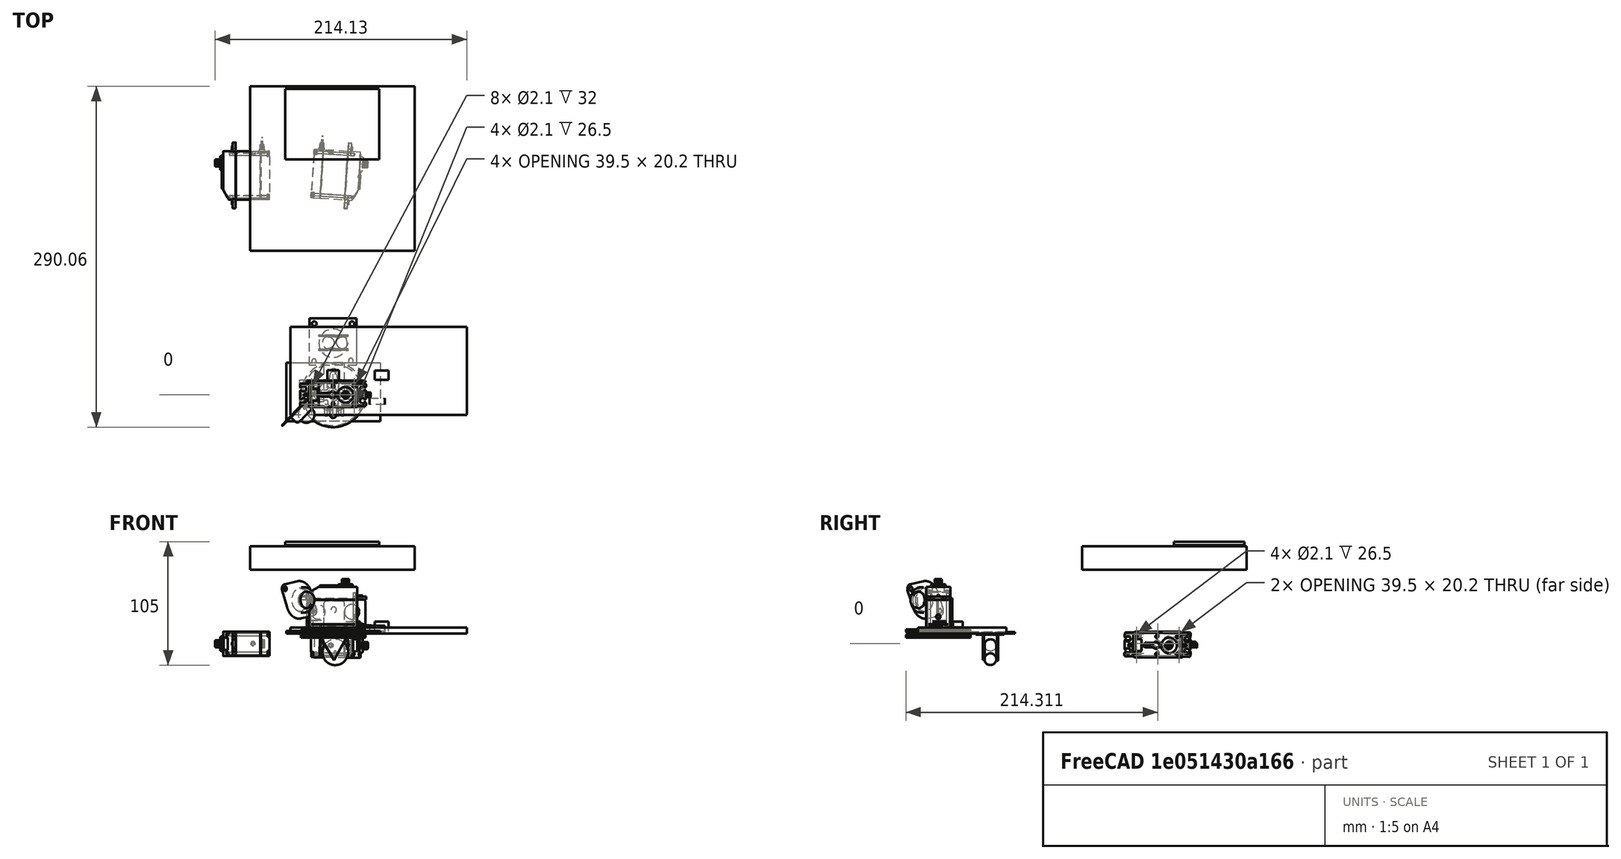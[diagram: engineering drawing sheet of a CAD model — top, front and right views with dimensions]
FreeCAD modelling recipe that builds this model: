
FCSTD DOCUMENT  (FreeCAD 0.19R24291 (Git))
Label: diseño_final
License: All rights reserved
LicenseURL: http://en.wikipedia.org/wiki/All_rights_reserved
objects: Sketcher::SketchObject×83, Part::Feature×51, PartDesign::Pad×39, PartDesign::Pocket×30, PartDesign::Body×19, Part::MultiFuse×16, App::LinkGroup×15, Part::Fillet×14, App::DocumentObjectGroup×10, Part::Box×8, Part::Compound×8, Part::Cut×6, PartDesign::PolarPattern×6, Part::Loft×6, Part::Mirroring×4, PartDesign::Mirrored×4, PartDesign::Fillet×4, PartDesign::Chamfer×4, Part::Cylinder×3, TechDraw::DrawProjGroupItem×3, +7 more types
note: 391 computed .brp shape members not serialized (recipe doc carries the construction recipe); baked Part::Feature solids carry a one-line shape summary decoded from their .brp

FEATURE [Sketcher::SketchObject] Sketch
  FullyConstrained = false
  MapMode = 5
  Support = -> [XY_Plane]
  sketch-geometry (8):
    g0: LineSegment StartX=-19.9829 StartY=19.2492 StartZ=0 EndX=20.0171 EndY=19.2492 EndZ=0
    g1: LineSegment StartX=20.0171 StartY=19.2492 StartZ=0 EndX=20.0171 EndY=-20.7508 EndZ=0
    g2: LineSegment StartX=20.0171 StartY=-20.7508 StartZ=0 EndX=-19.9829 EndY=-20.7508 EndZ=0
    g3: LineSegment StartX=-19.9829 StartY=-20.7508 StartZ=0 EndX=-19.9829 EndY=19.2492 EndZ=0
    g4: Circle CenterX=-16.0323 CenterY=14.5686 CenterZ=0 NormalX=0 NormalY=0 NormalZ=1 AngleXU=0 Radius=1.96692
    g5: Circle CenterX=16.0957 CenterY=14.4295 CenterZ=0 NormalX=0 NormalY=0 NormalZ=1 AngleXU=0 Radius=2.05352
    g6: Circle CenterX=15.1221 CenterY=-16.8639 CenterZ=0 NormalX=0 NormalY=0 NormalZ=1 AngleXU=0 Radius=1.99135
    g7: Circle CenterX=-16.1713 CenterY=-17.4203 CenterZ=0 NormalX=0 NormalY=0 NormalZ=1 AngleXU=0 Radius=1.95211
  constraints (10):
    c: Coincident(g0,g1)
    c: Coincident(g1,g2)
    c: Coincident(g2,g3)
    c: Coincident(g3,g0)
    c: Horizontal(g0)
    c: Horizontal(g2)
    c: Vertical(g1)
    c: Vertical(g3)
    c: DistanceY(g3,g3) = 40
    c: DistanceX(g0,g0) = 40
FEATURE [PartDesign::Pad] Pad
  Direction = (1,1,1)
  Length = 1
  Length2 = 100
  Profile = -> Sketch
  Type = 0
FEATURE [PartDesign::Body] Body  label="base_rueda"
  Group = -> [Sketch,Pad]
  Origin = -> Origin
  Placement = pos=(0,46,0) rot=(0,0,1;0rad)
  Tip = -> Pad
FEATURE [Sketcher::SketchObject] Sketch002
  FullyConstrained = false
  MapMode = 5
  Support = -> [XY_Plane001]
  sketch-geometry (4):
    g0: LineSegment StartX=11.942 StartY=-7.38734 StartZ=0 EndX=-0.260369 EndY=14.4324 EndZ=0
    g1: LineSegment StartX=-0.260369 StartY=14.4324 StartZ=0 EndX=-13.0556 EndY=-7.04506 EndZ=0
    g2: LineSegment StartX=-13.0556 StartY=-7.04506 StartZ=0 EndX=11.942 EndY=-7.38734 EndZ=0
    g3: Circle CenterX=-0.457983 CenterY=0 CenterZ=0 NormalX=0 NormalY=0 NormalZ=1 AngleXU=0 Radius=14.4338
  constraints (10):
    c: Coincident(g0,g1)
    c: Coincident(g1,g2)
    c: Coincident(g2,g0)
    c: Equal(g0,g1)
    c: Equal(g0,g2)
    c: PointOnObject(g0,g3)
    c: PointOnObject(g1,g3)
    c: PointOnObject(g2,g3)
    c: PointOnObject(g3,g-1)
    c: Distance(g2) = 25
FEATURE [PartDesign::Pad] Pad001
  Direction = (1,1,1)
  Length = 1
  Length2 = 100
  Profile = -> Sketch002
  Type = 0
FEATURE [PartDesign::Body] Body001  label="triangle1"
  Group = -> [Sketch002,Pad001]
  Origin = -> Origin001
  Placement = pos=(1,50,-9) rot=(-1,0,0;1.5708rad)
  Tip = -> Pad001
FEATURE [Sketcher::SketchObject] Sketch003
  FullyConstrained = false
  MapMode = 5
  Support = -> [XY_Plane002]
  sketch-geometry (4):
    g0: LineSegment StartX=11.942 StartY=-7.38734 StartZ=0 EndX=-0.260369 EndY=14.4324 EndZ=0
    g1: LineSegment StartX=-0.260369 StartY=14.4324 StartZ=0 EndX=-13.0556 EndY=-7.04506 EndZ=0
    g2: LineSegment StartX=-13.0556 StartY=-7.04506 StartZ=0 EndX=11.942 EndY=-7.38734 EndZ=0
    g3: Circle CenterX=-0.457983 CenterY=0 CenterZ=0 NormalX=0 NormalY=0 NormalZ=1 AngleXU=0 Radius=14.4338
  constraints (10):
    c: Coincident(g0,g1)
    c: Coincident(g1,g2)
    c: Coincident(g2,g0)
    c: Equal(g0,g1)
    c: Equal(g0,g2)
    c: PointOnObject(g0,g3)
    c: PointOnObject(g1,g3)
    c: PointOnObject(g2,g3)
    c: PointOnObject(g3,g-1)
    c: Distance(g2) = 25
FEATURE [PartDesign::Pad] Pad002
  Direction = (1,1,1)
  Length = 1
  Length2 = 100
  Profile = -> Sketch003
  Type = 0
FEATURE [PartDesign::Body] Body002  label="triangle2"
  Group = -> [Sketch003,Pad002]
  Origin = -> Origin002
  Placement = pos=(1,37.9904,-8.23205) rot=(-1,0,0;1.5708rad)
  Tip = -> Pad002
FEATURE [Part::Torus] Torus  label="rueda"
  Angle1 = -180
  Angle2 = 180
  Angle3 = 360
  AttacherType = Attacher::AttachEngine3D
  Placement = pos=(1.8355,44.3985,-16) rot=(0.57735,-0.57735,-0.57735;4.18879rad)
  Radius1 = 6
  Radius2 = 5
FEATURE [Part::Cylinder] Cylinder  label="base_movil"
  Angle = 360
  AttacherType = Attacher::AttachEngine3D
  Height = 1
  Placement = pos=(0,44,-1) rot=(0,0,1;0rad)
  Radius = 12
FEATURE [Sketcher::SketchObject] Sketch004
  FullyConstrained = false
  MapMode = 5
  Support = -> [XY_Plane003]
  sketch-geometry (8):
    g0: LineSegment StartX=-25.0348 StartY=11.057 StartZ=0 EndX=26.1474 EndY=11.057 EndZ=0
    g1: LineSegment StartX=26.1474 StartY=11.057 StartZ=0 EndX=26.1474 EndY=-9.24896 EndZ=0
    g2: LineSegment StartX=26.1474 StartY=-9.24896 StartZ=0 EndX=-25.0348 EndY=-9.24896 EndZ=0
    g3: LineSegment StartX=-25.0348 StartY=-9.24896 StartZ=0 EndX=-25.0348 EndY=11.057 EndZ=0
    g4: Circle CenterX=-23.0712 CenterY=8.82531 CenterZ=0 NormalX=0 NormalY=0 NormalZ=1 AngleXU=0 Radius=0.698514
    g5: Circle CenterX=23.9427 CenterY=8.43482 CenterZ=0 NormalX=0 NormalY=0 NormalZ=1 AngleXU=0 Radius=0.740892
    g6: Circle CenterX=24.0208 CenterY=-7.49681 CenterZ=0 NormalX=0 NormalY=0 NormalZ=1 AngleXU=0 Radius=0.707187
    g7: Circle CenterX=-23.1493 CenterY=-7.02823 CenterZ=0 NormalX=0 NormalY=0 NormalZ=1 AngleXU=0 Radius=0.720017
  constraints (8):
    c: Coincident(g0,g1)
    c: Coincident(g1,g2)
    c: Coincident(g2,g3)
    c: Coincident(g3,g0)
    c: Horizontal(g0)
    c: Horizontal(g2)
    c: Vertical(g1)
    c: Vertical(g3)
FEATURE [PartDesign::Pad] Pad003
  Direction = (1,1,1)
  Length = 2
  Length2 = 100
  Profile = -> Sketch004
  Type = 0
FEATURE [PartDesign::Body] Body003  label="Body"
  Group = -> [Sketch004,Pad003]
  Origin = -> Origin003
  Tip = -> Pad003
FEATURE [Part::FeaturePython] Tube  label="cilindro1"  # WARN: FeaturePython — macro-defined, semantics opaque (R4)
  AttacherType = Attacher::AttachEngine3D
  Height = 10
  InnerRadius = 5
  OuterRadius = 6
  Placement = pos=(-16,1,1) rot=(0,0,1;0rad)
FEATURE [Part::FeaturePython] Tube001  label="Cilindro2"  # WARN: FeaturePython — macro-defined, semantics opaque (R4)
  AttacherType = Attacher::AttachEngine3D
  Height = 10
  InnerRadius = 5
  OuterRadius = 6
  Placement = pos=(17,1,0) rot=(0,0,1;0rad)
FEATURE [Part::Box] Box  label="contacto1"
  AttacherType = Attacher::AttachEngine3D
  Height = 1
  Length = 2
  Placement = pos=(-7,-18,-1) rot=(0,0,1;0rad)
  Width = 10
FEATURE [Part::Box] Box001  label="contacto2"
  AttacherType = Attacher::AttachEngine3D
  Height = 1
  Length = 2
  Placement = pos=(-2,-18,-1) rot=(0,0,1;0rad)
  Width = 10
FEATURE [Part::Box] Box002  label="contacto3"
  AttacherType = Attacher::AttachEngine3D
  Height = 1
  Length = 2
  Placement = pos=(3,-18,-1) rot=(0,0,1;0rad)
  Width = 10
FEATURE [Part::Box] Box003  label="contacto4"
  AttacherType = Attacher::AttachEngine3D
  Height = 1
  Length = 2
  Placement = pos=(7,-18,-1) rot=(0,0,1;0rad)
  Width = 10
FEATURE [App::LinkGroup] LinkGroup  label="sensor_ultrasonidos"
  ElementList = -> [Box003,Box002,Tube001,Box,Box001,Body003,Tube]
  LinkMode = 0
  Placement = pos=(3.11266,-4.47148,19.5285) rot=(0,0.707107,-0.707107;3.14159rad)
FEATURE [Sketcher::SketchObject] Sketch005  label="wheel-generic-sketch"
  FullyConstrained = false
  MapMode = 5
  Placement = pos=(0,0,0) rot=(1,0,0;1.5708rad)
  sketch-geometry (7):
    g0: LineSegment StartX=0 StartY=-3.5 StartZ=0 EndX=0 EndY=3.5 EndZ=0
    g1: LineSegment StartX=0 StartY=3.5 StartZ=0 EndX=27.5 EndY=3.5 EndZ=0
    g2: LineSegment StartX=27.5 StartY=3.5 StartZ=0 EndX=27.5 EndY=1.5 EndZ=0
    g3: LineSegment StartX=27.5 StartY=1.5 StartZ=0 EndX=26 EndY=0 EndZ=0
    g4: LineSegment StartX=26 StartY=0 StartZ=0 EndX=27.5 EndY=-1.5 EndZ=0
    g5: LineSegment StartX=27.5 StartY=-1.5 StartZ=0 EndX=27.5 EndY=-3.5 EndZ=0
    g6: LineSegment StartX=27.5 StartY=-3.5 StartZ=0 EndX=0 EndY=-3.5 EndZ=0
  constraints (20):
    c: Vertical(g0)
    c: Coincident(g0,g1)
    c: Horizontal(g1)
    c: Coincident(g1,g2)
    c: Vertical(g2)
    c: Coincident(g2,g3)
    c: Coincident(g3,g4)
    c: Coincident(g4,g5)
    c: Coincident(g5,g6)
    c: Coincident(g6,g0)
    c: Horizontal(g6)
    c: Vertical(g5)
    c: PointOnObject(g0,g-2)
    c: Symmetric(g0,g0,g-1)
    c: PointOnObject(g3,g-1)
    c: Symmetric(g4,g2,g-1)
    c: Angle(g3,g-1) = 2.35619
    c: DistanceY(g4,g2) = 3
    c: DistanceX(g1) = 27.5
    c: DistanceY(g0) = 7
FEATURE [PartDesign::Revolution] Revolution  label="wheel-generic"
  AllowMultiFace = false
  Angle = 360
  Axis = (0,0,1)
  Base = (0,0,0)
  Placement = pos=(0,0,0) rot=(1,0,0;1.5708rad)
  Profile = -> Sketch005
  ReferenceAxis = -> Sketch005 [V_Axis]
  Reversed = true
FEATURE [Sketcher::SketchObject] Sketch001  label="horn-top-left-quarter-sketch"
  FullyConstrained = false
  MapMode = 5
  sketch-geometry (12):
    g0: LineSegment StartX=0 StartY=0 StartZ=0 EndX=0 EndY=19.7 EndZ=0
    g1: LineSegment StartX=-4.73762 StartY=4.73762 StartZ=0 EndX=0 EndY=0 EndZ=0
    g2: ArcOfCircle CenterX=-5.79828 CenterY=5.79828 CenterZ=0 NormalX=0 NormalY=0 NormalZ=1 AngleXU=0 Radius=1.5 StartAngle=4.7124 EndAngle=6.28317
    g3: ArcOfCircle CenterX=-17 CenterY=0 CenterZ=0 NormalX=0 NormalY=0 NormalZ=1 AngleXU=0 Radius=2.7 StartAngle=1.73871 EndAngle=3.14159
    g4: ArcOfCircle CenterX=0 CenterY=17 CenterZ=0 NormalX=0 NormalY=0 NormalZ=1 AngleXU=0 Radius=2.7 StartAngle=1.5708 EndAngle=2.97368
    g5: LineSegment StartX=-4.29828 StartY=5.79826 StartZ=0 EndX=-4.29828 EndY=7.79826 EndZ=0
    g6: LineSegment StartX=-5.79826 StartY=4.29828 StartZ=0 EndX=-7.79826 EndY=4.29828 EndZ=0
    g7: LineSegment StartX=-4.29828 StartY=7.79826 StartZ=0 EndX=-2.66203 EndY=17.4512 EndZ=0
    g8: LineSegment StartX=-17.4512 StartY=2.66203 StartZ=0 EndX=-7.79826 EndY=4.29828 EndZ=0
    g9: LineSegment StartX=-7.79826 StartY=4.29828 StartZ=0 EndX=-7.79826 EndY=0 EndZ=0
    g10: LineSegment StartX=-4.29828 StartY=7.79826 StartZ=0 EndX=0 EndY=7.79826 EndZ=0
    g11: LineSegment StartX=-19.7 StartY=0 StartZ=0 EndX=0 EndY=0 EndZ=0
  constraints (39):
    c: PointOnObject(g0,g-2)
    c: Coincident(g1,g-1)
    c: Angle(g-1,g1) = 2.35619
    c: PointOnObject(g2,g1)
    c: PointOnObject(g1,g2)
    c: Coincident(g4,g0)
    c: PointOnObject(g4,g0)
    c: Equal(g3,g4)
    c: Radius(g3) = 2.7
    c: Coincident(g5,g2)
    c: Vertical(g5)
    c: Coincident(g6,g2)
    c: Horizontal(g6)
    c: Equal(g6,g5)
    c: Tangent(g7,g4)
    c: Coincident(g7,g4)
    c: Coincident(g7,g5)
    c: Coincident(g8,g3)
    c: Coincident(g8,g6)
    c: Tangent(g8,g3)
    c: Tangent(g2,g6)
    c: DistanceX(g6) = -2
    c: Radius(g2) = 1.5
    c: Vertical(g9)
    c: Coincident(g9,g6)
    c: Horizontal(g10)
    c: Coincident(g10,g5)
    c: PointOnObject(g10,g0)
    c: Equal(g9,g10)
    c: Distance(g1) = 6.7
    c: PointOnObject(g3,g-1)
    c: PointOnObject(g3,g-1)
    c: Horizontal(g11)
    c: Coincident(g11,g-1)
    c: Coincident(g11,g3)
    c: Equal(g11,g0)
    c: PointOnObject(g9,g11)
    c: Coincident(g0,g-1)
    c: DistanceX(g11) = 19.7
FEATURE [PartDesign::Pad] Pad004  label="horn-top-left-quarter"
  AllowMultiFace = false
  Direction = (1,1,1)
  Length = 6
  Length2 = 100
  Profile = -> Sketch001
  Type = 0
FEATURE [Part::Mirroring] Part__Mirroring  label="horn-top-left-quarter (Mirror #1)"
  Base = (0,0,0)
  Normal = (1,0,0)
  Source = -> Pad004
FEATURE [Part::MultiFuse] Fusion
  Shapes = -> [Part__Mirroring,Pad004]
FEATURE [Part::Mirroring] Part__Mirroring001  label="Fusion (Mirror #2)"
  Base = (0,0,0)
  Normal = (0,1,0)
  Source = -> Fusion
FEATURE [Part::MultiFuse] Fusion001  label="4-arms-horn-body"
  Placement = pos=(0,0,-0.5) rot=(0,0,1;0rad)
  Shapes = -> [Part__Mirroring001,Fusion]
FEATURE [Part::Cut] Cut  label="wheel-horn"
  Base = -> Revolution
  Tool = -> Fusion001
FEATURE [Sketcher::SketchObject] Sketch006  label="shaft-drill-sketch"
  FullyConstrained = false
  MapMode = 5
  Placement = pos=(0,0,-0.5) rot=(0,0,1;0rad)
  Support = -> [Cut]
  sketch-geometry (1):
    g0: Circle CenterX=0 CenterY=0 CenterZ=0 NormalX=0 NormalY=0 NormalZ=1 AngleXU=0 Radius=5.2
  constraints (2):
    c: Coincident(g0,g-1)
    c: Radius(g0) = 5.2
FEATURE [PartDesign::Pocket] Pocket  label="shaft-drill"
  AllowMultiFace = false
  Length = 5
  Length2 = 100
  Profile = -> Sketch006
  Type = 1
FEATURE [Sketcher::SketchObject] Sketch007  label="drill-horn-master-sketch"
  FullyConstrained = false
  MapMode = 5
  Placement = pos=(0,0,-0.5) rot=(0,0,1;0rad)
  Support = -> [Pocket]
  sketch-geometry (1):
    g0: Circle CenterX=-16.15 CenterY=0 CenterZ=0 NormalX=0 NormalY=0 NormalZ=1 AngleXU=0 Radius=0.85
  constraints (3):
    c: PointOnObject(g0,g-1)
    c: Radius(g0) = 0.85
    c: DistanceX(g-1,g0) = -16.15
FEATURE [PartDesign::Pocket] Pocket001  label="drill-horn-master"
  AllowMultiFace = false
  Length = 5
  Length2 = 100
  Profile = -> Sketch007
  Type = 1
FEATURE [PartDesign::PolarPattern] PolarPattern  label="horn-drills"
  Angle = 360
  Axis = -> Sketch007 [N_Axis]
  Occurrences = 2
  Originals = -> [Pocket001]
FEATURE [Sketcher::SketchObject] Sketch008  label="horn-screw-room-master-sketch"
  FullyConstrained = false
  MapMode = 5
  Placement = pos=(0,8e-16,3.5) rot=(0,0,1;0rad)
  Support = -> [PolarPattern]
  sketch-geometry (1):
    g0: Circle CenterX=-16.15 CenterY=0 CenterZ=0 NormalX=0 NormalY=0 NormalZ=1 AngleXU=0 Radius=4
  constraints (3):
    c: PointOnObject(g0,g-1)
    c: DistanceX(g-1,g0) = -16.15
    c: Radius(g0) = 4
FEATURE [PartDesign::Pocket] Pocket002  label="horn-screw-room-master"
  AllowMultiFace = false
  Length = 4
  Length2 = 100
  Profile = -> Sketch008
  Type = 0
FEATURE [PartDesign::PolarPattern] PolarPattern001  label="horn-screws-room"
  Angle = 360
  Axis = -> Sketch008 [N_Axis]
  Occurrences = 2
  Originals = -> [Pocket002]
FEATURE [Part::Feature] PolarPattern001001  label="Renacuajo-wheel-4-arms-horn-final"
  shape: bbox 55 x 55 x 7 mm, 34 faces (baked)
FEATURE [App::LinkGroup] LinkGroup002  label="rueda1"
  ElementList = -> [PolarPattern001001,PolarPattern001]
  LinkMode = 0
  Placement = pos=(-99.447,198,-8.79556) rot=(0,-1,0;1.5708rad)
FEATURE [Sketcher::SketchObject] Sketch009  label="wheel-generic-sketch001"
  FullyConstrained = false
  MapMode = 5
  Placement = pos=(0,0,0) rot=(1,0,0;1.5708rad)
  sketch-geometry (7):
    g0: LineSegment StartX=0 StartY=-3.5 StartZ=0 EndX=0 EndY=3.5 EndZ=0
    g1: LineSegment StartX=0 StartY=3.5 StartZ=0 EndX=27.5 EndY=3.5 EndZ=0
    g2: LineSegment StartX=27.5 StartY=3.5 StartZ=0 EndX=27.5 EndY=1.5 EndZ=0
    g3: LineSegment StartX=27.5 StartY=1.5 StartZ=0 EndX=26 EndY=0 EndZ=0
    g4: LineSegment StartX=26 StartY=0 StartZ=0 EndX=27.5 EndY=-1.5 EndZ=0
    g5: LineSegment StartX=27.5 StartY=-1.5 StartZ=0 EndX=27.5 EndY=-3.5 EndZ=0
    g6: LineSegment StartX=27.5 StartY=-3.5 StartZ=0 EndX=0 EndY=-3.5 EndZ=0
  constraints (20):
    c: Vertical(g0)
    c: Coincident(g0,g1)
    c: Horizontal(g1)
    c: Coincident(g1,g2)
    c: Vertical(g2)
    c: Coincident(g2,g3)
    c: Coincident(g3,g4)
    c: Coincident(g4,g5)
    c: Coincident(g5,g6)
    c: Coincident(g6,g0)
    c: Horizontal(g6)
    c: Vertical(g5)
    c: PointOnObject(g0,g-2)
    c: Symmetric(g0,g0,g-1)
    c: PointOnObject(g3,g-1)
    c: Symmetric(g4,g2,g-1)
    c: Angle(g3,g-1) = 2.35619
    c: DistanceY(g4,g2) = 3
    c: DistanceX(g1) = 27.5
    c: DistanceY(g0) = 7
FEATURE [PartDesign::Revolution] Revolution001  label="wheel-generic001"
  AllowMultiFace = false
  Angle = 360
  Axis = (0,0,1)
  Base = (0,0,0)
  Placement = pos=(0,0,0) rot=(1,0,0;1.5708rad)
  Profile = -> Sketch009
  ReferenceAxis = -> Sketch009 [V_Axis]
  Reversed = true
FEATURE [Sketcher::SketchObject] Sketch010  label="horn-top-left-quarter-sketch001"
  FullyConstrained = false
  MapMode = 5
  sketch-geometry (12):
    g0: LineSegment StartX=0 StartY=0 StartZ=0 EndX=0 EndY=19.7 EndZ=0
    g1: LineSegment StartX=-4.73762 StartY=4.73762 StartZ=0 EndX=0 EndY=0 EndZ=0
    g2: ArcOfCircle CenterX=-5.79828 CenterY=5.79828 CenterZ=0 NormalX=0 NormalY=0 NormalZ=1 AngleXU=0 Radius=1.5 StartAngle=4.7124 EndAngle=6.28317
    g3: ArcOfCircle CenterX=-17 CenterY=0 CenterZ=0 NormalX=0 NormalY=0 NormalZ=1 AngleXU=0 Radius=2.7 StartAngle=1.73871 EndAngle=3.14159
    g4: ArcOfCircle CenterX=0 CenterY=17 CenterZ=0 NormalX=0 NormalY=0 NormalZ=1 AngleXU=0 Radius=2.7 StartAngle=1.5708 EndAngle=2.97368
    g5: LineSegment StartX=-4.29828 StartY=5.79826 StartZ=0 EndX=-4.29828 EndY=7.79826 EndZ=0
    g6: LineSegment StartX=-5.79826 StartY=4.29828 StartZ=0 EndX=-7.79826 EndY=4.29828 EndZ=0
    g7: LineSegment StartX=-4.29828 StartY=7.79826 StartZ=0 EndX=-2.66203 EndY=17.4512 EndZ=0
    g8: LineSegment StartX=-17.4512 StartY=2.66203 StartZ=0 EndX=-7.79826 EndY=4.29828 EndZ=0
    g9: LineSegment StartX=-7.79826 StartY=4.29828 StartZ=0 EndX=-7.79826 EndY=0 EndZ=0
    g10: LineSegment StartX=-4.29828 StartY=7.79826 StartZ=0 EndX=0 EndY=7.79826 EndZ=0
    g11: LineSegment StartX=-19.7 StartY=0 StartZ=0 EndX=0 EndY=0 EndZ=0
  constraints (39):
    c: PointOnObject(g0,g-2)
    c: Coincident(g1,g-1)
    c: Angle(g-1,g1) = 2.35619
    c: PointOnObject(g2,g1)
    c: PointOnObject(g1,g2)
    c: Coincident(g4,g0)
    c: PointOnObject(g4,g0)
    c: Equal(g3,g4)
    c: Radius(g3) = 2.7
    c: Coincident(g5,g2)
    c: Vertical(g5)
    c: Coincident(g6,g2)
    c: Horizontal(g6)
    c: Equal(g6,g5)
    c: Tangent(g7,g4)
    c: Coincident(g7,g4)
    c: Coincident(g7,g5)
    c: Coincident(g8,g3)
    c: Coincident(g8,g6)
    c: Tangent(g8,g3)
    c: Tangent(g2,g6)
    c: DistanceX(g6) = -2
    c: Radius(g2) = 1.5
    c: Vertical(g9)
    c: Coincident(g9,g6)
    c: Horizontal(g10)
    c: Coincident(g10,g5)
    c: PointOnObject(g10,g0)
    c: Equal(g9,g10)
    c: Distance(g1) = 6.7
    c: PointOnObject(g3,g-1)
    c: PointOnObject(g3,g-1)
    c: Horizontal(g11)
    c: Coincident(g11,g-1)
    c: Coincident(g11,g3)
    c: Equal(g11,g0)
    c: PointOnObject(g9,g11)
    c: Coincident(g0,g-1)
    c: DistanceX(g11) = 19.7
FEATURE [PartDesign::Pad] Pad005  label="horn-top-left-quarter001"
  AllowMultiFace = false
  Direction = (1,1,1)
  Length = 6
  Length2 = 100
  Profile = -> Sketch010
  Type = 0
FEATURE [Part::Mirroring] Part__Mirroring002  label="horn-top-left-quarter (Mirror #1)001"
  Base = (0,0,0)
  Normal = (1,0,0)
  Source = -> Pad005
FEATURE [Part::MultiFuse] Fusion002
  Shapes = -> [Part__Mirroring002,Pad005]
FEATURE [Part::Mirroring] Part__Mirroring003  label="Fusion (Mirror #2)001"
  Base = (0,0,0)
  Normal = (0,1,0)
  Source = -> Fusion002
FEATURE [Part::MultiFuse] Fusion003  label="4-arms-horn-body001"
  Placement = pos=(0,0,-0.5) rot=(0,0,1;0rad)
  Shapes = -> [Part__Mirroring003,Fusion002]
FEATURE [Part::Cut] Cut001  label="wheel-horn001"
  Base = -> Revolution001
  Tool = -> Fusion003
FEATURE [Sketcher::SketchObject] Sketch011  label="shaft-drill-sketch001"
  FullyConstrained = false
  MapMode = 5
  Placement = pos=(0,0,-0.5) rot=(0,0,1;0rad)
  Support = -> [Cut001]
  sketch-geometry (1):
    g0: Circle CenterX=0 CenterY=0 CenterZ=0 NormalX=0 NormalY=0 NormalZ=1 AngleXU=0 Radius=5.2
  constraints (2):
    c: Coincident(g0,g-1)
    c: Radius(g0) = 5.2
FEATURE [PartDesign::Pocket] Pocket003  label="shaft-drill001"
  AllowMultiFace = false
  Length = 5
  Length2 = 100
  Profile = -> Sketch011
  Type = 1
FEATURE [Sketcher::SketchObject] Sketch012  label="drill-horn-master-sketch001"
  FullyConstrained = false
  MapMode = 5
  Placement = pos=(0,0,-0.5) rot=(0,0,1;0rad)
  Support = -> [Pocket003]
  sketch-geometry (1):
    g0: Circle CenterX=-16.15 CenterY=0 CenterZ=0 NormalX=0 NormalY=0 NormalZ=1 AngleXU=0 Radius=0.85
  constraints (3):
    c: PointOnObject(g0,g-1)
    c: Radius(g0) = 0.85
    c: DistanceX(g-1,g0) = -16.15
FEATURE [PartDesign::Pocket] Pocket004  label="drill-horn-master001"
  AllowMultiFace = false
  Length = 5
  Length2 = 100
  Profile = -> Sketch012
  Type = 1
FEATURE [PartDesign::PolarPattern] PolarPattern001002  label="horn-drills001"
  Angle = 360
  Axis = -> Sketch012 [N_Axis]
  Occurrences = 2
  Originals = -> [Pocket004]
FEATURE [Sketcher::SketchObject] Sketch013  label="horn-screw-room-master-sketch001"
  FullyConstrained = false
  MapMode = 5
  Placement = pos=(0,8e-16,3.5) rot=(0,0,1;0rad)
  Support = -> [PolarPattern001002]
  sketch-geometry (1):
    g0: Circle CenterX=-16.15 CenterY=0 CenterZ=0 NormalX=0 NormalY=0 NormalZ=1 AngleXU=0 Radius=4
  constraints (3):
    c: PointOnObject(g0,g-1)
    c: DistanceX(g-1,g0) = -16.15
    c: Radius(g0) = 4
FEATURE [PartDesign::Pocket] Pocket005  label="horn-screw-room-master001"
  AllowMultiFace = false
  Length = 4
  Length2 = 100
  Profile = -> Sketch013
  Type = 0
FEATURE [PartDesign::PolarPattern] PolarPattern001003  label="horn-screws-room001"
  Angle = 360
  Axis = -> Sketch013 [N_Axis]
  Occurrences = 2
  Originals = -> [Pocket005]
FEATURE [Part::Feature] PolarPattern001004  label="Renacuajo-wheel-4-arms-horn-final001"
  shape: bbox 55 x 55 x 7 mm, 34 faces (baked)
FEATURE [App::LinkGroup] LinkGroup003  label="rueda2"
  ElementList = -> [PolarPattern001004,PolarPattern001003]
  LinkMode = 0
  Placement = pos=(30,196,-9.00002) rot=(0,-1,0;1.5708rad)
FEATURE [Sketcher::SketchObject] Sketch014
  FullyConstrained = false
  MapMode = 5
  Support = -> [XY_Plane004]
  sketch-geometry (4):
    g0: LineSegment StartX=-36.1738 StartY=-17.1935 StartZ=0 EndX=-36.1738 EndY=57.8065 EndZ=0
    g1: LineSegment StartX=-36.1738 StartY=57.8065 StartZ=0 EndX=113.826 EndY=57.8065 EndZ=0
    g2: LineSegment StartX=113.826 StartY=57.8065 StartZ=0 EndX=113.826 EndY=-17.1935 EndZ=0
    g3: LineSegment StartX=113.826 StartY=-17.1935 StartZ=0 EndX=-36.1738 EndY=-17.1935 EndZ=0
  constraints (10):
    c: Vertical(g0)
    c: DistanceY(g0,g0) = 75
    c: Coincident(g1,g0)
    c: Horizontal(g1)
    c: DistanceX(g1,g1) = 150
    c: Coincident(g2,g1)
    c: Vertical(g2)
    c: Equal(g0,g2)
    c: Coincident(g3,g2)
    c: Coincident(g3,g0)
FEATURE [PartDesign::Pad] Pad006
  Direction = (1,1,1)
  Length = 5
  Length2 = 100
  Profile = -> Sketch014
  Type = 0
FEATURE [PartDesign::Body] Body004  label="base_DieGo"
  Group = -> [Sketch014,Pad006]
  Origin = -> Origin004
  Tip = -> Pad006
FEATURE [Sketcher::SketchObject] Sketch015  label="servo-body-sketch"
  FullyConstrained = false
  MapMode = 5
  Placement = pos=(0,0,0) rot=(1,0,0;1.5708rad)
  sketch-geometry (5):
    g0: LineSegment StartX=20.55 StartY=39.6 StartZ=0 EndX=20.55 EndY=0 EndZ=0
    g1: LineSegment StartX=20.55 StartY=0 StartZ=0 EndX=-20.55 EndY=0 EndZ=0
    g2: LineSegment StartX=-20.55 StartY=0 StartZ=0 EndX=-20.55 EndY=34.9 EndZ=0
    g3: LineSegment StartX=-20.55 StartY=34.9 StartZ=0 EndX=-12.25 EndY=39.6 EndZ=0
    g4: LineSegment StartX=-12.25 StartY=39.6 StartZ=0 EndX=20.55 EndY=39.6 EndZ=0
  constraints (15):
    c: Coincident(g0,g1)
    c: Coincident(g1,g2)
    c: Horizontal(g1)
    c: Vertical(g0)
    c: Vertical(g2)
    c: Symmetric(g1,g0,g-2)
    c: PointOnObject(g1,g-1)
    c: DistanceX(g1) = -41.1
    c: DistanceY(g0) = -39.6
    c: Coincident(g3,g2)
    c: Horizontal(g4)
    c: Coincident(g4,g0)
    c: Coincident(g3,g4)
    c: DistanceY(g2) = 34.9
    c: DistanceX(g4) = 32.8
FEATURE [PartDesign::Pad] Pad007  label="servo-body-1"
  AllowMultiFace = false
  Direction = (1,1,1)
  Length = 20.8
  Length2 = 100
  Midplane = true
  Placement = pos=(0,0,0) rot=(1,0,0;1.5708rad)
  Profile = -> Sketch
  Type = 0
FEATURE [Sketcher::SketchObject] Sketch016  label="bottom-master-sketch"
  ExternalGeometry = -> [Pad007]
  FullyConstrained = false
  MapMode = 5
  Placement = pos=(0,0,0) rot=(1,0,0;3.14159rad)
  Support = -> [Pad007]
  sketch-geometry (15):
    g0: LineSegment StartX=-20.55 StartY=10.4 StartZ=0 EndX=-18.2075 EndY=8.05754 EndZ=0
    g1: Circle CenterX=-18.2075 CenterY=8.05754 CenterZ=0 NormalX=0 NormalY=0 NormalZ=1 AngleXU=0 Radius=1.05
    g2: GeomPoint X=-18.95 Y=8.8 Z=0
    g3: LineSegment StartX=-18.2075 StartY=8.05754 StartZ=0 EndX=-18.2075 EndY=6 EndZ=0
    g4: LineSegment StartX=-18.2075 StartY=8.05754 StartZ=0 EndX=-16.15 EndY=8.05754 EndZ=0
    g5: LineSegment StartX=-20.55 StartY=6 StartZ=0 EndX=-20.55 EndY=10.4 EndZ=0
    g6: LineSegment StartX=-20.55 StartY=10.4 StartZ=0 EndX=-16.15 EndY=10.4 EndZ=0
    g7: LineSegment StartX=-16.15 StartY=10.4 StartZ=0 EndX=-16.15 EndY=8.05754 EndZ=0
    g8: ArcOfCircle CenterX=-18.2075 CenterY=8.05754 CenterZ=0 NormalX=0 NormalY=0 NormalZ=1 AngleXU=0 Radius=2.05754 StartAngle=4.71239 EndAngle=6.28319
    g9: LineSegment StartX=-20.55 StartY=6 StartZ=0 EndX=-18.2075 EndY=6 EndZ=0
    g10: ArcOfCircle CenterX=-18.2075 CenterY=-8.05754 CenterZ=0 NormalX=0 NormalY=0 NormalZ=1 AngleXU=0 Radius=2.05754 StartAngle=5.46325e-06 EndAngle=1.5708
    g11: LineSegment StartX=-18.2075 StartY=-6 StartZ=0 EndX=-20.55 EndY=-6 EndZ=0
    g12: LineSegment StartX=-20.55 StartY=-6 StartZ=0 EndX=-20.55 EndY=-10.4 EndZ=0
    g13: LineSegment StartX=-20.55 StartY=-10.4 StartZ=0 EndX=-16.15 EndY=-10.4 EndZ=0
    g14: LineSegment StartX=-16.15 StartY=-10.4 StartZ=0 EndX=-16.15 EndY=-8.05753 EndZ=0
  constraints (40):
    c: Coincident(g0,g-4)
    c: Angle(g-4,g0) = 0.785398
    c: Radius(g1) = 1.05
    c: Coincident(g1,g0)
    c: PointOnObject(g2,g0)
    c: PointOnObject(g2,g1)
    c: DistanceX(g2,g0) = -1.6
    c: Vertical(g3)
    c: Coincident(g3,g0)
    c: Coincident(g0,g4)
    c: Horizontal(g4)
    c: Equal(g3,g4)
    c: Coincident(g5,g6)
    c: Vertical(g5)
    c: Horizontal(g6)
    c: Vertical(g7)
    c: Coincident(g7,g6)
    c: Coincident(g7,g4)
    c: Coincident(g5,g0)
    c: Coincident(g8,g0)
    c: Coincident(g8,g4)
    c: Coincident(g3,g8)
    c: Coincident(g9,g5)
    c: Coincident(g9,g3)
    c: Horizontal(g9)
    c: DistanceY(g0,g5) = -4.4
    c: Horizontal(g11)
    c: Coincident(g11,g12)
    c: Vertical(g12)
    c: Coincident(g12,g13)
    c: Horizontal(g13)
    c: Coincident(g13,g14)
    c: Vertical(g14)
    c: Coincident(g12,g-4)
    c: Symmetric(g10,g0,g-1)
    c: Symmetric(g13,g6,g-1)
    c: Symmetric(g11,g3,g-1)
    c: Equal(g10,g8)
    c: Coincident(g10,g11)
    c: Coincident(g10,g14)
FEATURE [PartDesign::Pocket] Pocket006  label="bottom-master"
  AllowMultiFace = false
  Length = 1.8
  Length2 = 100
  Placement = pos=(0,0,0) rot=(1,0,0;1.5708rad)
  Profile = -> Sketch001
  Type = 0
FEATURE [PartDesign::Mirrored] Mirrored  label="bottom-1"
  MirrorPlane = -> Sketch016 [V_Axis]
  Originals = -> [Pocket006]
  Placement = pos=(0,0,0) rot=(1,0,0;1.5708rad)
FEATURE [Sketcher::SketchObject] Sketch017  label="bottom-2-sketch"
  ExternalGeometry = -> [Mirrored]
  FullyConstrained = false
  MapMode = 5
  Placement = pos=(0,8e-16,1.8) rot=(1,0,0;3.14159rad)
  Support = -> [Mirrored]
  sketch-geometry (10):
    g0: LineSegment StartX=-20.55 StartY=10.4 StartZ=0 EndX=-18.85 EndY=8.7 EndZ=0
    g1: Circle CenterX=-18.1075 CenterY=7.95754 CenterZ=0 NormalX=0 NormalY=0 NormalZ=1 AngleXU=0 Radius=1.05
    g2: Circle CenterX=-18.1075 CenterY=7.95754 CenterZ=0 NormalX=0 NormalY=0 NormalZ=1 AngleXU=0 Radius=1.9
    g3: Circle CenterX=-18.1075 CenterY=-7.95754 CenterZ=0 NormalX=0 NormalY=0 NormalZ=1 AngleXU=0 Radius=1.9
    g4: Circle CenterX=18.1075 CenterY=7.95754 CenterZ=0 NormalX=0 NormalY=0 NormalZ=1 AngleXU=0 Radius=1.9
    g5: Circle CenterX=18.1075 CenterY=-7.95754 CenterZ=0 NormalX=0 NormalY=0 NormalZ=1 AngleXU=0 Radius=1.9
    g6: LineSegment StartX=-18.1075 StartY=7.95754 StartZ=0 EndX=18.1075 EndY=7.95754 EndZ=0
    g7: LineSegment StartX=18.1075 StartY=7.95754 StartZ=0 EndX=18.1075 EndY=-7.95754 EndZ=0
    g8: LineSegment StartX=18.1075 StartY=-7.95754 StartZ=0 EndX=-18.1075 EndY=-7.95754 EndZ=0
    g9: LineSegment StartX=-18.1075 StartY=-7.95754 StartZ=0 EndX=-18.1075 EndY=7.95754 EndZ=0
  constraints (24):
    c: Angle(g0,g-3) = 0.785398
    c: Coincident(g0,g-3)
    c: Radius(g1) = 1.05
    c: PointOnObject(g1,g0)
    c: PointOnObject(g0,g1)
    c: DistanceX(g0,g0) = 1.7
    c: Coincident(g2,g1)
    c: Radius(g2) = 1.9
    c: Equal(g3,g2)
    c: Equal(g2,g4)
    c: Equal(g4,g5)
    c: Coincident(g6,g7)
    c: Coincident(g7,g8)
    c: Coincident(g8,g9)
    c: Coincident(g9,g6)
    c: Horizontal(g6)
    c: Horizontal(g8)
    c: Vertical(g7)
    c: Vertical(g9)
    c: Symmetric(g6,g7,g-1)
    c: Coincident(g6,g1)
    c: Coincident(g3,g8)
    c: Coincident(g6,g4)
    c: Coincident(g5,g7)
FEATURE [PartDesign::Pocket] Pocket007  label="bottom-2"
  AllowMultiFace = false
  Length = 0.6
  Length2 = 100
  Placement = pos=(0,0,0) rot=(1,0,0;1.5708rad)
  Profile = -> Sketch002
  Type = 0
FEATURE [Sketcher::SketchObject] Sketch018  label="bottom-drills-sketch"
  ExternalGeometry = -> [Pocket007]
  FullyConstrained = false
  MapMode = 5
  Placement = pos=(0,1.3e-15,2.4) rot=(1,0,0;3.14159rad)
  Support = -> [Pocket007]
  sketch-geometry (8):
    g0: Circle CenterX=-18.1075 CenterY=7.95754 CenterZ=0 NormalX=0 NormalY=0 NormalZ=1 AngleXU=0 Radius=1.05
    g1: LineSegment StartX=-18.1075 StartY=7.95754 StartZ=0 EndX=18.1075 EndY=7.95754 EndZ=0
    g2: LineSegment StartX=18.1075 StartY=7.95754 StartZ=0 EndX=18.1075 EndY=-7.95754 EndZ=0
    g3: LineSegment StartX=18.1075 StartY=-7.95754 StartZ=0 EndX=-18.1075 EndY=-7.95754 EndZ=0
    g4: LineSegment StartX=-18.1075 StartY=-7.95754 StartZ=0 EndX=-18.1075 EndY=7.95754 EndZ=0
    g5: Circle CenterX=-18.1075 CenterY=-7.95754 CenterZ=0 NormalX=0 NormalY=0 NormalZ=1 AngleXU=0 Radius=1.05
    g6: Circle CenterX=18.1075 CenterY=7.95754 CenterZ=0 NormalX=0 NormalY=0 NormalZ=1 AngleXU=0 Radius=1.05
    g7: Circle CenterX=18.1075 CenterY=-7.95754 CenterZ=0 NormalX=0 NormalY=0 NormalZ=1 AngleXU=0 Radius=1.05
  constraints (18):
    c: Coincident(g0,g-3)
    c: Radius(g0) = 1.05
    c: Coincident(g1,g2)
    c: Coincident(g2,g3)
    c: Coincident(g3,g4)
    c: Coincident(g4,g1)
    c: Horizontal(g1)
    c: Horizontal(g3)
    c: Vertical(g2)
    c: Vertical(g4)
    c: Symmetric(g1,g2,g-1)
    c: Coincident(g1,g0)
    c: Equal(g6,g5)
    c: Equal(g5,g7)
    c: Equal(g7,g0)
    c: Coincident(g3,g5)
    c: Coincident(g6,g1)
    c: Coincident(g7,g2)
FEATURE [PartDesign::Pocket] Pocket008  label="bottom-drills"
  AllowMultiFace = false
  Length = 32
  Length2 = 100
  Placement = pos=(0,0,0) rot=(1,0,0;1.5708rad)
  Profile = -> Sketch003
  Type = 0
FEATURE [Sketcher::SketchObject] Sketch019  label="top-drills-1-sketch"
  ExternalGeometry = -> [Pocket008]
  FullyConstrained = false
  MapMode = 5
  Placement = pos=(0,8.7e-15,39.6) rot=(0,0,1;3.14159rad)
  Support = -> [Pocket008]
  sketch-geometry (9):
    g0: LineSegment StartX=-17.65 StartY=7.5 StartZ=0 EndX=-0.05 EndY=7.5 EndZ=0
    g1: LineSegment StartX=-0.05 StartY=7.5 StartZ=0 EndX=-0.05 EndY=-7.5 EndZ=0
    g2: LineSegment StartX=-0.05 StartY=-7.5 StartZ=0 EndX=-17.65 EndY=-7.5 EndZ=0
    g3: LineSegment StartX=-17.65 StartY=-7.5 StartZ=0 EndX=-17.65 EndY=7.5 EndZ=0
    g4: Circle CenterX=-0.05 CenterY=-7.5 CenterZ=0 NormalX=0 NormalY=0 NormalZ=1 AngleXU=0 Radius=1.25
    g5: Circle CenterX=-17.65 CenterY=-7.5 CenterZ=0 NormalX=0 NormalY=0 NormalZ=1 AngleXU=0 Radius=1.25
    g6: Circle CenterX=-0.05 CenterY=7.5 CenterZ=0 NormalX=0 NormalY=0 NormalZ=1 AngleXU=0 Radius=1.25
    g7: Circle CenterX=-17.65 CenterY=7.5 CenterZ=0 NormalX=0 NormalY=0 NormalZ=1 AngleXU=0 Radius=1.25
    g8: LineSegment StartX=-20.55 StartY=-10.4 StartZ=0 EndX=-17.65 EndY=-7.5 EndZ=0
  constraints (22):
    c: Coincident(g0,g1)
    c: Coincident(g1,g2)
    c: Coincident(g2,g3)
    c: Coincident(g3,g0)
    c: Horizontal(g0)
    c: Horizontal(g2)
    c: Vertical(g1)
    c: Vertical(g3)
    c: Symmetric(g2,g0,g-1)
    c: Equal(g4,g7)
    c: Equal(g7,g6)
    c: Equal(g6,g5)
    c: Radius(g4) = 1.25
    c: Coincident(g4,g1)
    c: Coincident(g6,g0)
    c: Coincident(g5,g2)
    c: Coincident(g7,g0)
    c: DistanceY(g-1,g1) = -7.5
    c: DistanceX(g2) = -17.6
    c: Coincident(g8,g-3)
    c: Coincident(g8,g2)
    c: Angle(g-3,g8) = 0.785398
FEATURE [PartDesign::Pocket] Pocket009  label="top-drills-1"
  AllowMultiFace = false
  Length = 0.2
  Length2 = 100
  Placement = pos=(0,0,0) rot=(1,0,0;1.5708rad)
  Profile = -> Sketch004
  Type = 0
FEATURE [Sketcher::SketchObject] Sketch020  label="potentiometer-1-sketch"
  FullyConstrained = false
  MapMode = 5
  Placement = pos=(20.55,0,0) rot=(0.707107,0,0.707107;3.14159rad)
  Support = -> [Pocket009]
  sketch-geometry (2):
    g0: Circle CenterX=14.175 CenterY=0 CenterZ=0 NormalX=0 NormalY=0 NormalZ=1 AngleXU=0 Radius=1.925
    g1: GeomPoint X=16.1 Y=0 Z=0
  constraints (5):
    c: PointOnObject(g0,g-1)
    c: Radius(g0) = 1.925
    c: PointOnObject(g1,g-1)
    c: PointOnObject(g1,g0)
    c: DistanceX(g-1,g1) = 16.1
FEATURE [PartDesign::Pocket] Pocket010  label="potentiometer-hole"
  AllowMultiFace = false
  Length = 2.2
  Length2 = 100
  Placement = pos=(0,0,0) rot=(1,0,0;1.5708rad)
  Profile = -> Sketch006
  Type = 0
FEATURE [Sketcher::SketchObject] Sketch021  label="potentiometer-cross-sketch"
  ExternalGeometry = -> [Pocket010]
  FullyConstrained = false
  MapMode = 5
  Placement = pos=(18.35,0,0) rot=(0.707107,0,0.707107;3.14159rad)
  Support = -> [Pocket010]
  sketch-geometry (12):
    g0: LineSegment StartX=13.675 StartY=1.65 StartZ=0 EndX=14.675 EndY=1.65 EndZ=0
    g1: LineSegment StartX=14.675 StartY=1.65 StartZ=0 EndX=14.675 EndY=0.5 EndZ=0
    g2: LineSegment StartX=14.675 StartY=-1.65 StartZ=0 EndX=13.675 EndY=-1.65 EndZ=0
    g3: LineSegment StartX=13.675 StartY=-1.65 StartZ=0 EndX=13.675 EndY=-0.5 EndZ=0
    g4: LineSegment StartX=12.525 StartY=0.5 StartZ=0 EndX=13.675 EndY=0.5 EndZ=0
    g5: LineSegment StartX=15.825 StartY=0.5 StartZ=0 EndX=15.825 EndY=-0.5 EndZ=0
    g6: LineSegment StartX=15.825 StartY=-0.5 StartZ=0 EndX=14.675 EndY=-0.5 EndZ=0
    g7: LineSegment StartX=12.525 StartY=-0.5 StartZ=0 EndX=12.525 EndY=0.5 EndZ=0
    g8: LineSegment StartX=14.675 StartY=0.5 StartZ=0 EndX=15.825 EndY=0.5 EndZ=0
    g9: LineSegment StartX=13.675 StartY=-0.5 StartZ=0 EndX=12.525 EndY=-0.5 EndZ=0
    g10: LineSegment StartX=13.675 StartY=0.5 StartZ=0 EndX=13.675 EndY=1.65 EndZ=0
    g11: LineSegment StartX=14.675 StartY=-0.5 StartZ=0 EndX=14.675 EndY=-1.65 EndZ=0
  constraints (30):
    c: Coincident(g0,g1)
    c: Coincident(g11,g2)
    c: Coincident(g2,g3)
    c: Coincident(g10,g0)
    c: Horizontal(g0)
    c: Horizontal(g2)
    c: Vertical(g1)
    c: Vertical(g3)
    c: Coincident(g8,g5)
    c: Coincident(g5,g6)
    c: Coincident(g9,g7)
    c: Coincident(g7,g4)
    c: Horizontal(g4)
    c: Horizontal(g6)
    c: Vertical(g5)
    c: Vertical(g7)
    c: Symmetric(g4,g5,g-3)
    c: Symmetric(g0,g11,g-3)
    c: Tangent(g4,g8)
    c: Tangent(g6,g9)
    c: Coincident(g3,g9)
    c: Coincident(g10,g4)
    c: Tangent(g3,g10)
    c: Coincident(g1,g8)
    c: Coincident(g11,g6)
    c: Tangent(g1,g11)
    c: Equal(g4,g10)
    c: Equal(g7,g0)
    c: DistanceX(g5,g4) = -3.3
    c: DistanceY(g5) = -1
FEATURE [PartDesign::Pocket] Pocket011  label="potentiometer-cross"
  AllowMultiFace = false
  Length = 1
  Length2 = 100
  Placement = pos=(0,0,0) rot=(1,0,0;1.5708rad)
  Profile = -> Sketch007
  Type = 0
FEATURE [Sketcher::SketchObject] Sketch022  label="label-plate-sketch"
  ExternalGeometry = -> [Pocket011]
  FullyConstrained = false
  MapMode = 5
  Placement = pos=(-19.9538,7.7e-15,35.2376) rot=(-0.254782,0,0.966998;3.14159rad)
  Support = -> [Pocket011]
  sketch-geometry (8):
    g0: LineSegment StartX=-7.65321 StartY=5.15 StartZ=0 EndX=-1.15321 EndY=5.15 EndZ=0
    g1: LineSegment StartX=-0.953214 StartY=4.95 StartZ=0 EndX=-0.953214 EndY=-4.95 EndZ=0
    g2: LineSegment StartX=-1.15321 StartY=-5.15 StartZ=0 EndX=-7.65321 EndY=-5.15 EndZ=0
    g3: LineSegment StartX=-7.85321 StartY=-4.95 StartZ=0 EndX=-7.85321 EndY=4.95 EndZ=0
    g4: ArcOfCircle CenterX=-7.65321 CenterY=4.95 CenterZ=0 NormalX=0 NormalY=0 NormalZ=1 AngleXU=0 Radius=0.2 StartAngle=1.5708 EndAngle=3.14159
    g5: ArcOfCircle CenterX=-1.15321 CenterY=4.95 CenterZ=0 NormalX=0 NormalY=0 NormalZ=1 AngleXU=0 Radius=0.2 StartAngle=0 EndAngle=1.5708
    g6: ArcOfCircle CenterX=-1.15321 CenterY=-4.95 CenterZ=0 NormalX=0 NormalY=0 NormalZ=1 AngleXU=0 Radius=0.2 StartAngle=4.71239 EndAngle=6.28319
    g7: ArcOfCircle CenterX=-7.65321 CenterY=-4.95 CenterZ=0 NormalX=0 NormalY=0 NormalZ=1 AngleXU=0 Radius=0.2 StartAngle=3.14159 EndAngle=4.71239
  constraints (20):
    c: Horizontal(g0)
    c: Horizontal(g2)
    c: Vertical(g1)
    c: Vertical(g3)
    c: Tangent(g0,g4)
    c: Tangent(g3,g4)
    c: Tangent(g0,g5)
    c: Tangent(g1,g5)
    c: Tangent(g1,g6)
    c: Tangent(g2,g6)
    c: Tangent(g2,g7)
    c: Tangent(g3,g7)
    c: Equal(g4,g5)
    c: Equal(g5,g7)
    c: Equal(g7,g6)
    c: Symmetric(g5,g6,g-1)
    c: DistanceY(g0,g2) = -10.3
    c: DistanceX(g3,g1) = 6.9
    c: Radius(g4) = 0.2
    c: DistanceX(g3,g-3) = -1
FEATURE [PartDesign::Pocket] Pocket012  label="Label-plate"
  AllowMultiFace = false
  Length = 0.1
  Length2 = 100
  Placement = pos=(0,0,0) rot=(1,0,0;1.5708rad)
  Profile = -> Sketch008
  Type = 0
FEATURE [Sketcher::SketchObject] Sketch023  label="top-left-2-drills-sketch"
  FullyConstrained = false
  MapMode = 5
  Placement = pos=(0,8.7e-15,39.6) rot=(0,0,1;3.14159rad)
  Support = -> [Pocket012]
  sketch-geometry (4):
    g0: Circle CenterX=18 CenterY=7.5 CenterZ=0 NormalX=0 NormalY=0 NormalZ=1 AngleXU=0 Radius=1.25
    g1: Circle CenterX=18 CenterY=-7.5 CenterZ=0 NormalX=0 NormalY=0 NormalZ=1 AngleXU=0 Radius=1.25
    g2: LineSegment StartX=18 StartY=7.5 StartZ=0 EndX=18 EndY=0 EndZ=0
    g3: LineSegment StartX=18 StartY=7.5 StartZ=0 EndX=19.25 EndY=7.5 EndZ=0
  constraints (10):
    c: Radius(g0) = 1.25
    c: Equal(g1,g0)
    c: Symmetric(g0,g1,g-1)
    c: Coincident(g2,g0)
    c: Vertical(g2)
    c: PointOnObject(g2,g-1)
    c: DistanceY(g2) = -7.5
    c: Horizontal(g3)
    c: Coincident(g3,g0)
    c: PointOnObject(g3,g0)
FEATURE [PartDesign::Pocket] Pocket013  label="top-left-2-drills"
  AllowMultiFace = false
  Length = 4.1
  Length2 = 100
  Placement = pos=(0,0,0) rot=(1,0,0;1.5708rad)
  Profile = -> Sketch009
  Type = 0
FEATURE [Sketcher::SketchObject] Sketch024  label="top-drills-cross-1-sketch"
  FullyConstrained = false
  MapMode = 5
  sketch-geometry (13):
    g0: Circle CenterX=0 CenterY=0 CenterZ=0 NormalX=0 NormalY=0 NormalZ=1 AngleXU=0 Radius=1.25
    g1: LineSegment StartX=-0.15 StartY=0.6 StartZ=0 EndX=0.15 EndY=0.6 EndZ=0
    g2: LineSegment StartX=0.15 StartY=0.6 StartZ=0 EndX=0.15 EndY=0.15 EndZ=0
    g3: LineSegment StartX=0.15 StartY=-0.6 StartZ=0 EndX=-0.15 EndY=-0.6 EndZ=0
    g4: LineSegment StartX=-0.15 StartY=-0.6 StartZ=0 EndX=-0.15 EndY=-0.15 EndZ=0
    g5: LineSegment StartX=-0.6 StartY=0.15 StartZ=0 EndX=-0.15 EndY=0.15 EndZ=0
    g6: LineSegment StartX=0.6 StartY=0.15 StartZ=0 EndX=0.6 EndY=-0.15 EndZ=0
    g7: LineSegment StartX=0.6 StartY=-0.15 StartZ=0 EndX=0.15 EndY=-0.15 EndZ=0
    g8: LineSegment StartX=-0.6 StartY=-0.15 StartZ=0 EndX=-0.6 EndY=0.15 EndZ=0
    g9: LineSegment StartX=0.15 StartY=0.15 StartZ=0 EndX=0.6 EndY=0.15 EndZ=0
    g10: LineSegment StartX=-0.15 StartY=-0.15 StartZ=0 EndX=-0.6 EndY=-0.15 EndZ=0
    g11: LineSegment StartX=-0.15 StartY=0.15 StartZ=0 EndX=-0.15 EndY=0.6 EndZ=0
    g12: LineSegment StartX=0.15 StartY=-0.15 StartZ=0 EndX=0.15 EndY=-0.6 EndZ=0
  constraints (32):
    c: Coincident(g0,g-1)
    c: Radius(g0) = 1.25
    c: Coincident(g1,g2)
    c: Coincident(g12,g3)
    c: Coincident(g3,g4)
    c: Coincident(g11,g1)
    c: Horizontal(g1)
    c: Horizontal(g3)
    c: Vertical(g2)
    c: Vertical(g4)
    c: Symmetric(g1,g12,g-1)
    c: Coincident(g9,g6)
    c: Coincident(g6,g7)
    c: Coincident(g10,g8)
    c: Coincident(g8,g5)
    c: Horizontal(g5)
    c: Horizontal(g7)
    c: Vertical(g6)
    c: Vertical(g8)
    c: Symmetric(g5,g6,g-1)
    c: Tangent(g5,g9)
    c: Tangent(g7,g10)
    c: Coincident(g4,g10)
    c: Coincident(g11,g5)
    c: Tangent(g4,g11)
    c: Coincident(g2,g9)
    c: Coincident(g12,g7)
    c: Tangent(g2,g12)
    c: Equal(g5,g11)
    c: Equal(g8,g1)
    c: DistanceX(g5,g6) = 1.2
    c: DistanceX(g1) = 0.3
FEATURE [PartDesign::Pad] Pad008  label="top-drills-cross-1"
  AllowMultiFace = false
  Direction = (1,1,1)
  Length = 10
  Length2 = 100
  Profile = -> Sketch010
  Type = 0
FEATURE [Sketcher::SketchObject] Sketch025  label="top-drills-cross-2-sketch"
  FullyConstrained = false
  MapMode = 5
  Placement = pos=(0,0,10) rot=(0,0,1;0rad)
  Support = -> [Pad008]
  sketch-geometry (1):
    g0: Circle CenterX=0 CenterY=0 CenterZ=0 NormalX=0 NormalY=0 NormalZ=1 AngleXU=0 Radius=1.25
  constraints (2):
    c: Coincident(g0,g-1)
    c: Radius(g0) = 1.25
FEATURE [PartDesign::Pad] Pad009  label="top-drills-cross-2"
  AllowMultiFace = false
  Direction = (1,1,1)
  Length = 1
  Length2 = 100
  Profile = -> Sketch011
  Type = 0
FEATURE [Part::Feature] Pad002001  label="top-drills-cross-01"
  Placement = pos=(17.65,7.5,39.2) rot=(0,0,1;0rad)
  shape: bbox 2.5 x 2.5 x 11 mm, 16 faces (baked)
FEATURE [Part::Feature] Pad002001001  label="top-drills-cross-002"
  Placement = pos=(17.65,-7.5,39.2) rot=(0,0,1;0rad)
  shape: bbox 2.5 x 2.5 x 11 mm, 16 faces (baked)
FEATURE [Part::Feature] Pad002001002  label="top-drills-cross-003"
  Placement = pos=(0.05,7.5,39.2) rot=(0,0,1;0rad)
  shape: bbox 2.5 x 2.5 x 11 mm, 16 faces (baked)
FEATURE [Part::Feature] Pad002001003  label="top-drills-cross-004"
  Placement = pos=(0.05,-7.5,39.2) rot=(0,0,1;0rad)
  shape: bbox 2.5 x 2.5 x 11 mm, 16 faces (baked)
FEATURE [Part::Feature] Pad002001003001  label="top-drills-cross-005"
  Placement = pos=(-18,7.5,35.2) rot=(0,0,1;0rad)
  shape: bbox 2.5 x 2.5 x 11 mm, 16 faces (baked)
FEATURE [Part::Feature] Pad002001003002  label="top-drills-cross-006"
  Placement = pos=(-18,-7.5,35.2) rot=(0,0,1;0rad)
  shape: bbox 2.5 x 2.5 x 11 mm, 16 faces (baked)
FEATURE [Part::MultiFuse] Fusion004  label="union-of-top-crosses"
  Shapes = -> [Pad002001,Pad002001003001,Pad002001003002,Pad002001002,Pad002001003,Pad002001001]
FEATURE [Part::Cut] Cut002  label="servo-body-final-1"
  Base = -> Pocket013
  Tool = -> Fusion004
FEATURE [Sketcher::SketchObject] Sketch026  label="shaft-anchor-sketch"
  ExternalGeometry = -> [Cut002]
  FullyConstrained = false
  MapMode = 5
  Placement = pos=(0,8.7e-15,39.6) rot=(0,0,1;0rad)
  Support = -> [Cut002]
  sketch-geometry (2):
    g0: Circle CenterX=10.55 CenterY=0 CenterZ=0 NormalX=0 NormalY=0 NormalZ=1 AngleXU=0 Radius=3
    g1: LineSegment StartX=13.55 StartY=0 StartZ=0 EndX=20.55 EndY=0 EndZ=0
  constraints (7):
    c: PointOnObject(g0,g-1)
    c: Radius(g0) = 3
    c: Horizontal(g1)
    c: PointOnObject(g1,g-3)
    c: PointOnObject(g1,g-1)
    c: PointOnObject(g1,g0)
    c: DistanceX(g1) = 7
FEATURE [PartDesign::Pad] Pad002001003003  label="servo-body-final-2"
  AllowMultiFace = false
  Direction = (1,1,1)
  Length = 0.1
  Length2 = 100
  Profile = -> Sketch012
  Type = 0
FEATURE [Sketcher::SketchObject] Sketch027  label="side-gap-sketch"
  FullyConstrained = false
  MapMode = 5
  sketch-geometry (25):
    g0: LineSegment StartX=-18.05 StartY=10.4 StartZ=0 EndX=18.05 EndY=10.4 EndZ=0
    g1: LineSegment StartX=20.05 StartY=8.4 StartZ=0 EndX=20.05 EndY=-8.4 EndZ=0
    g2: LineSegment StartX=18.05 StartY=-10.4 StartZ=0 EndX=-18.05 EndY=-10.4 EndZ=0
    g3: LineSegment StartX=-20.05 StartY=-8.4 StartZ=0 EndX=-20.05 EndY=8.4 EndZ=0
    g4: LineSegment StartX=-22.05 StartY=12.4 StartZ=0 EndX=-18.05 EndY=8.4 EndZ=0
    g5: LineSegment StartX=-18.05 StartY=10.1 StartZ=0 EndX=18.05 EndY=10.1 EndZ=0
    g6: LineSegment StartX=19.75 StartY=8.4 StartZ=0 EndX=19.75 EndY=-8.4 EndZ=0
    g7: LineSegment StartX=18.05 StartY=-10.1 StartZ=0 EndX=-18.05 EndY=-10.1 EndZ=0
    g8: LineSegment StartX=-19.75 StartY=-8.4 StartZ=0 EndX=-19.75 EndY=8.4 EndZ=0
    g9: LineSegment StartX=-22.05 StartY=12.4 StartZ=0 EndX=22.05 EndY=12.4 EndZ=0
    g10: LineSegment StartX=22.05 StartY=12.4 StartZ=0 EndX=22.05 EndY=-12.4 EndZ=0
    g11: LineSegment StartX=22.05 StartY=-12.4 StartZ=0 EndX=-22.05 EndY=-12.4 EndZ=0
    g12: LineSegment StartX=-22.05 StartY=-12.4 StartZ=0 EndX=-22.05 EndY=12.4 EndZ=0
    g13: ArcOfCircle CenterX=18.05 CenterY=-8.4 CenterZ=0 NormalX=0 NormalY=0 NormalZ=1 AngleXU=0 Radius=2 StartAngle=4.71239 EndAngle=6.28319
    g14: ArcOfCircle CenterX=18.05 CenterY=8.4 CenterZ=0 NormalX=0 NormalY=0 NormalZ=1 AngleXU=0 Radius=2 StartAngle=0 EndAngle=1.5708
    g15: ArcOfCircle CenterX=-18.05 CenterY=8.4 CenterZ=0 NormalX=0 NormalY=0 NormalZ=1 AngleXU=0 Radius=2 StartAngle=1.5708 EndAngle=3.14159
    g16: ArcOfCircle CenterX=-18.05 CenterY=-8.4 CenterZ=0 NormalX=0 NormalY=0 NormalZ=1 AngleXU=0 Radius=2 StartAngle=3.14159 EndAngle=4.71239
    g17: LineSegment StartX=-18.05 StartY=8.4 StartZ=0 EndX=18.05 EndY=8.4 EndZ=0
    g18: LineSegment StartX=18.05 StartY=8.4 StartZ=0 EndX=18.05 EndY=-8.4 EndZ=0
    g19: LineSegment StartX=18.05 StartY=-8.4 StartZ=0 EndX=-18.05 EndY=-8.4 EndZ=0
    g20: LineSegment StartX=-18.05 StartY=-8.4 StartZ=0 EndX=-18.05 EndY=8.4 EndZ=0
    g21: ArcOfCircle CenterX=-18.05 CenterY=8.4 CenterZ=0 NormalX=0 NormalY=0 NormalZ=1 AngleXU=0 Radius=1.7 StartAngle=1.5708 EndAngle=3.14159
    g22: ArcOfCircle CenterX=-18.05 CenterY=-8.4 CenterZ=0 NormalX=0 NormalY=0 NormalZ=1 AngleXU=0 Radius=1.7 StartAngle=3.14159 EndAngle=4.71239
    g23: ArcOfCircle CenterX=18.05 CenterY=-8.4 CenterZ=0 NormalX=0 NormalY=0 NormalZ=1 AngleXU=0 Radius=1.7 StartAngle=4.71239 EndAngle=6.28319
    g24: ArcOfCircle CenterX=18.05 CenterY=8.4 CenterZ=0 NormalX=0 NormalY=0 NormalZ=1 AngleXU=0 Radius=1.7 StartAngle=0 EndAngle=1.5708
  constraints (62):
    c: Horizontal(g0)
    c: Horizontal(g2)
    c: Vertical(g1)
    c: Vertical(g3)
    c: Angle(g-1,g4) = 2.35619
    c: Horizontal(g5)
    c: Horizontal(g7)
    c: Vertical(g6)
    c: Vertical(g8)
    c: Coincident(g9,g10)
    c: Coincident(g10,g11)
    c: Coincident(g11,g12)
    c: Coincident(g12,g9)
    c: Horizontal(g9)
    c: Horizontal(g11)
    c: Vertical(g10)
    c: Vertical(g12)
    c: PointOnObject(g9,g4)
    c: Symmetric(g9,g10,g-1)
    c: Coincident(g4,g9)
    c: Tangent(g1,g13)
    c: Tangent(g2,g13)
    c: Radius(g13) = 2
    c: Tangent(g0,g14)
    c: Tangent(g1,g14)
    c: Tangent(g0,g15)
    c: Tangent(g3,g15)
    c: Tangent(g2,g16)
    c: Tangent(g3,g16)
    c: Coincident(g17,g18)
    c: Coincident(g18,g19)
    c: Coincident(g19,g20)
    c: Coincident(g20,g17)
    c: Horizontal(g17)
    c: Horizontal(g19)
    c: Vertical(g18)
    c: Vertical(g20)
    c: Coincident(g17,g15)
    c: Symmetric(g15,g18,g-1)
    c: PointOnObject(g15,g4)
    c: Equal(g15,g16)
    c: Equal(g16,g14)
    c: Equal(g14,g13)
    c: DistanceX(g3,g1) = 40.1
    c: DistanceY(g0,g2) = -20.8
    c: Tangent(g8,g21)
    c: Tangent(g5,g21)
    c: PointOnObject(g21,g4)
    c: Coincident(g21,g15)
    c: Coincident(g4,g15)
    c: DistanceX(g8,g3) = -0.3
    c: DistanceX(g3,g4) = -2
    c: Tangent(g8,g22)
    c: Tangent(g7,g22)
    c: Coincident(g22,g16)
    c: Tangent(g7,g23)
    c: Tangent(g6,g23)
    c: Coincident(g23,g18)
    c: Tangent(g5,g24)
    c: Tangent(g6,g24)
    c: Coincident(g24,g17)
    c: Coincident(g14,g17)
FEATURE [PartDesign::Pad] Pad002001003004  label="side-gap-master"
  AllowMultiFace = false
  Direction = (1,1,1)
  Length = 0.4
  Length2 = 100
  Profile = -> Sketch013
  Type = 0
FEATURE [Sketcher::SketchObject] Sketch028  label="servo-top-1-sketch"
  FullyConstrained = false
  MapMode = 5
  sketch-geometry (10):
    g0: LineSegment StartX=-9.03485 StartY=1.65 StartZ=0 EndX=-9.03485 EndY=-1.65 EndZ=0
    g1: ArcOfCircle CenterX=-9.03485 CenterY=0 CenterZ=0 NormalX=0 NormalY=0 NormalZ=1 AngleXU=0 Radius=1.65 StartAngle=1.5708 EndAngle=4.71239
    g2: LineSegment StartX=-9.03485 StartY=1.65 StartZ=0 EndX=-2.38485 EndY=1.65 EndZ=0
    g3: LineSegment StartX=-9.03485 StartY=-1.65 StartZ=0 EndX=-2.38485 EndY=-1.65 EndZ=0
    g4: LineSegment StartX=11.1848 StartY=1.65 StartZ=0 EndX=11.1848 EndY=-1.65 EndZ=0
    g5: ArcOfCircle CenterX=0 CenterY=0 CenterZ=0 NormalX=0 NormalY=0 NormalZ=1 AngleXU=0 Radius=2.9 StartAngle=3.74684 EndAngle=5.67794
    g6: LineSegment StartX=2.38485 StartY=1.65 StartZ=0 EndX=11.1848 EndY=1.65 EndZ=0
    g7: ArcOfCircle CenterX=0 CenterY=0 CenterZ=0 NormalX=0 NormalY=0 NormalZ=1 AngleXU=0 Radius=2.9 StartAngle=0.605247 EndAngle=2.53635
    g8: LineSegment StartX=2.38485 StartY=-1.65 StartZ=0 EndX=11.1848 EndY=-1.65 EndZ=0
    g9: Circle CenterX=11.1848 CenterY=0 CenterZ=0 NormalX=0 NormalY=0 NormalZ=1 AngleXU=0 Radius=6.7
  constraints (29):
    c: Vertical(g0)
    c: Symmetric(g0,g0,g-1)
    c: Coincident(g1,g0)
    c: Coincident(g0,g1)
    c: PointOnObject(g1,g0)
    c: Horizontal(g2)
    c: Coincident(g2,g0)
    c: Horizontal(g3)
    c: Coincident(g3,g0)
    c: Coincident(g6,g4)
    c: Vertical(g4)
    c: Coincident(g4,g8)
    c: Tangent(g2,g6)
    c: PointOnObject(g7,g2)
    c: Equal(g5,g7)
    c: Coincident(g7,g6)
    c: Coincident(g5,g7)
    c: Coincident(g3,g5)
    c: Coincident(g8,g5)
    c: Tangent(g3,g8)
    c: Coincident(g7,g2)
    c: Coincident(g5,g-1)
    c: DistanceY(g0) = -3.3
    c: DistanceX(g0,g2) = 6.65
    c: Radius(g7) = 2.9
    c: Radius(g9) = 6.7
    c: PointOnObject(g9,g-1)
    c: PointOnObject(g9,g4)
    c: DistanceX(g6,g9) = 8.8
FEATURE [Sketcher::SketchObject] Sketch029  label="servo-top-1-sketch2"
  FullyConstrained = false
  MapMode = 5
  Placement = pos=(0,0,1.16) rot=(0,0,1;0rad)
  sketch-geometry (10):
    g0: LineSegment StartX=-8.99374 StartY=1.3 StartZ=0 EndX=-8.99374 EndY=-1.3 EndZ=0
    g1: ArcOfCircle CenterX=-8.99374 CenterY=0 CenterZ=0 NormalX=0 NormalY=0 NormalZ=1 AngleXU=0 Radius=1.3 StartAngle=1.5708 EndAngle=4.71239
    g2: LineSegment StartX=-8.99374 StartY=1.3 StartZ=0 EndX=-2.19374 EndY=1.3 EndZ=0
    g3: LineSegment StartX=-8.99374 StartY=-1.3 StartZ=0 EndX=-2.19374 EndY=-1.3 EndZ=0
    g4: LineSegment StartX=11.1937 StartY=1.3 StartZ=0 EndX=11.1937 EndY=-1.3 EndZ=0
    g5: ArcOfCircle CenterX=0 CenterY=0 CenterZ=0 NormalX=0 NormalY=0 NormalZ=1 AngleXU=0 Radius=2.55 StartAngle=3.67655 EndAngle=5.74823
    g6: LineSegment StartX=2.19374 StartY=1.3 StartZ=0 EndX=11.1937 EndY=1.3 EndZ=0
    g7: ArcOfCircle CenterX=0 CenterY=0 CenterZ=0 NormalX=0 NormalY=0 NormalZ=1 AngleXU=0 Radius=2.55 StartAngle=0.534957 EndAngle=2.60664
    g8: LineSegment StartX=2.19374 StartY=-1.3 StartZ=0 EndX=11.1937 EndY=-1.3 EndZ=0
    g9: Circle CenterX=11.1937 CenterY=0 CenterZ=0 NormalX=0 NormalY=0 NormalZ=1 AngleXU=0 Radius=6.7
  constraints (29):
    c: Vertical(g0)
    c: Symmetric(g0,g0,g-1)
    c: Coincident(g1,g0)
    c: Coincident(g0,g1)
    c: PointOnObject(g1,g0)
    c: Horizontal(g2)
    c: Coincident(g2,g0)
    c: Horizontal(g3)
    c: Coincident(g3,g0)
    c: Coincident(g6,g4)
    c: Vertical(g4)
    c: Coincident(g4,g8)
    c: Tangent(g2,g6)
    c: PointOnObject(g7,g2)
    c: Equal(g5,g7)
    c: Coincident(g7,g6)
    c: Coincident(g5,g7)
    c: Coincident(g3,g5)
    c: Coincident(g8,g5)
    c: Tangent(g3,g8)
    c: Coincident(g7,g2)
    c: Coincident(g5,g-1)
    c: DistanceY(g0) = -2.6
    c: DistanceX(g0,g2) = 6.8
    c: Radius(g7) = 2.55
    c: Radius(g9) = 6.7
    c: PointOnObject(g9,g-1)
    c: PointOnObject(g9,g4)
    c: DistanceX(g6,g9) = 9
FEATURE [Part::Loft] Loft  label="servo-top-1"
  Closed = false
  MaxDegree = 5
  Ruled = false
  Sections = -> [Sketch028,Sketch029]
  Solid = true
FEATURE [Sketcher::SketchObject] Sketch030  label="shaft-base-1-sketch"
  FullyConstrained = false
  MapMode = 5
  sketch-geometry (1):
    g0: Circle CenterX=0 CenterY=0 CenterZ=0 NormalX=0 NormalY=0 NormalZ=1 AngleXU=0 Radius=6.7
  constraints (2):
    c: Radius(g0) = 6.7
    c: Coincident(g-1,g0)
FEATURE [Sketcher::SketchObject] Sketch031  label="shaft-base-1-sketch2"
  FullyConstrained = false
  MapMode = 5
  Placement = pos=(0,0,2.2) rot=(0,0,1;0rad)
  sketch-geometry (1):
    g0: Circle CenterX=0 CenterY=0 CenterZ=0 NormalX=0 NormalY=0 NormalZ=1 AngleXU=0 Radius=5.85
  constraints (2):
    c: Radius(g0) = 5.85
    c: Coincident(g-1,g0)
FEATURE [Part::Loft] Loft001  label="Shaft-base-1"
  Closed = false
  MaxDegree = 5
  Placement = pos=(11.1848,0,0) rot=(0,0,1;0rad)
  Ruled = false
  Sections = -> [Sketch030,Sketch031]
  Solid = true
FEATURE [Part::MultiFuse] Fusion005  label="top-part-1"
  Shapes = -> [Loft,Loft001]
FEATURE [PartDesign::Fillet] Fillet
  Base = -> Fusion005 [Edge25]
  Radius = 0.5
  SupportTransform = false
FEATURE [Part::Fillet] Fillet001  label="top-part-2"
  Base = -> Fillet
  Edges = 8 edges r=0.1: [Edge6,Edge17,Edge19,Edge20,Edge21,Edge22,Edge23,Edge24]
FEATURE [App::DocumentObjectGroup] Group001  label="top-part-src"
  Group = -> [Fusion005,Fillet001]
FEATURE [Part::Feature] Fillet002  label="top-part"
  Placement = pos=(-0.634848,0,39.7) rot=(0,0,1;0rad)
  shape: bbox 28.82 x 13.4 x 14.16 mm, 24 faces (baked)
FEATURE [Sketcher::SketchObject] Sketch032  label="ears-body-1-sketch"
  FullyConstrained = false
  MapMode = 5
  sketch-geometry (4):
    g0: LineSegment StartX=-28 StartY=9.6 StartZ=0 EndX=28 EndY=9.6 EndZ=0
    g1: LineSegment StartX=28 StartY=9.6 StartZ=0 EndX=28 EndY=-9.6 EndZ=0
    g2: LineSegment StartX=28 StartY=-9.6 StartZ=0 EndX=-28 EndY=-9.6 EndZ=0
    g3: LineSegment StartX=-28 StartY=-9.6 StartZ=0 EndX=-28 EndY=9.6 EndZ=0
  constraints (11):
    c: Coincident(g0,g1)
    c: Coincident(g1,g2)
    c: Coincident(g2,g3)
    c: Coincident(g3,g0)
    c: Horizontal(g0)
    c: Horizontal(g2)
    c: Vertical(g1)
    c: Vertical(g3)
    c: Symmetric(g0,g1,g-1)
    c: DistanceX(g0) = 56
    c: DistanceY(g3) = 19.2
FEATURE [PartDesign::Pad] Pad002001003004001002  label="ears-body-1"
  AllowMultiFace = false
  Direction = (1,1,1)
  Length = 2.5
  Length2 = 100
  Profile = -> Sketch019
  Type = 0
FEATURE [Sketcher::SketchObject] Sketch033  label="right-ears-sketch"
  FullyConstrained = false
  MapMode = 5
  Placement = pos=(0,0,2.5) rot=(0,0,1;0rad)
  Support = -> [Pad002001003004001002]
  sketch-geometry (9):
    g0: ArcOfCircle CenterX=25.15 CenterY=5.1 CenterZ=0 NormalX=0 NormalY=0 NormalZ=1 AngleXU=0 Radius=2.25 StartAngle=0.605154 EndAngle=5.67803
    g1: LineSegment StartX=22.9 StartY=5.1 StartZ=0 EndX=25.15 EndY=5.1 EndZ=0
    g2: LineSegment StartX=27.0004 StartY=6.38 StartZ=0 EndX=29.0004 EndY=6.38 EndZ=0
    g3: LineSegment StartX=29.0004 StartY=6.38 StartZ=0 EndX=29.0004 EndY=3.82 EndZ=0
    g4: LineSegment StartX=29.0004 StartY=3.82 StartZ=0 EndX=27.0004 EndY=3.82 EndZ=0
    g5: ArcOfCircle CenterX=25.15 CenterY=-5.1 CenterZ=0 NormalX=0 NormalY=0 NormalZ=1 AngleXU=0 Radius=2.25 StartAngle=0.605154 EndAngle=5.67803
    g6: LineSegment StartX=27.0004 StartY=-3.82 StartZ=0 EndX=29.0004 EndY=-3.82 EndZ=0
    g7: LineSegment StartX=29.0004 StartY=-3.82 StartZ=0 EndX=29.0004 EndY=-6.38 EndZ=0
    g8: LineSegment StartX=29.0004 StartY=-6.38 StartZ=0 EndX=27.0004 EndY=-6.38 EndZ=0
  constraints (28):
    c: Radius(g0) = 2.25
    c: DistanceX(g0) = 25.15
    c: DistanceY(g0) = 5.1
    c: Horizontal(g1)
    c: PointOnObject(g1,g0)
    c: Coincident(g1,g0)
    c: Coincident(g2,g3)
    c: Coincident(g3,g4)
    c: Horizontal(g2)
    c: Horizontal(g4)
    c: Vertical(g3)
    c: Coincident(g0,g2)
    c: Coincident(g0,g4)
    c: Symmetric(g0,g0,g1)
    c: DistanceY(g3) = -2.56
    c: DistanceX(g2) = 2
    c: Symmetric(g5,g0,g-1)
    c: Equal(g0,g5)
    c: Coincident(g6,g7)
    c: Coincident(g7,g8)
    c: Horizontal(g6)
    c: Horizontal(g8)
    c: Vertical(g7)
    c: Coincident(g6,g5)
    c: Coincident(g8,g5)
    c: Symmetric(g5,g0,g-1)
    c: Symmetric(g0,g5,g-1)
    c: Symmetric(g6,g3,g-1)
FEATURE [PartDesign::Pocket] Pocket014  label="right-ear"
  AllowMultiFace = false
  Length = 5
  Length2 = 100
  Profile = -> Sketch020
  Type = 1
FEATURE [PartDesign::Mirrored] Mirrored001  label="ears-block-1"
  MirrorPlane = -> Sketch033 [V_Axis]
  Originals = -> [Pocket014]
FEATURE [Sketcher::SketchObject] Sketch034  label="ears-block-2-sketch"
  FullyConstrained = false
  MapMode = 5
  Placement = pos=(0,0,2.5) rot=(0,0,1;0rad)
  Support = -> [Mirrored001]
  sketch-geometry (6):
    g0: ArcOfCircle CenterX=-23.8 CenterY=0 CenterZ=0 NormalX=0 NormalY=0 NormalZ=1 AngleXU=0 Radius=1 StartAngle=1.57079 EndAngle=4.7124
    g1: ArcOfCircle CenterX=23.8 CenterY=0 CenterZ=0 NormalX=0 NormalY=0 NormalZ=1 AngleXU=0 Radius=1 StartAngle=4.71238 EndAngle=7.85399
    g2: LineSegment StartX=-23.8 StartY=-1 StartZ=0 EndX=23.8 EndY=-1 EndZ=0
    g3: LineSegment StartX=-23.8 StartY=1 StartZ=0 EndX=23.8 EndY=1 EndZ=0
    g4: GeomPoint X=-24.8 Y=0 Z=0
    g5: GeomPoint X=24.8 Y=0 Z=0
  constraints (18):
    c: Tangent(g0,g2)
    c: Tangent(g0,g3)
    c: Tangent(g1,g2)
    c: Tangent(g1,g3)
    c: Coincident(g0,g3)
    c: Coincident(g0,g2)
    c: Coincident(g2,g1)
    c: Coincident(g3,g1)
    c: Horizontal(g2)
    c: Equal(g0,g1)
    c: Symmetric(g0,g1,g-2)
    c: PointOnObject(g0,g-1)
    c: DistanceY(g0,g0) = 2
    c: PointOnObject(g4,g-1)
    c: PointOnObject(g4,g0)
    c: PointOnObject(g5,g-1)
    c: PointOnObject(g5,g1)
    c: DistanceX(g4,g5) = 49.6
FEATURE [PartDesign::Pad] Pad002001003004001003  label="ears-block-2"
  AllowMultiFace = false
  Direction = (1,1,1)
  Length = 0.86
  Length2 = 100
  Profile = -> Sketch021
  Type = 0
FEATURE [Sketcher::SketchObject] Sketch035  label="wire-holder-base-sketch"
  FullyConstrained = false
  MapMode = 5
  Placement = pos=(0,0,0) rot=(0.57735,0.57735,0.57735;2.0944rad)
  sketch-geometry (4):
    g0: LineSegment StartX=-3.4 StartY=2.15 StartZ=0 EndX=3.4 EndY=2.15 EndZ=0
    g1: LineSegment StartX=3.4 StartY=2.15 StartZ=0 EndX=3.4 EndY=-2.15 EndZ=0
    g2: LineSegment StartX=3.4 StartY=-2.15 StartZ=0 EndX=-3.4 EndY=-2.15 EndZ=0
    g3: LineSegment StartX=-3.4 StartY=-2.15 StartZ=0 EndX=-3.4 EndY=2.15 EndZ=0
  constraints (11):
    c: Coincident(g0,g1)
    c: Coincident(g1,g2)
    c: Coincident(g2,g3)
    c: Coincident(g3,g0)
    c: Horizontal(g0)
    c: Horizontal(g2)
    c: Vertical(g1)
    c: Vertical(g3)
    c: Symmetric(g0,g1,g-1)
    c: DistanceY(g1) = -4.3
    c: DistanceX(g0) = 6.8
FEATURE [PartDesign::Pad] Pad002001003004001005  label="wire-holder-base"
  AllowMultiFace = false
  Direction = (1,1,1)
  Length = 1.5
  Length2 = 100
  Placement = pos=(0,0,0) rot=(0.57735,0.57735,0.57735;2.0944rad)
  Profile = -> Sketch022
  Type = 0
FEATURE [Sketcher::SketchObject] Sketch036  label="wire-holder-body-1-sketch"
  FullyConstrained = false
  MapMode = 5
  Placement = pos=(0,0,0) rot=(0.57735,0.57735,0.57735;2.0944rad)
  sketch-geometry (4):
    g0: LineSegment StartX=-2.975 StartY=1.85 StartZ=0 EndX=2.975 EndY=1.85 EndZ=0
    g1: LineSegment StartX=2.975 StartY=1.85 StartZ=0 EndX=2.975 EndY=-1.85 EndZ=0
    g2: LineSegment StartX=2.975 StartY=-1.85 StartZ=0 EndX=-2.975 EndY=-1.85 EndZ=0
    g3: LineSegment StartX=-2.975 StartY=-1.85 StartZ=0 EndX=-2.975 EndY=1.85 EndZ=0
  constraints (11):
    c: Coincident(g0,g1)
    c: Coincident(g1,g2)
    c: Coincident(g2,g3)
    c: Coincident(g3,g0)
    c: Horizontal(g0)
    c: Horizontal(g2)
    c: Vertical(g1)
    c: Vertical(g3)
    c: Symmetric(g0,g1,g-1)
    c: DistanceX(g0) = 5.95
    c: DistanceY(g3) = 3.7
FEATURE [Sketcher::SketchObject] Sketch037  label="wire-holder-body-1-sketch2"
  FullyConstrained = false
  MapMode = 5
  Placement = pos=(4.2,0,0) rot=(0.57735,0.57735,0.57735;2.0944rad)
  sketch-geometry (4):
    g0: LineSegment StartX=-2.7 StartY=1.55 StartZ=0 EndX=2.7 EndY=1.55 EndZ=0
    g1: LineSegment StartX=2.7 StartY=1.55 StartZ=0 EndX=2.7 EndY=-1.55 EndZ=0
    g2: LineSegment StartX=2.7 StartY=-1.55 StartZ=0 EndX=-2.7 EndY=-1.55 EndZ=0
    g3: LineSegment StartX=-2.7 StartY=-1.55 StartZ=0 EndX=-2.7 EndY=1.55 EndZ=0
  constraints (11):
    c: Coincident(g0,g1)
    c: Coincident(g1,g2)
    c: Coincident(g2,g3)
    c: Coincident(g3,g0)
    c: Horizontal(g0)
    c: Horizontal(g2)
    c: Vertical(g1)
    c: Vertical(g3)
    c: Symmetric(g0,g1,g-1)
    c: DistanceX(g0) = 5.4
    c: DistanceY(g1) = -3.1
FEATURE [Part::Loft] Loft002  label="wire-holder-body-1"
  Closed = false
  MaxDegree = 5
  Ruled = false
  Sections = -> [Sketch036,Sketch037]
  Solid = true
FEATURE [Sketcher::SketchObject] Sketch038  label="wire-holes-sketch"
  FullyConstrained = false
  MapMode = 5
  Placement = pos=(4.2,-7e-16,0) rot=(0.57735,0.57735,0.57735;2.0944rad)
  Support = -> [Loft002]
  sketch-geometry (8):
    g0: ArcOfCircle CenterX=-1.2 CenterY=0 CenterZ=0 NormalX=0 NormalY=0 NormalZ=1 AngleXU=0 Radius=0.7 StartAngle=0.666946 EndAngle=5.61624
    g1: LineSegment StartX=-0.65 StartY=0.433013 StartZ=0 EndX=-0.55 EndY=0.433013 EndZ=0
    g2: ArcOfCircle CenterX=0 CenterY=0 CenterZ=0 NormalX=0 NormalY=0 NormalZ=1 AngleXU=0 Radius=0.7 StartAngle=0.666946 EndAngle=2.47465
    g3: LineSegment StartX=0.55 StartY=0.433013 StartZ=0 EndX=0.65 EndY=0.433013 EndZ=0
    g4: LineSegment StartX=-0.65 StartY=-0.433013 StartZ=0 EndX=-0.55 EndY=-0.433013 EndZ=0
    g5: ArcOfCircle CenterX=0 CenterY=0 CenterZ=0 NormalX=0 NormalY=0 NormalZ=1 AngleXU=0 Radius=0.7 StartAngle=3.80854 EndAngle=5.61624
    g6: ArcOfCircle CenterX=1.2 CenterY=0 CenterZ=0 NormalX=0 NormalY=0 NormalZ=1 AngleXU=0 Radius=0.7 StartAngle=3.80854 EndAngle=8.75783
    g7: LineSegment StartX=0.55 StartY=-0.433013 StartZ=0 EndX=0.65 EndY=-0.433013 EndZ=0
  constraints (26):
    c: PointOnObject(g0,g-1)
    c: Horizontal(g1)
    c: Coincident(g1,g0)
    c: Coincident(g3,g6)
    c: Coincident(g1,g2)
    c: Coincident(g3,g2)
    c: Tangent(g1,g3)
    c: Horizontal(g4)
    c: Symmetric(g0,g4,g-1)
    c: PointOnObject(g0,g4)
    c: PointOnObject(g6,g4)
    c: Coincident(g4,g5)
    c: Coincident(g7,g5)
    c: Tangent(g4,g7)
    c: PointOnObject(g7,g6)
    c: Equal(g1,g4)
    c: Equal(g4,g3)
    c: Equal(g3,g7)
    c: Equal(g5,g0)
    c: Equal(g0,g2)
    c: Equal(g2,g6)
    c: Radius(g6) = 0.7
    c: DistanceX(g0,g6) = 2.4
    c: Coincident(g5,g-1)
    c: Coincident(g2,g-1)
    c: DistanceX(g1) = 0.1
FEATURE [PartDesign::Pocket] Pocket015  label="wire-holder-body-2"
  AllowMultiFace = false
  Length = 5
  Length2 = 100
  Profile = -> Sketch025
  Type = 1
FEATURE [Part::Feature] Pocket016  label="wire-holder-body-2-copy"
  Placement = pos=(1.5,0,0) rot=(0,0,1;0rad)
  shape: bbox 4.2 x 5.95 x 3.7 mm, 14 faces (baked)
FEATURE [Part::MultiFuse] Fusion006  label="wire-holder-body-3"
  Shapes = -> [Pad002001003004001005,Pocket016]
FEATURE [Part::Fillet] Fillet003  label="wire-holder-body-4"
  Base = -> Fusion006
  Edges = 8 edges r=0.5: [Edge1,Edge2,Edge5,Edge8,Edge17,Edge18,Edge20,Edge22]
FEATURE [App::DocumentObjectGroup] Group003  label="wire-holder-src"
  Group = -> [Pad002001003004001005,Loft002,Pocket015,Pocket016,Fusion006,Fillet003]
FEATURE [Part::Feature] Fillet003001  label="wire-holder"
  Placement = pos=(20.55,0,6.35) rot=(0,0,1;0rad)
  shape: bbox 5.992 x 6.8 x 4.3 mm, 28 faces (baked)
FEATURE [Part::Fillet] Fillet003002
  Base = -> Pad002001003004001003
  Edges = 4 edges r=0.8: [Edge33,Edge34,Edge69,Edge71]
FEATURE [Part::Fillet] Fillet003003
  Base = -> Fillet003002
  Edges = 16 edges r=0.6: [Edge37,Edge39,Edge41,Edge43,Edge44,Edge46,Edge49,Edge51,Edge53,Edge55,Edge57,Edge59,Edge60,Edge62,Edge65,Edge67]
FEATURE [Part::Fillet] Fillet003004  label="ears-block-3"
  Base = -> Fillet003003
  Edges = 1 edges r=0.2: [Edge36]
FEATURE [Part::Fillet] Fillet003005  label="ears-block-4"
  Base = -> Fillet003004
  Edges = 1 edges r=0.2: [Edge132]
FEATURE [App::DocumentObjectGroup] Group002  label="ears-src"
  Group = -> [Pad002001003004001002,Pocket014,Mirrored001,Pad002001003004001003,Fillet003004,Fillet003005]
FEATURE [Part::Feature] Fillet003005001  label="ears"
  Placement = pos=(0,0,28.9) rot=(0,0,1;0rad)
  shape: bbox 56.13 x 19.33 x 3.36 mm, 91 faces (baked)
FEATURE [Sketcher::SketchObject] Sketch039  label="shaft-body-sketch"
  FullyConstrained = false
  MapMode = 5
  sketch-geometry (1):
    g0: Circle CenterX=0 CenterY=0 CenterZ=0 NormalX=0 NormalY=0 NormalZ=1 AngleXU=0 Radius=3
  constraints (2):
    c: Coincident(g0,g-1)
    c: Radius(g0) = 3
FEATURE [PartDesign::Pad] Pad002001003004001006  label="shaft-body"
  AllowMultiFace = false
  Direction = (1,1,1)
  Length = 4.4
  Length2 = 100
  Profile = -> Sketch026
  Type = 0
FEATURE [Sketcher::SketchObject] Sketch040  label="shaft-body-2-sketch"
  FullyConstrained = false
  MapMode = 5
  Placement = pos=(0,0,4.4) rot=(0,0,1;0rad)
  Support = -> [Pad002001003004001006]
  sketch-geometry (1):
    g0: Circle CenterX=0 CenterY=0 CenterZ=0 NormalX=0 NormalY=0 NormalZ=1 AngleXU=0 Radius=1.1
  constraints (2):
    c: Coincident(g0,g-1)
    c: Radius(g0) = 1.1
FEATURE [PartDesign::Pocket] Pocket017  label="shaft-body-2"
  AllowMultiFace = false
  Length = 5
  Length2 = 100
  Profile = -> Sketch027
  Type = 1
FEATURE [PartDesign::Chamfer] Chamfer  label="shaft-body-3"
  Angle = 45
  Base = -> Pocket017 [Edge3]
  ChamferType = 0
  FlipDirection = false
  Size = 0.3
  Size2 = 1
  SupportTransform = false
FEATURE [Sketcher::SketchObject] Sketch041  label="shaft-tooth-sketch"
  FullyConstrained = false
  MapMode = 5
  Placement = pos=(0,0,4.4) rot=(0,0,1;0rad)
  Support = -> [Chamfer]
  sketch-geometry (3):
    g0: LineSegment StartX=-0.2 StartY=3 StartZ=0 EndX=0 EndY=2.8 EndZ=0
    g1: LineSegment StartX=0.2 StartY=3 StartZ=0 EndX=0 EndY=2.8 EndZ=0
    g2: LineSegment StartX=-0.2 StartY=3 StartZ=0 EndX=0.2 EndY=3 EndZ=0
  constraints (8):
    c: Horizontal(g2)
    c: Coincident(g2,g0)
    c: Coincident(g2,g1)
    c: Symmetric(g0,g1,g-2)
    c: DistanceX(g2) = 0.4
    c: Coincident(g0,g1)
    c: PointOnObject(g0,g-2)
    c: DistanceY(g0,g1) = 0.2
FEATURE [PartDesign::Pocket] Pocket018  label="shaft-tooth"
  AllowMultiFace = false
  Length = 3.4
  Length2 = 100
  Profile = -> Sketch028
  Type = 0
FEATURE [PartDesign::PolarPattern] PolarPattern001005  label="shaft-teeth"
  Angle = 360
  Axis = -> Sketch041 [N_Axis]
  Occurrences = 28
  Originals = -> [Pocket018]
FEATURE [PartDesign::Chamfer] Chamfer001  label="shaft-final"
  Angle = 45
  Base = -> PolarPattern001005 [Edge286]
  ChamferType = 0
  FlipDirection = false
  Size = 0.3
  Size2 = 1
  SupportTransform = false
FEATURE [App::DocumentObjectGroup] Group004  label="shaft-src"
  Group = -> [Pad002001003004001006,Pocket017,Chamfer,Pocket018,PolarPattern001005,Chamfer001]
FEATURE [Part::Feature] Chamfer001001  label="shaft"
  Placement = pos=(10.55,0,41.9) rot=(0,0,1;0rad)
  shape: bbox 6 x 6 x 4.4 mm, 90 faces (baked)
FEATURE [Part::Feature] Pad002001003004001007  label="bottom-side-gap"
  Placement = pos=(0,0,7.5) rot=(0,0,1;0rad)
  shape: bbox 44.1 x 24.8 x 0.4 mm, 14 faces (baked)
FEATURE [Part::Feature] Pad002001003004001007001  label="top-side-gap"
  Placement = pos=(0,0,28.5) rot=(0,0,1;0rad)
  shape: bbox 44.1 x 24.8 x 0.4 mm, 14 faces (baked)
FEATURE [Part::MultiFuse] Fusion007  label="side-gaps"
  Shapes = -> [Pad002001003004001007,Pad002001003004001007001]
FEATURE [PartDesign::Fillet] Fillet003005005  label="servo-body-final-3"
  Base = -> Pad002001003003 [Edge31,Edge38,Edge25,Edge32]
  Radius = 2
  SupportTransform = false
FEATURE [Part::Cut] Cut001002002  label="servo-body-final-4"
  Base = -> Fillet003005005
  Tool = -> Fusion007
FEATURE [Part::Fillet] Fillet003005006  label="servo-body-final-5"
  Base = -> Cut001002002
  Edges = 3 edges r=0.3: [Edge1,Edge3,Edge14]
FEATURE [App::DocumentObjectGroup] Group  label="Servo-body-src"
  Group = -> [Pad007,Pocket006,Mirrored,Pocket007,Pocket008,Pocket009,Pocket010,Pocket011,Pocket012,Pad008,Pad009,Cut002,Pad002001003003,Pad002001003004,Pad002001003004001007,Pad002001003004001007001,Fusion007,Fillet003005005,Cut001002002,Fillet003005006]
FEATURE [Part::Feature] Fillet003005006001  label="servo-body"
  shape: bbox 41.26 x 21.13 x 39.7 mm, 208 faces (baked)
FEATURE [Part::MultiFuse] Fusion008  label="servo-1"
  Shapes = -> [Fillet002,Fillet003005001,Fillet003001,Fillet003005006001]
FEATURE [Part::Feature] Cut001002003  label="bottom-screw-1"
  Placement = pos=(-18.1075,7.95754,34.2) rot=(1,0,0;3.14159rad)
  shape: bbox 3.75 x 3.75 x 33.19 mm, 18 faces (baked)
FEATURE [Part::Feature] Cut001002004  label="bottom-screw-2"
  Placement = pos=(18.1075,-7.95754,34.2) rot=(1,0,0;3.14159rad)
  shape: bbox 3.75 x 3.75 x 33.19 mm, 18 faces (baked)
FEATURE [Part::Feature] Cut001002005  label="bottom-screw-3"
  Placement = pos=(18.1075,7.95754,34.2) rot=(1,0,0;3.14159rad)
  shape: bbox 3.75 x 3.75 x 33.19 mm, 18 faces (baked)
FEATURE [Part::Feature] Cut001002006  label="bottom-screw-4"
  Placement = pos=(-18.1075,-7.95754,34.2) rot=(1,0,0;3.14159rad)
  shape: bbox 3.75 x 3.75 x 33.19 mm, 18 faces (baked)
FEATURE [Part::Compound] Compound  label="bottom-screws"
  Links = -> [Cut001002003,Cut001002006,Cut001002004,Cut001002005]
FEATURE [Part::Cylinder] Cylinder001  label="wire-center"
  Angle = 360
  AttacherType = Attacher::AttachEngine3D
  Height = 10
  Placement = pos=(1.5,0,0) rot=(0,1,0;1.5708rad)
  Radius = 0.65
FEATURE [Part::Feature] Cylinder002  label="wire-right"
  Placement = pos=(1.5,1.2,-8e-16) rot=(0,1,0;1.5708rad)
  shape: bbox 10 x 1.3 x 1.3 mm, 3 faces (baked)
FEATURE [Part::Feature] Cylinder003  label="wire-left"
  Placement = pos=(1.5,-1.2,0) rot=(0,1,0;1.5708rad)
  shape: bbox 10 x 1.3 x 1.3 mm, 3 faces (baked)
FEATURE [Part::MultiFuse] Fusion009  label="wires"
  Placement = pos=(20.55,0,6.35) rot=(0,0,1;0rad)
  Shapes = -> [Cylinder001,Cylinder002,Cylinder003]
FEATURE [Part::Compound] Compound001  label="Servo-SM-S4303R-assembly"
  Links = -> [Chamfer001001,Fusion008,Fusion009,Compound]
FEATURE [Part::Feature] Chamfer001002  label="shaft001"
  Placement = pos=(10.55,0,41.9) rot=(0,0,1;0rad)
  shape: bbox 6 x 6 x 4.4 mm, 90 faces (baked)
FEATURE [Part::Feature] Fusion010  label="wires001"
  Placement = pos=(20.55,0,6.35) rot=(0,0,1;0rad)
  shape: bbox 10 x 3.7 x 1.3 mm, 9 faces (baked)
FEATURE [Part::Feature] Fusion011  label="servo-002"
  shape: bbox 56.13 x 21.13 x 45.15 mm, 371 faces (baked)
FEATURE [Part::Feature] Compound003  label="bottom-screws001"
  shape: bbox 39.97 x 19.67 x 33.19 mm, 72 faces, 4 solids (baked)
FEATURE [Part::Compound] Compound002  label="Servo-SM-S4303R-compound"
  Links = -> [Compound003,Fusion011,Fusion010,Chamfer001002]
FEATURE [Part::Compound] Compound004  label="servo1"
  Placement = pos=(-54,186.811,-8.86518) rot=(-0.57735,-0.57735,0.57735;2.0944rad)
FEATURE [Sketcher::SketchObject] Sketch042  label="servo-body-sketch001"
  FullyConstrained = false
  MapMode = 5
  Placement = pos=(0,0,0) rot=(1,0,0;1.5708rad)
  sketch-geometry (5):
    g0: LineSegment StartX=20.55 StartY=39.6 StartZ=0 EndX=20.55 EndY=0 EndZ=0
    g1: LineSegment StartX=20.55 StartY=0 StartZ=0 EndX=-20.55 EndY=0 EndZ=0
    g2: LineSegment StartX=-20.55 StartY=0 StartZ=0 EndX=-20.55 EndY=34.9 EndZ=0
    g3: LineSegment StartX=-20.55 StartY=34.9 StartZ=0 EndX=-12.25 EndY=39.6 EndZ=0
    g4: LineSegment StartX=-12.25 StartY=39.6 StartZ=0 EndX=20.55 EndY=39.6 EndZ=0
  constraints (15):
    c: Coincident(g0,g1)
    c: Coincident(g1,g2)
    c: Horizontal(g1)
    c: Vertical(g0)
    c: Vertical(g2)
    c: Symmetric(g1,g0,g-2)
    c: PointOnObject(g1,g-1)
    c: DistanceX(g1) = -41.1
    c: DistanceY(g0) = -39.6
    c: Coincident(g3,g2)
    c: Horizontal(g4)
    c: Coincident(g4,g0)
    c: Coincident(g3,g4)
    c: DistanceY(g2) = 34.9
    c: DistanceX(g4) = 32.8
FEATURE [PartDesign::Pad] Pad002001003004001007002  label="servo-body-002"
  AllowMultiFace = false
  Direction = (1,1,1)
  Length = 20.8
  Length2 = 100
  Midplane = true
  Placement = pos=(0,0,0) rot=(1,0,0;1.5708rad)
  Profile = -> Sketch
  Type = 0
FEATURE [Sketcher::SketchObject] Sketch043  label="bottom-master-sketch001"
  ExternalGeometry = -> [Pad002001003004001007002]
  FullyConstrained = false
  MapMode = 5
  Placement = pos=(0,0,0) rot=(1,0,0;3.14159rad)
  Support = -> [Pad002001003004001007002]
  sketch-geometry (15):
    g0: LineSegment StartX=-20.55 StartY=10.4 StartZ=0 EndX=-18.2075 EndY=8.05754 EndZ=0
    g1: Circle CenterX=-18.2075 CenterY=8.05754 CenterZ=0 NormalX=0 NormalY=0 NormalZ=1 AngleXU=0 Radius=1.05
    g2: GeomPoint X=-18.95 Y=8.8 Z=0
    g3: LineSegment StartX=-18.2075 StartY=8.05754 StartZ=0 EndX=-18.2075 EndY=6 EndZ=0
    g4: LineSegment StartX=-18.2075 StartY=8.05754 StartZ=0 EndX=-16.15 EndY=8.05754 EndZ=0
    g5: LineSegment StartX=-20.55 StartY=6 StartZ=0 EndX=-20.55 EndY=10.4 EndZ=0
    g6: LineSegment StartX=-20.55 StartY=10.4 StartZ=0 EndX=-16.15 EndY=10.4 EndZ=0
    g7: LineSegment StartX=-16.15 StartY=10.4 StartZ=0 EndX=-16.15 EndY=8.05754 EndZ=0
    g8: ArcOfCircle CenterX=-18.2075 CenterY=8.05754 CenterZ=0 NormalX=0 NormalY=0 NormalZ=1 AngleXU=0 Radius=2.05754 StartAngle=4.71239 EndAngle=6.28319
    g9: LineSegment StartX=-20.55 StartY=6 StartZ=0 EndX=-18.2075 EndY=6 EndZ=0
    g10: ArcOfCircle CenterX=-18.2075 CenterY=-8.05754 CenterZ=0 NormalX=0 NormalY=0 NormalZ=1 AngleXU=0 Radius=2.05754 StartAngle=5.46325e-06 EndAngle=1.5708
    g11: LineSegment StartX=-18.2075 StartY=-6 StartZ=0 EndX=-20.55 EndY=-6 EndZ=0
    g12: LineSegment StartX=-20.55 StartY=-6 StartZ=0 EndX=-20.55 EndY=-10.4 EndZ=0
    g13: LineSegment StartX=-20.55 StartY=-10.4 StartZ=0 EndX=-16.15 EndY=-10.4 EndZ=0
    g14: LineSegment StartX=-16.15 StartY=-10.4 StartZ=0 EndX=-16.15 EndY=-8.05753 EndZ=0
  constraints (40):
    c: Coincident(g0,g-4)
    c: Angle(g-4,g0) = 0.785398
    c: Radius(g1) = 1.05
    c: Coincident(g1,g0)
    c: PointOnObject(g2,g0)
    c: PointOnObject(g2,g1)
    c: DistanceX(g2,g0) = -1.6
    c: Vertical(g3)
    c: Coincident(g3,g0)
    c: Coincident(g0,g4)
    c: Horizontal(g4)
    c: Equal(g3,g4)
    c: Coincident(g5,g6)
    c: Vertical(g5)
    c: Horizontal(g6)
    c: Vertical(g7)
    c: Coincident(g7,g6)
    c: Coincident(g7,g4)
    c: Coincident(g5,g0)
    c: Coincident(g8,g0)
    c: Coincident(g8,g4)
    c: Coincident(g3,g8)
    c: Coincident(g9,g5)
    c: Coincident(g9,g3)
    c: Horizontal(g9)
    c: DistanceY(g0,g5) = -4.4
    c: Horizontal(g11)
    c: Coincident(g11,g12)
    c: Vertical(g12)
    c: Coincident(g12,g13)
    c: Horizontal(g13)
    c: Coincident(g13,g14)
    c: Vertical(g14)
    c: Coincident(g12,g-4)
    c: Symmetric(g10,g0,g-1)
    c: Symmetric(g13,g6,g-1)
    c: Symmetric(g11,g3,g-1)
    c: Equal(g10,g8)
    c: Coincident(g10,g11)
    c: Coincident(g10,g14)
FEATURE [PartDesign::Pocket] Pocket019  label="bottom-master001"
  AllowMultiFace = false
  Length = 1.8
  Length2 = 100
  Placement = pos=(0,0,0) rot=(1,0,0;1.5708rad)
  Profile = -> Sketch001
  Type = 0
FEATURE [PartDesign::Mirrored] Mirrored002  label="bottom-003"
  MirrorPlane = -> Sketch043 [V_Axis]
  Originals = -> [Pocket019]
  Placement = pos=(0,0,0) rot=(1,0,0;1.5708rad)
FEATURE [Sketcher::SketchObject] Sketch044  label="bottom-2-sketch001"
  ExternalGeometry = -> [Mirrored002]
  FullyConstrained = false
  MapMode = 5
  Placement = pos=(0,8e-16,1.8) rot=(1,0,0;3.14159rad)
  Support = -> [Mirrored002]
  sketch-geometry (10):
    g0: LineSegment StartX=-20.55 StartY=10.4 StartZ=0 EndX=-18.85 EndY=8.7 EndZ=0
    g1: Circle CenterX=-18.1075 CenterY=7.95754 CenterZ=0 NormalX=0 NormalY=0 NormalZ=1 AngleXU=0 Radius=1.05
    g2: Circle CenterX=-18.1075 CenterY=7.95754 CenterZ=0 NormalX=0 NormalY=0 NormalZ=1 AngleXU=0 Radius=1.9
    g3: Circle CenterX=-18.1075 CenterY=-7.95754 CenterZ=0 NormalX=0 NormalY=0 NormalZ=1 AngleXU=0 Radius=1.9
    g4: Circle CenterX=18.1075 CenterY=7.95754 CenterZ=0 NormalX=0 NormalY=0 NormalZ=1 AngleXU=0 Radius=1.9
    g5: Circle CenterX=18.1075 CenterY=-7.95754 CenterZ=0 NormalX=0 NormalY=0 NormalZ=1 AngleXU=0 Radius=1.9
    g6: LineSegment StartX=-18.1075 StartY=7.95754 StartZ=0 EndX=18.1075 EndY=7.95754 EndZ=0
    g7: LineSegment StartX=18.1075 StartY=7.95754 StartZ=0 EndX=18.1075 EndY=-7.95754 EndZ=0
    g8: LineSegment StartX=18.1075 StartY=-7.95754 StartZ=0 EndX=-18.1075 EndY=-7.95754 EndZ=0
    g9: LineSegment StartX=-18.1075 StartY=-7.95754 StartZ=0 EndX=-18.1075 EndY=7.95754 EndZ=0
  constraints (24):
    c: Angle(g0,g-3) = 0.785398
    c: Coincident(g0,g-3)
    c: Radius(g1) = 1.05
    c: PointOnObject(g1,g0)
    c: PointOnObject(g0,g1)
    c: DistanceX(g0,g0) = 1.7
    c: Coincident(g2,g1)
    c: Radius(g2) = 1.9
    c: Equal(g3,g2)
    c: Equal(g2,g4)
    c: Equal(g4,g5)
    c: Coincident(g6,g7)
    c: Coincident(g7,g8)
    c: Coincident(g8,g9)
    c: Coincident(g9,g6)
    c: Horizontal(g6)
    c: Horizontal(g8)
    c: Vertical(g7)
    c: Vertical(g9)
    c: Symmetric(g6,g7,g-1)
    c: Coincident(g6,g1)
    c: Coincident(g3,g8)
    c: Coincident(g6,g4)
    c: Coincident(g5,g7)
FEATURE [PartDesign::Pocket] Pocket020  label="bottom-004"
  AllowMultiFace = false
  Length = 0.6
  Length2 = 100
  Placement = pos=(0,0,0) rot=(1,0,0;1.5708rad)
  Profile = -> Sketch002
  Type = 0
FEATURE [Sketcher::SketchObject] Sketch045  label="bottom-drills-sketch001"
  ExternalGeometry = -> [Pocket020]
  FullyConstrained = false
  MapMode = 5
  Placement = pos=(0,1.3e-15,2.4) rot=(1,0,0;3.14159rad)
  Support = -> [Pocket020]
  sketch-geometry (8):
    g0: Circle CenterX=-18.1075 CenterY=7.95754 CenterZ=0 NormalX=0 NormalY=0 NormalZ=1 AngleXU=0 Radius=1.05
    g1: LineSegment StartX=-18.1075 StartY=7.95754 StartZ=0 EndX=18.1075 EndY=7.95754 EndZ=0
    g2: LineSegment StartX=18.1075 StartY=7.95754 StartZ=0 EndX=18.1075 EndY=-7.95754 EndZ=0
    g3: LineSegment StartX=18.1075 StartY=-7.95754 StartZ=0 EndX=-18.1075 EndY=-7.95754 EndZ=0
    g4: LineSegment StartX=-18.1075 StartY=-7.95754 StartZ=0 EndX=-18.1075 EndY=7.95754 EndZ=0
    g5: Circle CenterX=-18.1075 CenterY=-7.95754 CenterZ=0 NormalX=0 NormalY=0 NormalZ=1 AngleXU=0 Radius=1.05
    g6: Circle CenterX=18.1075 CenterY=7.95754 CenterZ=0 NormalX=0 NormalY=0 NormalZ=1 AngleXU=0 Radius=1.05
    g7: Circle CenterX=18.1075 CenterY=-7.95754 CenterZ=0 NormalX=0 NormalY=0 NormalZ=1 AngleXU=0 Radius=1.05
  constraints (18):
    c: Coincident(g0,g-3)
    c: Radius(g0) = 1.05
    c: Coincident(g1,g2)
    c: Coincident(g2,g3)
    c: Coincident(g3,g4)
    c: Coincident(g4,g1)
    c: Horizontal(g1)
    c: Horizontal(g3)
    c: Vertical(g2)
    c: Vertical(g4)
    c: Symmetric(g1,g2,g-1)
    c: Coincident(g1,g0)
    c: Equal(g6,g5)
    c: Equal(g5,g7)
    c: Equal(g7,g0)
    c: Coincident(g3,g5)
    c: Coincident(g6,g1)
    c: Coincident(g7,g2)
FEATURE [PartDesign::Pocket] Pocket021  label="bottom-drills001"
  AllowMultiFace = false
  Length = 32
  Length2 = 100
  Placement = pos=(0,0,0) rot=(1,0,0;1.5708rad)
  Profile = -> Sketch003
  Type = 0
FEATURE [Sketcher::SketchObject] Sketch046  label="top-drills-1-sketch001"
  ExternalGeometry = -> [Pocket021]
  FullyConstrained = false
  MapMode = 5
  Placement = pos=(0,8.7e-15,39.6) rot=(0,0,1;3.14159rad)
  Support = -> [Pocket021]
  sketch-geometry (9):
    g0: LineSegment StartX=-17.65 StartY=7.5 StartZ=0 EndX=-0.05 EndY=7.5 EndZ=0
    g1: LineSegment StartX=-0.05 StartY=7.5 StartZ=0 EndX=-0.05 EndY=-7.5 EndZ=0
    g2: LineSegment StartX=-0.05 StartY=-7.5 StartZ=0 EndX=-17.65 EndY=-7.5 EndZ=0
    g3: LineSegment StartX=-17.65 StartY=-7.5 StartZ=0 EndX=-17.65 EndY=7.5 EndZ=0
    g4: Circle CenterX=-0.05 CenterY=-7.5 CenterZ=0 NormalX=0 NormalY=0 NormalZ=1 AngleXU=0 Radius=1.25
    g5: Circle CenterX=-17.65 CenterY=-7.5 CenterZ=0 NormalX=0 NormalY=0 NormalZ=1 AngleXU=0 Radius=1.25
    g6: Circle CenterX=-0.05 CenterY=7.5 CenterZ=0 NormalX=0 NormalY=0 NormalZ=1 AngleXU=0 Radius=1.25
    g7: Circle CenterX=-17.65 CenterY=7.5 CenterZ=0 NormalX=0 NormalY=0 NormalZ=1 AngleXU=0 Radius=1.25
    g8: LineSegment StartX=-20.55 StartY=-10.4 StartZ=0 EndX=-17.65 EndY=-7.5 EndZ=0
  constraints (22):
    c: Coincident(g0,g1)
    c: Coincident(g1,g2)
    c: Coincident(g2,g3)
    c: Coincident(g3,g0)
    c: Horizontal(g0)
    c: Horizontal(g2)
    c: Vertical(g1)
    c: Vertical(g3)
    c: Symmetric(g2,g0,g-1)
    c: Equal(g4,g7)
    c: Equal(g7,g6)
    c: Equal(g6,g5)
    c: Radius(g4) = 1.25
    c: Coincident(g4,g1)
    c: Coincident(g6,g0)
    c: Coincident(g5,g2)
    c: Coincident(g7,g0)
    c: DistanceY(g-1,g1) = -7.5
    c: DistanceX(g2) = -17.6
    c: Coincident(g8,g-3)
    c: Coincident(g8,g2)
    c: Angle(g-3,g8) = 0.785398
FEATURE [PartDesign::Pocket] Pocket022  label="top-drills-002"
  AllowMultiFace = false
  Length = 0.2
  Length2 = 100
  Placement = pos=(0,0,0) rot=(1,0,0;1.5708rad)
  Profile = -> Sketch004
  Type = 0
FEATURE [Sketcher::SketchObject] Sketch047  label="potentiometer-1-sketch001"
  FullyConstrained = false
  MapMode = 5
  Placement = pos=(20.55,0,0) rot=(0.707107,0,0.707107;3.14159rad)
  Support = -> [Pocket022]
  sketch-geometry (2):
    g0: Circle CenterX=14.175 CenterY=0 CenterZ=0 NormalX=0 NormalY=0 NormalZ=1 AngleXU=0 Radius=1.925
    g1: GeomPoint X=16.1 Y=0 Z=0
  constraints (5):
    c: PointOnObject(g0,g-1)
    c: Radius(g0) = 1.925
    c: PointOnObject(g1,g-1)
    c: PointOnObject(g1,g0)
    c: DistanceX(g-1,g1) = 16.1
FEATURE [PartDesign::Pocket] Pocket023  label="potentiometer-hole001"
  AllowMultiFace = false
  Length = 2.2
  Length2 = 100
  Placement = pos=(0,0,0) rot=(1,0,0;1.5708rad)
  Profile = -> Sketch006
  Type = 0
FEATURE [Sketcher::SketchObject] Sketch048  label="potentiometer-cross-sketch001"
  ExternalGeometry = -> [Pocket023]
  FullyConstrained = false
  MapMode = 5
  Placement = pos=(18.35,0,0) rot=(0.707107,0,0.707107;3.14159rad)
  Support = -> [Pocket023]
  sketch-geometry (12):
    g0: LineSegment StartX=13.675 StartY=1.65 StartZ=0 EndX=14.675 EndY=1.65 EndZ=0
    g1: LineSegment StartX=14.675 StartY=1.65 StartZ=0 EndX=14.675 EndY=0.5 EndZ=0
    g2: LineSegment StartX=14.675 StartY=-1.65 StartZ=0 EndX=13.675 EndY=-1.65 EndZ=0
    g3: LineSegment StartX=13.675 StartY=-1.65 StartZ=0 EndX=13.675 EndY=-0.5 EndZ=0
    g4: LineSegment StartX=12.525 StartY=0.5 StartZ=0 EndX=13.675 EndY=0.5 EndZ=0
    g5: LineSegment StartX=15.825 StartY=0.5 StartZ=0 EndX=15.825 EndY=-0.5 EndZ=0
    g6: LineSegment StartX=15.825 StartY=-0.5 StartZ=0 EndX=14.675 EndY=-0.5 EndZ=0
    g7: LineSegment StartX=12.525 StartY=-0.5 StartZ=0 EndX=12.525 EndY=0.5 EndZ=0
    g8: LineSegment StartX=14.675 StartY=0.5 StartZ=0 EndX=15.825 EndY=0.5 EndZ=0
    g9: LineSegment StartX=13.675 StartY=-0.5 StartZ=0 EndX=12.525 EndY=-0.5 EndZ=0
    g10: LineSegment StartX=13.675 StartY=0.5 StartZ=0 EndX=13.675 EndY=1.65 EndZ=0
    g11: LineSegment StartX=14.675 StartY=-0.5 StartZ=0 EndX=14.675 EndY=-1.65 EndZ=0
  constraints (30):
    c: Coincident(g0,g1)
    c: Coincident(g11,g2)
    c: Coincident(g2,g3)
    c: Coincident(g10,g0)
    c: Horizontal(g0)
    c: Horizontal(g2)
    c: Vertical(g1)
    c: Vertical(g3)
    c: Coincident(g8,g5)
    c: Coincident(g5,g6)
    c: Coincident(g9,g7)
    c: Coincident(g7,g4)
    c: Horizontal(g4)
    c: Horizontal(g6)
    c: Vertical(g5)
    c: Vertical(g7)
    c: Symmetric(g4,g5,g-3)
    c: Symmetric(g0,g11,g-3)
    c: Tangent(g4,g8)
    c: Tangent(g6,g9)
    c: Coincident(g3,g9)
    c: Coincident(g10,g4)
    c: Tangent(g3,g10)
    c: Coincident(g1,g8)
    c: Coincident(g11,g6)
    c: Tangent(g1,g11)
    c: Equal(g4,g10)
    c: Equal(g7,g0)
    c: DistanceX(g5,g4) = -3.3
    c: DistanceY(g5) = -1
FEATURE [PartDesign::Pocket] Pocket024  label="potentiometer-cross001"
  AllowMultiFace = false
  Length = 1
  Length2 = 100
  Placement = pos=(0,0,0) rot=(1,0,0;1.5708rad)
  Profile = -> Sketch007
  Type = 0
FEATURE [Sketcher::SketchObject] Sketch049  label="label-plate-sketch001"
  ExternalGeometry = -> [Pocket024]
  FullyConstrained = false
  MapMode = 5
  Placement = pos=(-19.9538,7.7e-15,35.2376) rot=(-0.254782,0,0.966998;3.14159rad)
  Support = -> [Pocket024]
  sketch-geometry (8):
    g0: LineSegment StartX=-7.65321 StartY=5.15 StartZ=0 EndX=-1.15321 EndY=5.15 EndZ=0
    g1: LineSegment StartX=-0.953214 StartY=4.95 StartZ=0 EndX=-0.953214 EndY=-4.95 EndZ=0
    g2: LineSegment StartX=-1.15321 StartY=-5.15 StartZ=0 EndX=-7.65321 EndY=-5.15 EndZ=0
    g3: LineSegment StartX=-7.85321 StartY=-4.95 StartZ=0 EndX=-7.85321 EndY=4.95 EndZ=0
    g4: ArcOfCircle CenterX=-7.65321 CenterY=4.95 CenterZ=0 NormalX=0 NormalY=0 NormalZ=1 AngleXU=0 Radius=0.2 StartAngle=1.5708 EndAngle=3.14159
    g5: ArcOfCircle CenterX=-1.15321 CenterY=4.95 CenterZ=0 NormalX=0 NormalY=0 NormalZ=1 AngleXU=0 Radius=0.2 StartAngle=0 EndAngle=1.5708
    g6: ArcOfCircle CenterX=-1.15321 CenterY=-4.95 CenterZ=0 NormalX=0 NormalY=0 NormalZ=1 AngleXU=0 Radius=0.2 StartAngle=4.71239 EndAngle=6.28319
    g7: ArcOfCircle CenterX=-7.65321 CenterY=-4.95 CenterZ=0 NormalX=0 NormalY=0 NormalZ=1 AngleXU=0 Radius=0.2 StartAngle=3.14159 EndAngle=4.71239
  constraints (20):
    c: Horizontal(g0)
    c: Horizontal(g2)
    c: Vertical(g1)
    c: Vertical(g3)
    c: Tangent(g0,g4)
    c: Tangent(g3,g4)
    c: Tangent(g0,g5)
    c: Tangent(g1,g5)
    c: Tangent(g1,g6)
    c: Tangent(g2,g6)
    c: Tangent(g2,g7)
    c: Tangent(g3,g7)
    c: Equal(g4,g5)
    c: Equal(g5,g7)
    c: Equal(g7,g6)
    c: Symmetric(g5,g6,g-1)
    c: DistanceY(g0,g2) = -10.3
    c: DistanceX(g3,g1) = 6.9
    c: Radius(g4) = 0.2
    c: DistanceX(g3,g-3) = -1
FEATURE [PartDesign::Pocket] Pocket025  label="Label-plate001"
  AllowMultiFace = false
  Length = 0.1
  Length2 = 100
  Placement = pos=(0,0,0) rot=(1,0,0;1.5708rad)
  Profile = -> Sketch008
  Type = 0
FEATURE [Sketcher::SketchObject] Sketch050  label="top-left-2-drills-sketch001"
  FullyConstrained = false
  MapMode = 5
  Placement = pos=(0,8.7e-15,39.6) rot=(0,0,1;3.14159rad)
  Support = -> [Pocket025]
  sketch-geometry (4):
    g0: Circle CenterX=18 CenterY=7.5 CenterZ=0 NormalX=0 NormalY=0 NormalZ=1 AngleXU=0 Radius=1.25
    g1: Circle CenterX=18 CenterY=-7.5 CenterZ=0 NormalX=0 NormalY=0 NormalZ=1 AngleXU=0 Radius=1.25
    g2: LineSegment StartX=18 StartY=7.5 StartZ=0 EndX=18 EndY=0 EndZ=0
    g3: LineSegment StartX=18 StartY=7.5 StartZ=0 EndX=19.25 EndY=7.5 EndZ=0
  constraints (10):
    c: Radius(g0) = 1.25
    c: Equal(g1,g0)
    c: Symmetric(g0,g1,g-1)
    c: Coincident(g2,g0)
    c: Vertical(g2)
    c: PointOnObject(g2,g-1)
    c: DistanceY(g2) = -7.5
    c: Horizontal(g3)
    c: Coincident(g3,g0)
    c: PointOnObject(g3,g0)
FEATURE [PartDesign::Pocket] Pocket026  label="top-left-2-drills001"
  AllowMultiFace = false
  Length = 4.1
  Length2 = 100
  Placement = pos=(0,0,0) rot=(1,0,0;1.5708rad)
  Profile = -> Sketch009
  Type = 0
FEATURE [Sketcher::SketchObject] Sketch051  label="top-drills-cross-1-sketch001"
  FullyConstrained = false
  MapMode = 5
  sketch-geometry (13):
    g0: Circle CenterX=0 CenterY=0 CenterZ=0 NormalX=0 NormalY=0 NormalZ=1 AngleXU=0 Radius=1.25
    g1: LineSegment StartX=-0.15 StartY=0.6 StartZ=0 EndX=0.15 EndY=0.6 EndZ=0
    g2: LineSegment StartX=0.15 StartY=0.6 StartZ=0 EndX=0.15 EndY=0.15 EndZ=0
    g3: LineSegment StartX=0.15 StartY=-0.6 StartZ=0 EndX=-0.15 EndY=-0.6 EndZ=0
    g4: LineSegment StartX=-0.15 StartY=-0.6 StartZ=0 EndX=-0.15 EndY=-0.15 EndZ=0
    g5: LineSegment StartX=-0.6 StartY=0.15 StartZ=0 EndX=-0.15 EndY=0.15 EndZ=0
    g6: LineSegment StartX=0.6 StartY=0.15 StartZ=0 EndX=0.6 EndY=-0.15 EndZ=0
    g7: LineSegment StartX=0.6 StartY=-0.15 StartZ=0 EndX=0.15 EndY=-0.15 EndZ=0
    g8: LineSegment StartX=-0.6 StartY=-0.15 StartZ=0 EndX=-0.6 EndY=0.15 EndZ=0
    g9: LineSegment StartX=0.15 StartY=0.15 StartZ=0 EndX=0.6 EndY=0.15 EndZ=0
    g10: LineSegment StartX=-0.15 StartY=-0.15 StartZ=0 EndX=-0.6 EndY=-0.15 EndZ=0
    g11: LineSegment StartX=-0.15 StartY=0.15 StartZ=0 EndX=-0.15 EndY=0.6 EndZ=0
    g12: LineSegment StartX=0.15 StartY=-0.15 StartZ=0 EndX=0.15 EndY=-0.6 EndZ=0
  constraints (32):
    c: Coincident(g0,g-1)
    c: Radius(g0) = 1.25
    c: Coincident(g1,g2)
    c: Coincident(g12,g3)
    c: Coincident(g3,g4)
    c: Coincident(g11,g1)
    c: Horizontal(g1)
    c: Horizontal(g3)
    c: Vertical(g2)
    c: Vertical(g4)
    c: Symmetric(g1,g12,g-1)
    c: Coincident(g9,g6)
    c: Coincident(g6,g7)
    c: Coincident(g10,g8)
    c: Coincident(g8,g5)
    c: Horizontal(g5)
    c: Horizontal(g7)
    c: Vertical(g6)
    c: Vertical(g8)
    c: Symmetric(g5,g6,g-1)
    c: Tangent(g5,g9)
    c: Tangent(g7,g10)
    c: Coincident(g4,g10)
    c: Coincident(g11,g5)
    c: Tangent(g4,g11)
    c: Coincident(g2,g9)
    c: Coincident(g12,g7)
    c: Tangent(g2,g12)
    c: Equal(g5,g11)
    c: Equal(g8,g1)
    c: DistanceX(g5,g6) = 1.2
    c: DistanceX(g1) = 0.3
FEATURE [PartDesign::Pad] Pad002001003004001007003  label="top-drills-cross-007"
  AllowMultiFace = false
  Direction = (1,1,1)
  Length = 10
  Length2 = 100
  Profile = -> Sketch010
  Type = 0
FEATURE [Sketcher::SketchObject] Sketch052  label="top-drills-cross-2-sketch001"
  FullyConstrained = false
  MapMode = 5
  Placement = pos=(0,0,10) rot=(0,0,1;0rad)
  Support = -> [Pad002001003004001007003]
  sketch-geometry (1):
    g0: Circle CenterX=0 CenterY=0 CenterZ=0 NormalX=0 NormalY=0 NormalZ=1 AngleXU=0 Radius=1.25
  constraints (2):
    c: Coincident(g0,g-1)
    c: Radius(g0) = 1.25
FEATURE [PartDesign::Pad] Pad002001003004001007004  label="top-drills-cross-008"
  AllowMultiFace = false
  Direction = (1,1,1)
  Length = 1
  Length2 = 100
  Profile = -> Sketch011
  Type = 0
FEATURE [Part::Feature] Pad002001003004001007005  label="top-drills-cross-009"
  Placement = pos=(17.65,7.5,39.2) rot=(0,0,1;0rad)
  shape: bbox 2.5 x 2.5 x 11 mm, 16 faces (baked)
FEATURE [Part::Feature] Pad002001003004001007006  label="top-drills-cross-010"
  Placement = pos=(17.65,-7.5,39.2) rot=(0,0,1;0rad)
  shape: bbox 2.5 x 2.5 x 11 mm, 16 faces (baked)
FEATURE [Part::Feature] Pad002001003004001007007  label="top-drills-cross-011"
  Placement = pos=(0.05,7.5,39.2) rot=(0,0,1;0rad)
  shape: bbox 2.5 x 2.5 x 11 mm, 16 faces (baked)
FEATURE [Part::Feature] Pad002001003004001007008  label="top-drills-cross-012"
  Placement = pos=(0.05,-7.5,39.2) rot=(0,0,1;0rad)
  shape: bbox 2.5 x 2.5 x 11 mm, 16 faces (baked)
FEATURE [Part::Feature] Pad002001003004001007009  label="top-drills-cross-013"
  Placement = pos=(-18,7.5,35.2) rot=(0,0,1;0rad)
  shape: bbox 2.5 x 2.5 x 11 mm, 16 faces (baked)
FEATURE [Part::Feature] Pad002001003004001007010  label="top-drills-cross-014"
  Placement = pos=(-18,-7.5,35.2) rot=(0,0,1;0rad)
  shape: bbox 2.5 x 2.5 x 11 mm, 16 faces (baked)
FEATURE [Part::MultiFuse] Fusion012  label="union-of-top-crosses001"
  Shapes = -> [Pad002001003004001007005,Pad002001003004001007009,Pad002001003004001007010,Pad002001003004001007007,Pad002001003004001007008,Pad002001003004001007006]
FEATURE [Part::Cut] Cut001002007  label="servo-body-final-006"
  Base = -> Pocket026
  Tool = -> Fusion012
FEATURE [Sketcher::SketchObject] Sketch053  label="shaft-anchor-sketch001"
  ExternalGeometry = -> [Cut001002007]
  FullyConstrained = false
  MapMode = 5
  Placement = pos=(0,8.7e-15,39.6) rot=(0,0,1;0rad)
  Support = -> [Cut001002007]
  sketch-geometry (2):
    g0: Circle CenterX=10.55 CenterY=0 CenterZ=0 NormalX=0 NormalY=0 NormalZ=1 AngleXU=0 Radius=3
    g1: LineSegment StartX=13.55 StartY=0 StartZ=0 EndX=20.55 EndY=0 EndZ=0
  constraints (7):
    c: PointOnObject(g0,g-1)
    c: Radius(g0) = 3
    c: Horizontal(g1)
    c: PointOnObject(g1,g-3)
    c: PointOnObject(g1,g-1)
    c: PointOnObject(g1,g0)
    c: DistanceX(g1) = 7
FEATURE [PartDesign::Pad] Pad002001003004001007011  label="servo-body-final-007"
  AllowMultiFace = false
  Direction = (1,1,1)
  Length = 0.1
  Length2 = 100
  Profile = -> Sketch012
  Type = 0
FEATURE [Sketcher::SketchObject] Sketch054  label="side-gap-sketch001"
  FullyConstrained = false
  MapMode = 5
  sketch-geometry (25):
    g0: LineSegment StartX=-18.05 StartY=10.4 StartZ=0 EndX=18.05 EndY=10.4 EndZ=0
    g1: LineSegment StartX=20.05 StartY=8.4 StartZ=0 EndX=20.05 EndY=-8.4 EndZ=0
    g2: LineSegment StartX=18.05 StartY=-10.4 StartZ=0 EndX=-18.05 EndY=-10.4 EndZ=0
    g3: LineSegment StartX=-20.05 StartY=-8.4 StartZ=0 EndX=-20.05 EndY=8.4 EndZ=0
    g4: LineSegment StartX=-22.05 StartY=12.4 StartZ=0 EndX=-18.05 EndY=8.4 EndZ=0
    g5: LineSegment StartX=-18.05 StartY=10.1 StartZ=0 EndX=18.05 EndY=10.1 EndZ=0
    g6: LineSegment StartX=19.75 StartY=8.4 StartZ=0 EndX=19.75 EndY=-8.4 EndZ=0
    g7: LineSegment StartX=18.05 StartY=-10.1 StartZ=0 EndX=-18.05 EndY=-10.1 EndZ=0
    g8: LineSegment StartX=-19.75 StartY=-8.4 StartZ=0 EndX=-19.75 EndY=8.4 EndZ=0
    g9: LineSegment StartX=-22.05 StartY=12.4 StartZ=0 EndX=22.05 EndY=12.4 EndZ=0
    g10: LineSegment StartX=22.05 StartY=12.4 StartZ=0 EndX=22.05 EndY=-12.4 EndZ=0
    g11: LineSegment StartX=22.05 StartY=-12.4 StartZ=0 EndX=-22.05 EndY=-12.4 EndZ=0
    g12: LineSegment StartX=-22.05 StartY=-12.4 StartZ=0 EndX=-22.05 EndY=12.4 EndZ=0
    g13: ArcOfCircle CenterX=18.05 CenterY=-8.4 CenterZ=0 NormalX=0 NormalY=0 NormalZ=1 AngleXU=0 Radius=2 StartAngle=4.71239 EndAngle=6.28319
    g14: ArcOfCircle CenterX=18.05 CenterY=8.4 CenterZ=0 NormalX=0 NormalY=0 NormalZ=1 AngleXU=0 Radius=2 StartAngle=0 EndAngle=1.5708
    g15: ArcOfCircle CenterX=-18.05 CenterY=8.4 CenterZ=0 NormalX=0 NormalY=0 NormalZ=1 AngleXU=0 Radius=2 StartAngle=1.5708 EndAngle=3.14159
    g16: ArcOfCircle CenterX=-18.05 CenterY=-8.4 CenterZ=0 NormalX=0 NormalY=0 NormalZ=1 AngleXU=0 Radius=2 StartAngle=3.14159 EndAngle=4.71239
    g17: LineSegment StartX=-18.05 StartY=8.4 StartZ=0 EndX=18.05 EndY=8.4 EndZ=0
    g18: LineSegment StartX=18.05 StartY=8.4 StartZ=0 EndX=18.05 EndY=-8.4 EndZ=0
    g19: LineSegment StartX=18.05 StartY=-8.4 StartZ=0 EndX=-18.05 EndY=-8.4 EndZ=0
    g20: LineSegment StartX=-18.05 StartY=-8.4 StartZ=0 EndX=-18.05 EndY=8.4 EndZ=0
    g21: ArcOfCircle CenterX=-18.05 CenterY=8.4 CenterZ=0 NormalX=0 NormalY=0 NormalZ=1 AngleXU=0 Radius=1.7 StartAngle=1.5708 EndAngle=3.14159
    g22: ArcOfCircle CenterX=-18.05 CenterY=-8.4 CenterZ=0 NormalX=0 NormalY=0 NormalZ=1 AngleXU=0 Radius=1.7 StartAngle=3.14159 EndAngle=4.71239
    g23: ArcOfCircle CenterX=18.05 CenterY=-8.4 CenterZ=0 NormalX=0 NormalY=0 NormalZ=1 AngleXU=0 Radius=1.7 StartAngle=4.71239 EndAngle=6.28319
    g24: ArcOfCircle CenterX=18.05 CenterY=8.4 CenterZ=0 NormalX=0 NormalY=0 NormalZ=1 AngleXU=0 Radius=1.7 StartAngle=0 EndAngle=1.5708
  constraints (62):
    c: Horizontal(g0)
    c: Horizontal(g2)
    c: Vertical(g1)
    c: Vertical(g3)
    c: Angle(g-1,g4) = 2.35619
    c: Horizontal(g5)
    c: Horizontal(g7)
    c: Vertical(g6)
    c: Vertical(g8)
    c: Coincident(g9,g10)
    c: Coincident(g10,g11)
    c: Coincident(g11,g12)
    c: Coincident(g12,g9)
    c: Horizontal(g9)
    c: Horizontal(g11)
    c: Vertical(g10)
    c: Vertical(g12)
    c: PointOnObject(g9,g4)
    c: Symmetric(g9,g10,g-1)
    c: Coincident(g4,g9)
    c: Tangent(g1,g13)
    c: Tangent(g2,g13)
    c: Radius(g13) = 2
    c: Tangent(g0,g14)
    c: Tangent(g1,g14)
    c: Tangent(g0,g15)
    c: Tangent(g3,g15)
    c: Tangent(g2,g16)
    c: Tangent(g3,g16)
    c: Coincident(g17,g18)
    c: Coincident(g18,g19)
    c: Coincident(g19,g20)
    c: Coincident(g20,g17)
    c: Horizontal(g17)
    c: Horizontal(g19)
    c: Vertical(g18)
    c: Vertical(g20)
    c: Coincident(g17,g15)
    c: Symmetric(g15,g18,g-1)
    c: PointOnObject(g15,g4)
    c: Equal(g15,g16)
    c: Equal(g16,g14)
    c: Equal(g14,g13)
    c: DistanceX(g3,g1) = 40.1
    c: DistanceY(g0,g2) = -20.8
    c: Tangent(g8,g21)
    c: Tangent(g5,g21)
    c: PointOnObject(g21,g4)
    c: Coincident(g21,g15)
    c: Coincident(g4,g15)
    c: DistanceX(g8,g3) = -0.3
    c: DistanceX(g3,g4) = -2
    c: Tangent(g8,g22)
    c: Tangent(g7,g22)
    c: Coincident(g22,g16)
    c: Tangent(g7,g23)
    c: Tangent(g6,g23)
    c: Coincident(g23,g18)
    c: Tangent(g5,g24)
    c: Tangent(g6,g24)
    c: Coincident(g24,g17)
    c: Coincident(g14,g17)
FEATURE [PartDesign::Pad] Pad002001003004001007012  label="side-gap-master001"
  AllowMultiFace = false
  Direction = (1,1,1)
  Length = 0.4
  Length2 = 100
  Profile = -> Sketch013
  Type = 0
FEATURE [Sketcher::SketchObject] Sketch055  label="servo-top-1-sketch003"
  FullyConstrained = false
  MapMode = 5
  sketch-geometry (10):
    g0: LineSegment StartX=-9.03485 StartY=1.65 StartZ=0 EndX=-9.03485 EndY=-1.65 EndZ=0
    g1: ArcOfCircle CenterX=-9.03485 CenterY=0 CenterZ=0 NormalX=0 NormalY=0 NormalZ=1 AngleXU=0 Radius=1.65 StartAngle=1.5708 EndAngle=4.71239
    g2: LineSegment StartX=-9.03485 StartY=1.65 StartZ=0 EndX=-2.38485 EndY=1.65 EndZ=0
    g3: LineSegment StartX=-9.03485 StartY=-1.65 StartZ=0 EndX=-2.38485 EndY=-1.65 EndZ=0
    g4: LineSegment StartX=11.1848 StartY=1.65 StartZ=0 EndX=11.1848 EndY=-1.65 EndZ=0
    g5: ArcOfCircle CenterX=0 CenterY=0 CenterZ=0 NormalX=0 NormalY=0 NormalZ=1 AngleXU=0 Radius=2.9 StartAngle=3.74684 EndAngle=5.67794
    g6: LineSegment StartX=2.38485 StartY=1.65 StartZ=0 EndX=11.1848 EndY=1.65 EndZ=0
    g7: ArcOfCircle CenterX=0 CenterY=0 CenterZ=0 NormalX=0 NormalY=0 NormalZ=1 AngleXU=0 Radius=2.9 StartAngle=0.605247 EndAngle=2.53635
    g8: LineSegment StartX=2.38485 StartY=-1.65 StartZ=0 EndX=11.1848 EndY=-1.65 EndZ=0
    g9: Circle CenterX=11.1848 CenterY=0 CenterZ=0 NormalX=0 NormalY=0 NormalZ=1 AngleXU=0 Radius=6.7
  constraints (29):
    c: Vertical(g0)
    c: Symmetric(g0,g0,g-1)
    c: Coincident(g1,g0)
    c: Coincident(g0,g1)
    c: PointOnObject(g1,g0)
    c: Horizontal(g2)
    c: Coincident(g2,g0)
    c: Horizontal(g3)
    c: Coincident(g3,g0)
    c: Coincident(g6,g4)
    c: Vertical(g4)
    c: Coincident(g4,g8)
    c: Tangent(g2,g6)
    c: PointOnObject(g7,g2)
    c: Equal(g5,g7)
    c: Coincident(g7,g6)
    c: Coincident(g5,g7)
    c: Coincident(g3,g5)
    c: Coincident(g8,g5)
    c: Tangent(g3,g8)
    c: Coincident(g7,g2)
    c: Coincident(g5,g-1)
    c: DistanceY(g0) = -3.3
    c: DistanceX(g0,g2) = 6.65
    c: Radius(g7) = 2.9
    c: Radius(g9) = 6.7
    c: PointOnObject(g9,g-1)
    c: PointOnObject(g9,g4)
    c: DistanceX(g6,g9) = 8.8
FEATURE [Sketcher::SketchObject] Sketch056  label="servo-top-1-sketch004"
  FullyConstrained = false
  MapMode = 5
  Placement = pos=(0,0,1.16) rot=(0,0,1;0rad)
  sketch-geometry (10):
    g0: LineSegment StartX=-8.99374 StartY=1.3 StartZ=0 EndX=-8.99374 EndY=-1.3 EndZ=0
    g1: ArcOfCircle CenterX=-8.99374 CenterY=0 CenterZ=0 NormalX=0 NormalY=0 NormalZ=1 AngleXU=0 Radius=1.3 StartAngle=1.5708 EndAngle=4.71239
    g2: LineSegment StartX=-8.99374 StartY=1.3 StartZ=0 EndX=-2.19374 EndY=1.3 EndZ=0
    g3: LineSegment StartX=-8.99374 StartY=-1.3 StartZ=0 EndX=-2.19374 EndY=-1.3 EndZ=0
    g4: LineSegment StartX=11.1937 StartY=1.3 StartZ=0 EndX=11.1937 EndY=-1.3 EndZ=0
    g5: ArcOfCircle CenterX=0 CenterY=0 CenterZ=0 NormalX=0 NormalY=0 NormalZ=1 AngleXU=0 Radius=2.55 StartAngle=3.67655 EndAngle=5.74823
    g6: LineSegment StartX=2.19374 StartY=1.3 StartZ=0 EndX=11.1937 EndY=1.3 EndZ=0
    g7: ArcOfCircle CenterX=0 CenterY=0 CenterZ=0 NormalX=0 NormalY=0 NormalZ=1 AngleXU=0 Radius=2.55 StartAngle=0.534957 EndAngle=2.60664
    g8: LineSegment StartX=2.19374 StartY=-1.3 StartZ=0 EndX=11.1937 EndY=-1.3 EndZ=0
    g9: Circle CenterX=11.1937 CenterY=0 CenterZ=0 NormalX=0 NormalY=0 NormalZ=1 AngleXU=0 Radius=6.7
  constraints (29):
    c: Vertical(g0)
    c: Symmetric(g0,g0,g-1)
    c: Coincident(g1,g0)
    c: Coincident(g0,g1)
    c: PointOnObject(g1,g0)
    c: Horizontal(g2)
    c: Coincident(g2,g0)
    c: Horizontal(g3)
    c: Coincident(g3,g0)
    c: Coincident(g6,g4)
    c: Vertical(g4)
    c: Coincident(g4,g8)
    c: Tangent(g2,g6)
    c: PointOnObject(g7,g2)
    c: Equal(g5,g7)
    c: Coincident(g7,g6)
    c: Coincident(g5,g7)
    c: Coincident(g3,g5)
    c: Coincident(g8,g5)
    c: Tangent(g3,g8)
    c: Coincident(g7,g2)
    c: Coincident(g5,g-1)
    c: DistanceY(g0) = -2.6
    c: DistanceX(g0,g2) = 6.8
    c: Radius(g7) = 2.55
    c: Radius(g9) = 6.7
    c: PointOnObject(g9,g-1)
    c: PointOnObject(g9,g4)
    c: DistanceX(g6,g9) = 9
FEATURE [Part::Loft] Loft003  label="servo-top-002"
  Closed = false
  MaxDegree = 5
  Ruled = false
  Sections = -> [Sketch055,Sketch056]
  Solid = true
FEATURE [Sketcher::SketchObject] Sketch057  label="shaft-base-1-sketch003"
  FullyConstrained = false
  MapMode = 5
  sketch-geometry (1):
    g0: Circle CenterX=0 CenterY=0 CenterZ=0 NormalX=0 NormalY=0 NormalZ=1 AngleXU=0 Radius=6.7
  constraints (2):
    c: Radius(g0) = 6.7
    c: Coincident(g-1,g0)
FEATURE [Sketcher::SketchObject] Sketch058  label="shaft-base-1-sketch004"
  FullyConstrained = false
  MapMode = 5
  Placement = pos=(0,0,2.2) rot=(0,0,1;0rad)
  sketch-geometry (1):
    g0: Circle CenterX=0 CenterY=0 CenterZ=0 NormalX=0 NormalY=0 NormalZ=1 AngleXU=0 Radius=5.85
  constraints (2):
    c: Radius(g0) = 5.85
    c: Coincident(g-1,g0)
FEATURE [Part::Loft] Loft004  label="Shaft-base-002"
  Closed = false
  MaxDegree = 5
  Placement = pos=(11.1848,0,0) rot=(0,0,1;0rad)
  Ruled = false
  Sections = -> [Sketch057,Sketch058]
  Solid = true
FEATURE [Part::MultiFuse] Fusion013  label="top-part-003"
  Shapes = -> [Loft003,Loft004]
FEATURE [PartDesign::Fillet] Fillet003005006002
  Base = -> Fusion013 [Edge25]
  Radius = 0.5
  SupportTransform = false
FEATURE [Part::Fillet] Fillet003005006003  label="top-part-004"
  Base = -> Fillet003005006002
  Edges = 8 edges r=0.1: [Edge6,Edge17,Edge19,Edge20,Edge21,Edge22,Edge23,Edge24]
FEATURE [App::DocumentObjectGroup] Group006  label="top-part-src001"
  Group = -> [Fusion013,Fillet003005006003]
FEATURE [Part::Feature] Fillet003005006004  label="top-part001"
  Placement = pos=(-0.634848,0,39.7) rot=(0,0,1;0rad)
  shape: bbox 28.82 x 13.4 x 14.16 mm, 24 faces (baked)
FEATURE [Sketcher::SketchObject] Sketch059  label="ears-body-1-sketch001"
  FullyConstrained = false
  MapMode = 5
  sketch-geometry (4):
    g0: LineSegment StartX=-28 StartY=9.6 StartZ=0 EndX=28 EndY=9.6 EndZ=0
    g1: LineSegment StartX=28 StartY=9.6 StartZ=0 EndX=28 EndY=-9.6 EndZ=0
    g2: LineSegment StartX=28 StartY=-9.6 StartZ=0 EndX=-28 EndY=-9.6 EndZ=0
    g3: LineSegment StartX=-28 StartY=-9.6 StartZ=0 EndX=-28 EndY=9.6 EndZ=0
  constraints (11):
    c: Coincident(g0,g1)
    c: Coincident(g1,g2)
    c: Coincident(g2,g3)
    c: Coincident(g3,g0)
    c: Horizontal(g0)
    c: Horizontal(g2)
    c: Vertical(g1)
    c: Vertical(g3)
    c: Symmetric(g0,g1,g-1)
    c: DistanceX(g0) = 56
    c: DistanceY(g3) = 19.2
FEATURE [PartDesign::Pad] Pad002001003004001007013  label="ears-body-002"
  AllowMultiFace = false
  Direction = (1,1,1)
  Length = 2.5
  Length2 = 100
  Profile = -> Sketch019
  Type = 0
FEATURE [Sketcher::SketchObject] Sketch060  label="right-ears-sketch001"
  FullyConstrained = false
  MapMode = 5
  Placement = pos=(0,0,2.5) rot=(0,0,1;0rad)
  Support = -> [Pad002001003004001007013]
  sketch-geometry (9):
    g0: ArcOfCircle CenterX=25.15 CenterY=5.1 CenterZ=0 NormalX=0 NormalY=0 NormalZ=1 AngleXU=0 Radius=2.25 StartAngle=0.605154 EndAngle=5.67803
    g1: LineSegment StartX=22.9 StartY=5.1 StartZ=0 EndX=25.15 EndY=5.1 EndZ=0
    g2: LineSegment StartX=27.0004 StartY=6.38 StartZ=0 EndX=29.0004 EndY=6.38 EndZ=0
    g3: LineSegment StartX=29.0004 StartY=6.38 StartZ=0 EndX=29.0004 EndY=3.82 EndZ=0
    g4: LineSegment StartX=29.0004 StartY=3.82 StartZ=0 EndX=27.0004 EndY=3.82 EndZ=0
    g5: ArcOfCircle CenterX=25.15 CenterY=-5.1 CenterZ=0 NormalX=0 NormalY=0 NormalZ=1 AngleXU=0 Radius=2.25 StartAngle=0.605154 EndAngle=5.67803
    g6: LineSegment StartX=27.0004 StartY=-3.82 StartZ=0 EndX=29.0004 EndY=-3.82 EndZ=0
    g7: LineSegment StartX=29.0004 StartY=-3.82 StartZ=0 EndX=29.0004 EndY=-6.38 EndZ=0
    g8: LineSegment StartX=29.0004 StartY=-6.38 StartZ=0 EndX=27.0004 EndY=-6.38 EndZ=0
  constraints (28):
    c: Radius(g0) = 2.25
    c: DistanceX(g0) = 25.15
    c: DistanceY(g0) = 5.1
    c: Horizontal(g1)
    c: PointOnObject(g1,g0)
    c: Coincident(g1,g0)
    c: Coincident(g2,g3)
    c: Coincident(g3,g4)
    c: Horizontal(g2)
    c: Horizontal(g4)
    c: Vertical(g3)
    c: Coincident(g0,g2)
    c: Coincident(g0,g4)
    c: Symmetric(g0,g0,g1)
    c: DistanceY(g3) = -2.56
    c: DistanceX(g2) = 2
    c: Symmetric(g5,g0,g-1)
    c: Equal(g0,g5)
    c: Coincident(g6,g7)
    c: Coincident(g7,g8)
    c: Horizontal(g6)
    c: Horizontal(g8)
    c: Vertical(g7)
    c: Coincident(g6,g5)
    c: Coincident(g8,g5)
    c: Symmetric(g5,g0,g-1)
    c: Symmetric(g0,g5,g-1)
    c: Symmetric(g6,g3,g-1)
FEATURE [PartDesign::Pocket] Pocket027  label="right-ear001"
  AllowMultiFace = false
  Length = 5
  Length2 = 100
  Profile = -> Sketch020
  Type = 1
FEATURE [PartDesign::Mirrored] Mirrored003  label="ears-block-005"
  MirrorPlane = -> Sketch060 [V_Axis]
  Originals = -> [Pocket027]
FEATURE [Sketcher::SketchObject] Sketch061  label="ears-block-2-sketch001"
  FullyConstrained = false
  MapMode = 5
  Placement = pos=(0,0,2.5) rot=(0,0,1;0rad)
  Support = -> [Mirrored003]
  sketch-geometry (6):
    g0: ArcOfCircle CenterX=-23.8 CenterY=0 CenterZ=0 NormalX=0 NormalY=0 NormalZ=1 AngleXU=0 Radius=1 StartAngle=1.57079 EndAngle=4.7124
    g1: ArcOfCircle CenterX=23.8 CenterY=0 CenterZ=0 NormalX=0 NormalY=0 NormalZ=1 AngleXU=0 Radius=1 StartAngle=4.71238 EndAngle=7.85399
    g2: LineSegment StartX=-23.8 StartY=-1 StartZ=0 EndX=23.8 EndY=-1 EndZ=0
    g3: LineSegment StartX=-23.8 StartY=1 StartZ=0 EndX=23.8 EndY=1 EndZ=0
    g4: GeomPoint X=-24.8 Y=0 Z=0
    g5: GeomPoint X=24.8 Y=0 Z=0
  constraints (18):
    c: Tangent(g0,g2)
    c: Tangent(g0,g3)
    c: Tangent(g1,g2)
    c: Tangent(g1,g3)
    c: Coincident(g0,g3)
    c: Coincident(g0,g2)
    c: Coincident(g2,g1)
    c: Coincident(g3,g1)
    c: Horizontal(g2)
    c: Equal(g0,g1)
    c: Symmetric(g0,g1,g-2)
    c: PointOnObject(g0,g-1)
    c: DistanceY(g0,g0) = 2
    c: PointOnObject(g4,g-1)
    c: PointOnObject(g4,g0)
    c: PointOnObject(g5,g-1)
    c: PointOnObject(g5,g1)
    c: DistanceX(g4,g5) = 49.6
FEATURE [PartDesign::Pad] Pad002001003004001007014  label="ears-block-006"
  AllowMultiFace = false
  Direction = (1,1,1)
  Length = 0.86
  Length2 = 100
  Profile = -> Sketch021
  Type = 0
FEATURE [Sketcher::SketchObject] Sketch062  label="wire-holder-base-sketch001"
  FullyConstrained = false
  MapMode = 5
  Placement = pos=(0,0,0) rot=(0.57735,0.57735,0.57735;2.0944rad)
  sketch-geometry (4):
    g0: LineSegment StartX=-3.4 StartY=2.15 StartZ=0 EndX=3.4 EndY=2.15 EndZ=0
    g1: LineSegment StartX=3.4 StartY=2.15 StartZ=0 EndX=3.4 EndY=-2.15 EndZ=0
    g2: LineSegment StartX=3.4 StartY=-2.15 StartZ=0 EndX=-3.4 EndY=-2.15 EndZ=0
    g3: LineSegment StartX=-3.4 StartY=-2.15 StartZ=0 EndX=-3.4 EndY=2.15 EndZ=0
  constraints (11):
    c: Coincident(g0,g1)
    c: Coincident(g1,g2)
    c: Coincident(g2,g3)
    c: Coincident(g3,g0)
    c: Horizontal(g0)
    c: Horizontal(g2)
    c: Vertical(g1)
    c: Vertical(g3)
    c: Symmetric(g0,g1,g-1)
    c: DistanceY(g1) = -4.3
    c: DistanceX(g0) = 6.8
FEATURE [PartDesign::Pad] Pad002001003004001007015  label="wire-holder-base001"
  AllowMultiFace = false
  Direction = (1,1,1)
  Length = 1.5
  Length2 = 100
  Placement = pos=(0,0,0) rot=(0.57735,0.57735,0.57735;2.0944rad)
  Profile = -> Sketch022
  Type = 0
FEATURE [Sketcher::SketchObject] Sketch063  label="wire-holder-body-1-sketch003"
  FullyConstrained = false
  MapMode = 5
  Placement = pos=(0,0,0) rot=(0.57735,0.57735,0.57735;2.0944rad)
  sketch-geometry (4):
    g0: LineSegment StartX=-2.975 StartY=1.85 StartZ=0 EndX=2.975 EndY=1.85 EndZ=0
    g1: LineSegment StartX=2.975 StartY=1.85 StartZ=0 EndX=2.975 EndY=-1.85 EndZ=0
    g2: LineSegment StartX=2.975 StartY=-1.85 StartZ=0 EndX=-2.975 EndY=-1.85 EndZ=0
    g3: LineSegment StartX=-2.975 StartY=-1.85 StartZ=0 EndX=-2.975 EndY=1.85 EndZ=0
  constraints (11):
    c: Coincident(g0,g1)
    c: Coincident(g1,g2)
    c: Coincident(g2,g3)
    c: Coincident(g3,g0)
    c: Horizontal(g0)
    c: Horizontal(g2)
    c: Vertical(g1)
    c: Vertical(g3)
    c: Symmetric(g0,g1,g-1)
    c: DistanceX(g0) = 5.95
    c: DistanceY(g3) = 3.7
FEATURE [Sketcher::SketchObject] Sketch064  label="wire-holder-body-1-sketch004"
  FullyConstrained = false
  MapMode = 5
  Placement = pos=(4.2,0,0) rot=(0.57735,0.57735,0.57735;2.0944rad)
  sketch-geometry (4):
    g0: LineSegment StartX=-2.7 StartY=1.55 StartZ=0 EndX=2.7 EndY=1.55 EndZ=0
    g1: LineSegment StartX=2.7 StartY=1.55 StartZ=0 EndX=2.7 EndY=-1.55 EndZ=0
    g2: LineSegment StartX=2.7 StartY=-1.55 StartZ=0 EndX=-2.7 EndY=-1.55 EndZ=0
    g3: LineSegment StartX=-2.7 StartY=-1.55 StartZ=0 EndX=-2.7 EndY=1.55 EndZ=0
  constraints (11):
    c: Coincident(g0,g1)
    c: Coincident(g1,g2)
    c: Coincident(g2,g3)
    c: Coincident(g3,g0)
    c: Horizontal(g0)
    c: Horizontal(g2)
    c: Vertical(g1)
    c: Vertical(g3)
    c: Symmetric(g0,g1,g-1)
    c: DistanceX(g0) = 5.4
    c: DistanceY(g1) = -3.1
FEATURE [Part::Loft] Loft005  label="wire-holder-body-005"
  Closed = false
  MaxDegree = 5
  Ruled = false
  Sections = -> [Sketch063,Sketch064]
  Solid = true
FEATURE [Sketcher::SketchObject] Sketch065  label="wire-holes-sketch001"
  FullyConstrained = false
  MapMode = 5
  Placement = pos=(4.2,-7e-16,0) rot=(0.57735,0.57735,0.57735;2.0944rad)
  Support = -> [Loft005]
  sketch-geometry (8):
    g0: ArcOfCircle CenterX=-1.2 CenterY=0 CenterZ=0 NormalX=0 NormalY=0 NormalZ=1 AngleXU=0 Radius=0.7 StartAngle=0.666946 EndAngle=5.61624
    g1: LineSegment StartX=-0.65 StartY=0.433013 StartZ=0 EndX=-0.55 EndY=0.433013 EndZ=0
    g2: ArcOfCircle CenterX=0 CenterY=0 CenterZ=0 NormalX=0 NormalY=0 NormalZ=1 AngleXU=0 Radius=0.7 StartAngle=0.666946 EndAngle=2.47465
    g3: LineSegment StartX=0.55 StartY=0.433013 StartZ=0 EndX=0.65 EndY=0.433013 EndZ=0
    g4: LineSegment StartX=-0.65 StartY=-0.433013 StartZ=0 EndX=-0.55 EndY=-0.433013 EndZ=0
    g5: ArcOfCircle CenterX=0 CenterY=0 CenterZ=0 NormalX=0 NormalY=0 NormalZ=1 AngleXU=0 Radius=0.7 StartAngle=3.80854 EndAngle=5.61624
    g6: ArcOfCircle CenterX=1.2 CenterY=0 CenterZ=0 NormalX=0 NormalY=0 NormalZ=1 AngleXU=0 Radius=0.7 StartAngle=3.80854 EndAngle=8.75783
    g7: LineSegment StartX=0.55 StartY=-0.433013 StartZ=0 EndX=0.65 EndY=-0.433013 EndZ=0
  constraints (26):
    c: PointOnObject(g0,g-1)
    c: Horizontal(g1)
    c: Coincident(g1,g0)
    c: Coincident(g3,g6)
    c: Coincident(g1,g2)
    c: Coincident(g3,g2)
    c: Tangent(g1,g3)
    c: Horizontal(g4)
    c: Symmetric(g0,g4,g-1)
    c: PointOnObject(g0,g4)
    c: PointOnObject(g6,g4)
    c: Coincident(g4,g5)
    c: Coincident(g7,g5)
    c: Tangent(g4,g7)
    c: PointOnObject(g7,g6)
    c: Equal(g1,g4)
    c: Equal(g4,g3)
    c: Equal(g3,g7)
    c: Equal(g5,g0)
    c: Equal(g0,g2)
    c: Equal(g2,g6)
    c: Radius(g6) = 0.7
    c: DistanceX(g0,g6) = 2.4
    c: Coincident(g5,g-1)
    c: Coincident(g2,g-1)
    c: DistanceX(g1) = 0.1
FEATURE [PartDesign::Pocket] Pocket028  label="wire-holder-body-006"
  AllowMultiFace = false
  Length = 5
  Length2 = 100
  Profile = -> Sketch025
  Type = 1
FEATURE [Part::Feature] Pocket029  label="wire-holder-body-2-copy001"
  Placement = pos=(1.5,0,0) rot=(0,0,1;0rad)
  shape: bbox 4.2 x 5.95 x 3.7 mm, 14 faces (baked)
FEATURE [Part::MultiFuse] Fusion014  label="wire-holder-body-007"
  Shapes = -> [Pad002001003004001007015,Pocket029]
FEATURE [Part::Fillet] Fillet003005006005  label="wire-holder-body-008"
  Base = -> Fusion014
  Edges = 8 edges r=0.5: [Edge1,Edge2,Edge5,Edge8,Edge17,Edge18,Edge20,Edge22]
FEATURE [App::DocumentObjectGroup] Group008  label="wire-holder-src001"
  Group = -> [Pad002001003004001007015,Loft005,Pocket028,Pocket029,Fusion014,Fillet003005006005]
FEATURE [Part::Feature] Fillet003005006006  label="wire-holder001"
  Placement = pos=(20.55,0,6.35) rot=(0,0,1;0rad)
  shape: bbox 5.992 x 6.8 x 4.3 mm, 28 faces (baked)
FEATURE [Part::Fillet] Fillet003005006007
  Base = -> Pad002001003004001007014
  Edges = 4 edges r=0.8: [Edge33,Edge34,Edge69,Edge71]
FEATURE [Part::Fillet] Fillet003005006008
  Base = -> Fillet003005006007
  Edges = 16 edges r=0.6: [Edge37,Edge39,Edge41,Edge43,Edge44,Edge46,Edge49,Edge51,Edge53,Edge55,Edge57,Edge59,Edge60,Edge62,Edge65,Edge67]
FEATURE [Part::Fillet] Fillet003005006009  label="ears-block-007"
  Base = -> Fillet003005006008
  Edges = 1 edges r=0.2: [Edge36]
FEATURE [Part::Fillet] Fillet003005006010  label="ears-block-008"
  Base = -> Fillet003005006009
  Edges = 1 edges r=0.2: [Edge132]
FEATURE [App::DocumentObjectGroup] Group007  label="ears-src001"
  Group = -> [Pad002001003004001007013,Pocket027,Mirrored003,Pad002001003004001007014,Fillet003005006009,Fillet003005006010]
FEATURE [Part::Feature] Fillet003005006011  label="ears001"
  Placement = pos=(0,0,28.9) rot=(0,0,1;0rad)
  shape: bbox 56.13 x 19.33 x 3.36 mm, 91 faces (baked)
FEATURE [Sketcher::SketchObject] Sketch066  label="shaft-body-sketch001"
  FullyConstrained = false
  MapMode = 5
  sketch-geometry (1):
    g0: Circle CenterX=0 CenterY=0 CenterZ=0 NormalX=0 NormalY=0 NormalZ=1 AngleXU=0 Radius=3
  constraints (2):
    c: Coincident(g0,g-1)
    c: Radius(g0) = 3
FEATURE [PartDesign::Pad] Pad002001003004001007016  label="shaft-body001"
  AllowMultiFace = false
  Direction = (1,1,1)
  Length = 4.4
  Length2 = 100
  Profile = -> Sketch026
  Type = 0
FEATURE [Sketcher::SketchObject] Sketch067  label="shaft-body-2-sketch001"
  FullyConstrained = false
  MapMode = 5
  Placement = pos=(0,0,4.4) rot=(0,0,1;0rad)
  Support = -> [Pad002001003004001007016]
  sketch-geometry (1):
    g0: Circle CenterX=0 CenterY=0 CenterZ=0 NormalX=0 NormalY=0 NormalZ=1 AngleXU=0 Radius=1.1
  constraints (2):
    c: Coincident(g0,g-1)
    c: Radius(g0) = 1.1
FEATURE [PartDesign::Pocket] Pocket030  label="shaft-body-004"
  AllowMultiFace = false
  Length = 5
  Length2 = 100
  Profile = -> Sketch027
  Type = 1
FEATURE [PartDesign::Chamfer] Chamfer001003  label="shaft-body-005"
  Angle = 45
  Base = -> Pocket030 [Edge3]
  ChamferType = 0
  FlipDirection = false
  Size = 0.3
  Size2 = 1
  SupportTransform = false
FEATURE [Sketcher::SketchObject] Sketch068  label="shaft-tooth-sketch001"
  FullyConstrained = false
  MapMode = 5
  Placement = pos=(0,0,4.4) rot=(0,0,1;0rad)
  Support = -> [Chamfer001003]
  sketch-geometry (3):
    g0: LineSegment StartX=-0.2 StartY=3 StartZ=0 EndX=0 EndY=2.8 EndZ=0
    g1: LineSegment StartX=0.2 StartY=3 StartZ=0 EndX=0 EndY=2.8 EndZ=0
    g2: LineSegment StartX=-0.2 StartY=3 StartZ=0 EndX=0.2 EndY=3 EndZ=0
  constraints (8):
    c: Horizontal(g2)
    c: Coincident(g2,g0)
    c: Coincident(g2,g1)
    c: Symmetric(g0,g1,g-2)
    c: DistanceX(g2) = 0.4
    c: Coincident(g0,g1)
    c: PointOnObject(g0,g-2)
    c: DistanceY(g0,g1) = 0.2
FEATURE [PartDesign::Pocket] Pocket031  label="shaft-tooth001"
  AllowMultiFace = false
  Length = 3.4
  Length2 = 100
  Profile = -> Sketch028
  Type = 0
FEATURE [PartDesign::PolarPattern] PolarPattern001006  label="shaft-teeth001"
  Angle = 360
  Axis = -> Sketch068 [N_Axis]
  Occurrences = 28
  Originals = -> [Pocket031]
FEATURE [PartDesign::Chamfer] Chamfer001004  label="shaft-final001"
  Angle = 45
  Base = -> PolarPattern001006 [Edge286]
  ChamferType = 0
  FlipDirection = false
  Size = 0.3
  Size2 = 1
  SupportTransform = false
FEATURE [App::DocumentObjectGroup] Group009  label="shaft-src001"
  Group = -> [Pad002001003004001007016,Pocket030,Chamfer001003,Pocket031,PolarPattern001006,Chamfer001004]
FEATURE [Part::Feature] Chamfer001005  label="shaft002"
  Placement = pos=(10.55,0,41.9) rot=(0,0,1;0rad)
  shape: bbox 6 x 6 x 4.4 mm, 90 faces (baked)
FEATURE [Part::Feature] Pad002001003004001007017  label="bottom-side-gap001"
  Placement = pos=(0,0,7.5) rot=(0,0,1;0rad)
  shape: bbox 44.1 x 24.8 x 0.4 mm, 14 faces (baked)
FEATURE [Part::Feature] Pad002001003004001007018  label="top-side-gap001"
  Placement = pos=(0,0,28.5) rot=(0,0,1;0rad)
  shape: bbox 44.1 x 24.8 x 0.4 mm, 14 faces (baked)
FEATURE [Part::MultiFuse] Fusion015  label="side-gaps001"
  Shapes = -> [Pad002001003004001007017,Pad002001003004001007018]
FEATURE [PartDesign::Fillet] Fillet003005006012  label="servo-body-final-008"
  Base = -> Pad002001003004001007011 [Edge31,Edge38,Edge25,Edge32]
  Radius = 2
  SupportTransform = false
FEATURE [Part::Cut] Cut001002008  label="servo-body-final-009"
  Base = -> Fillet003005006012
  Tool = -> Fusion015
FEATURE [Part::Fillet] Fillet003005006013  label="servo-body-final-010"
  Base = -> Cut001002008
  Edges = 3 edges r=0.3: [Edge1,Edge3,Edge14]
FEATURE [App::DocumentObjectGroup] Group005  label="Servo-body-src001"
  Group = -> [Pad002001003004001007002,Pocket019,Mirrored002,Pocket020,Pocket021,Pocket022,Pocket023,Pocket024,Pocket025,Pad002001003004001007003,Pad002001003004001007004,Cut001002007,Pad002001003004001007011,Pad002001003004001007012,Pad002001003004001007017,Pad002001003004001007018,Fusion015,Fillet003005006012,Cut001002008,Fillet003005006013]
FEATURE [Part::Feature] Fillet003005006014  label="servo-body001"
  shape: bbox 41.26 x 21.13 x 39.7 mm, 208 faces (baked)
FEATURE [Part::MultiFuse] Fusion016  label="servo-003"
  Shapes = -> [Fillet003005006004,Fillet003005006011,Fillet003005006006,Fillet003005006014]
FEATURE [Part::Feature] Cut001002009  label="bottom-screw-005"
  Placement = pos=(-18.1075,7.95754,34.2) rot=(1,0,0;3.14159rad)
  shape: bbox 3.75 x 3.75 x 33.19 mm, 18 faces (baked)
FEATURE [Part::Feature] Cut001002010  label="bottom-screw-006"
  Placement = pos=(18.1075,-7.95754,34.2) rot=(1,0,0;3.14159rad)
  shape: bbox 3.75 x 3.75 x 33.19 mm, 18 faces (baked)
FEATURE [Part::Feature] Cut001002011  label="bottom-screw-007"
  Placement = pos=(18.1075,7.95754,34.2) rot=(1,0,0;3.14159rad)
  shape: bbox 3.75 x 3.75 x 33.19 mm, 18 faces (baked)
FEATURE [Part::Feature] Cut001002012  label="bottom-screw-008"
  Placement = pos=(-18.1075,-7.95754,34.2) rot=(1,0,0;3.14159rad)
  shape: bbox 3.75 x 3.75 x 33.19 mm, 18 faces (baked)
FEATURE [Part::Compound] Compound005  label="bottom-screws002"
  Links = -> [Cut001002009,Cut001002012,Cut001002010,Cut001002011]
FEATURE [Part::Cylinder] Cylinder004  label="wire-center001"
  Angle = 360
  AttacherType = Attacher::AttachEngine3D
  Height = 10
  Placement = pos=(1.5,0,0) rot=(0,1,0;1.5708rad)
  Radius = 0.65
FEATURE [Part::Feature] Cylinder005  label="wire-right001"
  Placement = pos=(1.5,1.2,-8e-16) rot=(0,1,0;1.5708rad)
  shape: bbox 10 x 1.3 x 1.3 mm, 3 faces (baked)
FEATURE [Part::Feature] Cylinder006  label="wire-left001"
  Placement = pos=(1.5,-1.2,0) rot=(0,1,0;1.5708rad)
  shape: bbox 10 x 1.3 x 1.3 mm, 3 faces (baked)
FEATURE [Part::MultiFuse] Fusion017  label="wires002"
  Placement = pos=(20.55,0,6.35) rot=(0,0,1;0rad)
  Shapes = -> [Cylinder004,Cylinder005,Cylinder006]
FEATURE [Part::Compound] Compound006  label="Servo-SM-S4303R-assembly001"
  Links = -> [Chamfer001005,Fusion016,Fusion017,Compound005]
FEATURE [Part::Feature] Chamfer001006  label="shaft003"
  Placement = pos=(10.55,0,41.9) rot=(0,0,1;0rad)
  shape: bbox 6 x 6 x 4.4 mm, 90 faces (baked)
FEATURE [Part::Feature] Fusion018  label="wires003"
  Placement = pos=(20.55,0,6.35) rot=(0,0,1;0rad)
  shape: bbox 10 x 3.7 x 1.3 mm, 9 faces (baked)
FEATURE [Part::Feature] Fusion019  label="servo-004"
  shape: bbox 56.13 x 21.13 x 45.15 mm, 371 faces (baked)
FEATURE [Part::Feature] Compound008  label="bottom-screws003"
  shape: bbox 39.97 x 19.67 x 33.19 mm, 72 faces, 4 solids (baked)
FEATURE [Part::Compound] Compound007  label="Servo-SM-S4303R-compound001"
  Links = -> [Compound008,Fusion019,Fusion018,Chamfer001006]
FEATURE [Part::Compound] Compound009  label="servo2"
  Placement = pos=(-17.4155,188.533,-9.88067) rot=(0.603116,0.569152,0.558853;2.05618rad)
FEATURE [Sketcher::SketchObject] Sketch069
  FullyConstrained = false
  MapMode = 5
  Support = -> [XY_Plane005]
  sketch-geometry (9):
    g0: LineSegment StartX=7.36377 StartY=12.7393 StartZ=0 EndX=-7.35069 EndY=12.7469 EndZ=0
    g1: LineSegment StartX=-7.35069 StartY=12.7469 StartZ=0 EndX=-14.7145 EndY=0.00755112 EndZ=0
    g2: LineSegment StartX=-14.7145 StartY=0.00755112 StartZ=0 EndX=-7.36377 EndY=-12.7393 EndZ=0
    g3: LineSegment StartX=-7.36377 StartY=-12.7393 StartZ=0 EndX=7.35069 EndY=-12.7469 EndZ=0
    g4: LineSegment StartX=7.35069 StartY=-12.7469 StartZ=0 EndX=14.7145 EndY=-0.00755112 EndZ=0
    g5: LineSegment StartX=14.7145 StartY=-0.00755112 StartZ=0 EndX=7.36377 EndY=12.7393 EndZ=0
    g6: Circle CenterX=0 CenterY=0 CenterZ=0 NormalX=0 NormalY=0 NormalZ=1 AngleXU=0 Radius=14.7145
    g7: Circle CenterX=-10.4508 CenterY=0 CenterZ=0 NormalX=0 NormalY=0 NormalZ=1 AngleXU=0 Radius=1.48082
    g8: Circle CenterX=10.4782 CenterY=0 CenterZ=0 NormalX=0 NormalY=0 NormalZ=1 AngleXU=0 Radius=1.58263
  constraints (16):
    c: Coincident(g0,g1)
    c: Coincident(g1,g2)
    c: Coincident(g2,g3)
    c: Coincident(g3,g4)
    c: Coincident(g4,g5)
    c: Coincident(g5,g0)
    c: Equal(g0, g1-g5) x5
    c: PointOnObject(g0,g6)
    c: PointOnObject(g1,g6)
    c: PointOnObject(g2,g6)
    c: PointOnObject(g3,g6)
    c: PointOnObject(g4,g6)
    c: PointOnObject(g5,g6)
    c: Coincident(g6,g-1)
    c: PointOnObject(g7,g-1)
    c: PointOnObject(g8,g-1)
FEATURE [PartDesign::Pad] Pad002001003004001007019
  Direction = (1,1,1)
  Length = 1
  Length2 = 100
  Profile = -> Sketch069
  Type = 0
FEATURE [PartDesign::Body] Body005  label="Body_hexagon"
  Group = -> [Sketch069,Pad002001003004001007019]
  Origin = -> Origin005
  Tip = -> Pad002001003004001007019
FEATURE [Part::Box] Box004  label="Vcc"
  AttacherType = Attacher::AttachEngine3D
  Height = 5
  Length = 10
  Placement = pos=(-5,6,1) rot=(0,0,1;0rad)
  Width = 15
FEATURE [Part::Box] Box005  label="Elemento1"
  AttacherType = Attacher::AttachEngine3D
  Height = 4
  Length = 4
  Placement = pos=(3,-2,1) rot=(0,0,1;0rad)
  Width = 4
FEATURE [App::LinkGroup] LinkGroup005  label="infrarrojos1"
  ElementList = -> [Body005,Box004,Box005]
  LinkMode = 0
  Placement = pos=(45,130,48.9999) rot=(0.509027,0.694106,-0.509027;0rad)
FEATURE [Sketcher::SketchObject] Sketch070
  FullyConstrained = false
  MapMode = 5
  Support = -> [XY_Plane006]
  sketch-geometry (9):
    g0: LineSegment StartX=7.36377 StartY=12.7393 StartZ=0 EndX=-7.35069 EndY=12.7469 EndZ=0
    g1: LineSegment StartX=-7.35069 StartY=12.7469 StartZ=0 EndX=-14.7145 EndY=0.00755112 EndZ=0
    g2: LineSegment StartX=-14.7145 StartY=0.00755112 StartZ=0 EndX=-7.36377 EndY=-12.7393 EndZ=0
    g3: LineSegment StartX=-7.36377 StartY=-12.7393 StartZ=0 EndX=7.35069 EndY=-12.7469 EndZ=0
    g4: LineSegment StartX=7.35069 StartY=-12.7469 StartZ=0 EndX=14.7145 EndY=-0.00755112 EndZ=0
    g5: LineSegment StartX=14.7145 StartY=-0.00755112 StartZ=0 EndX=7.36377 EndY=12.7393 EndZ=0
    g6: Circle CenterX=0 CenterY=0 CenterZ=0 NormalX=0 NormalY=0 NormalZ=1 AngleXU=0 Radius=14.7145
    g7: Circle CenterX=-10.4508 CenterY=0 CenterZ=0 NormalX=0 NormalY=0 NormalZ=1 AngleXU=0 Radius=1.48082
    g8: Circle CenterX=10.4782 CenterY=0 CenterZ=0 NormalX=0 NormalY=0 NormalZ=1 AngleXU=0 Radius=1.58263
  constraints (16):
    c: Coincident(g0,g1)
    c: Coincident(g1,g2)
    c: Coincident(g2,g3)
    c: Coincident(g3,g4)
    c: Coincident(g4,g5)
    c: Coincident(g5,g0)
    c: Equal(g0, g1-g5) x5
    c: PointOnObject(g0,g6)
    c: PointOnObject(g1,g6)
    c: PointOnObject(g2,g6)
    c: PointOnObject(g3,g6)
    c: PointOnObject(g4,g6)
    c: PointOnObject(g5,g6)
    c: Coincident(g6,g-1)
    c: PointOnObject(g7,g-1)
    c: PointOnObject(g8,g-1)
FEATURE [PartDesign::Pad] Pad002001003004001007020
  Direction = (1,1,1)
  Length = 1
  Length2 = 100
  Profile = -> Sketch070
  Type = 0
FEATURE [PartDesign::Body] Body006  label="Body_hexagon001"
  Group = -> [Sketch070,Pad002001003004001007020]
  Origin = -> Origin006
  Tip = -> Pad002001003004001007020
FEATURE [Part::Box] Box006  label="Vcc001"
  AttacherType = Attacher::AttachEngine3D
  Height = 5
  Length = 10
  Placement = pos=(-5,6,1) rot=(0,0,1;0rad)
  Width = 15
FEATURE [Part::Box] Box007  label="Elemento002"
  AttacherType = Attacher::AttachEngine3D
  Height = 4
  Length = 4
  Placement = pos=(3,-2,1) rot=(0,0,1;0rad)
  Width = 4
FEATURE [App::LinkGroup] LinkGroup006  label="infrarrojos2"
  ElementList = -> [Body006,Box006,Box007]
  LinkMode = 0
  Placement = pos=(-45.9999,127,49.0002) rot=(0,0.968835,0.247706;0rad)
FEATURE [App::LinkGroup] LinkGroup007  label="rueda_completa1"
  ElementList = -> [LinkGroup003,Compound009]
  LinkMode = 0
  Placement = pos=(60,55.0001,54) rot=(0,0,1;0rad)
FEATURE [App::LinkGroup] LinkGroup008  label="rueda_completa2"
  ElementList = -> [Compound004,LinkGroup002]
  LinkMode = 0
  Placement = pos=(12,56,53) rot=(0,0,1;0rad)
FEATURE [Sketcher::SketchObject] Sketch071
  FullyConstrained = false
  MapMode = 5
  Support = -> [XY_Plane007]
  sketch-geometry (4):
    g0: LineSegment StartX=-70.5237 StartY=57.5569 StartZ=0 EndX=69.4763 EndY=57.5569 EndZ=0
    g1: LineSegment StartX=69.4763 StartY=57.5569 StartZ=0 EndX=69.4763 EndY=-82.4431 EndZ=0
    g2: LineSegment StartX=69.4763 StartY=-82.4431 StartZ=0 EndX=-70.5237 EndY=-82.4431 EndZ=0
    g3: LineSegment StartX=-70.5237 StartY=-82.4431 StartZ=0 EndX=-70.5237 EndY=57.5569 EndZ=0
  constraints (10):
    c: Coincident(g0,g1)
    c: Coincident(g1,g2)
    c: Coincident(g2,g3)
    c: Coincident(g3,g0)
    c: Horizontal(g0)
    c: Horizontal(g2)
    c: Vertical(g1)
    c: Vertical(g3)
    c: DistanceX(g0,g0) = 140
    c: DistanceY(g1,g1) = 140
FEATURE [PartDesign::Pad] Pad002001003004001007021
  Direction = (1,1,1)
  Length = 20
  Length2 = 100
  Profile = -> Sketch071
  Type = 0
FEATURE [PartDesign::Body] Body007  label="base"
  Group = -> [Sketch071,Pad002001003004001007021]
  Origin = -> Origin007
  Placement = pos=(0,205,54) rot=(0,0,1;0rad)
  Tip = -> Pad002001003004001007021
FEATURE [Sketcher::SketchObject] Sketch072
  FullyConstrained = false
  MapMode = 5
  Support = -> [XY_Plane008]
  sketch-geometry (6):
    g0: LineSegment StartX=-22.7789 StartY=11.5836 StartZ=0 EndX=27.2211 EndY=11.5836 EndZ=0
    g1: LineSegment StartX=27.2211 StartY=11.5836 StartZ=0 EndX=27.2211 EndY=-10.9971 EndZ=0
    g2: LineSegment StartX=27.2211 StartY=-10.9971 StartZ=0 EndX=-22.7789 EndY=-10.9971 EndZ=0
    g3: LineSegment StartX=-22.7789 StartY=-10.9971 StartZ=0 EndX=-22.7789 EndY=11.5836 EndZ=0
    g4: Circle CenterX=-15.32 CenterY=0 CenterZ=0 NormalX=0 NormalY=0 NormalZ=1 AngleXU=0 Radius=1.49781
    g5: Circle CenterX=18.8064 CenterY=-0.289318 CenterZ=0 NormalX=0 NormalY=0 NormalZ=1 AngleXU=0 Radius=1.53606
  constraints (10):
    c: Coincident(g0,g1)
    c: Coincident(g1,g2)
    c: Coincident(g2,g3)
    c: Coincident(g3,g0)
    c: Horizontal(g0)
    c: Horizontal(g2)
    c: Vertical(g1)
    c: Vertical(g3)
    c: DistanceX(g0,g0) = 50
    c: PointOnObject(g4,g-1)
FEATURE [PartDesign::Pad] Pad002001003004001007022
  Direction = (1,1,1)
  Length = 1
  Length2 = 100
  Profile = -> Sketch072
  Type = 0
FEATURE [PartDesign::Body] Body008  label="base_abajo"
  Group = -> [Sketch072,Pad002001003004001007022]
  Origin = -> Origin008
  Tip = -> Pad002001003004001007022
FEATURE [Sketcher::SketchObject] Sketch073  label="Sketch001"
  FullyConstrained = false
  MapMode = 5
  Support = -> [XY_Plane009]
  sketch-geometry (8):
    g0: LineSegment StartX=-97.2101 StartY=28.1823 StartZ=0 EndX=-55.6954 EndY=28.1823 EndZ=0
    g1: LineSegment StartX=-51.4527 StartY=23.9396 StartZ=0 EndX=-51.4527 EndY=-1.81774 EndZ=0
    g2: LineSegment StartX=-51.4527 StartY=-1.81774 StartZ=0 EndX=-101.453 EndY=-1.81774 EndZ=0
    g3: LineSegment StartX=-101.453 StartY=-1.81774 StartZ=0 EndX=-101.453 EndY=23.9396 EndZ=0
    g4: Circle CenterX=-91.7643 CenterY=16.2056 CenterZ=0 NormalX=0 NormalY=0 NormalZ=1 AngleXU=0 Radius=6.0872
    g5: ArcOfCircle CenterX=-97.2101 CenterY=23.9396 CenterZ=0 NormalX=0 NormalY=0 NormalZ=1 AngleXU=0 Radius=4.24264 StartAngle=1.5708 EndAngle=3.14159
    g6: ArcOfCircle CenterX=-55.6954 CenterY=23.9396 CenterZ=0 NormalX=0 NormalY=0 NormalZ=1 AngleXU=0 Radius=4.24264 StartAngle=0 EndAngle=1.5708
    g7: Circle CenterX=-63.0169 CenterY=16.3189 CenterZ=0 NormalX=0 NormalY=0 NormalZ=1 AngleXU=0 Radius=6.30541
  constraints (10):
    c: Coincident(g1,g2)
    c: Coincident(g2,g3)
    c: Horizontal(g0)
    c: Horizontal(g2)
    c: Vertical(g1)
    c: Vertical(g3)
    c: Tangent(g0,g5) = 1.5708
    c: Tangent(g3,g5) = 1.5708
    c: Tangent(g0,g6) = 1.5708
    c: Tangent(g1,g6) = 1.5708
FEATURE [PartDesign::Pad] Pad002001003004001007023
  Direction = (1,1,1)
  Length = 1
  Length2 = 100
  Profile = -> Sketch073
  Type = 0
FEATURE [PartDesign::Body] Body009  label="base_arriba"
  Group = -> [Sketch073,Pad002001003004001007023]
  Origin = -> Origin009
  Placement = pos=(79,12,2) rot=(1,0,0;1.5708rad)
  Tip = -> Pad002001003004001007023
FEATURE [App::LinkGroup] LinkGroup009  label="base_ultrasonidos"
  ElementList = -> [Body009,Body008]
  LinkMode = 0
  Placement = pos=(4.7684,1.00293,-9.53674e-07) rot=(0,0,1;3.14159rad)
FEATURE [App::LinkGroup] LinkGroup010  label="union_ultra"
  ElementList = -> [LinkGroup,LinkGroup009]
  LinkMode = 0
  Placement = pos=(-7.15256e-07,125,74) rot=(0,0,1;0rad)
FEATURE [Sketcher::SketchObject] Sketch074
  FullyConstrained = false
  MapMode = 5
  Support = -> [XY_Plane010]
  sketch-geometry (7):
    g0: LineSegment StartX=-8.06452 StartY=0 StartZ=0 EndX=9.82406 EndY=0 EndZ=0
    g1: LineSegment StartX=9.82406 StartY=0 StartZ=0 EndX=9.82406 EndY=25.2473 EndZ=0
    g2: LineSegment StartX=7.652 StartY=27.4194 StartZ=0 EndX=-5.53469 EndY=27.4194 EndZ=0
    g3: LineSegment StartX=-8.06452 StartY=24.8895 StartZ=0 EndX=-8.06452 EndY=0 EndZ=0
    g4: ArcOfCircle CenterX=-5.53469 CenterY=24.8895 CenterZ=0 NormalX=0 NormalY=0 NormalZ=1 AngleXU=0 Radius=2.52983 StartAngle=1.5708 EndAngle=3.14159
    g5: ArcOfCircle CenterX=7.652 CenterY=25.2473 CenterZ=0 NormalX=0 NormalY=0 NormalZ=1 AngleXU=0 Radius=2.17205 StartAngle=0 EndAngle=1.5708
    g6: Circle CenterX=0.573308 CenterY=20.1084 CenterZ=0 NormalX=0 NormalY=0 NormalZ=1 AngleXU=0 Radius=2.31699
  constraints (11):
    c: Coincident(g0,g1)
    c: Coincident(g3,g0)
    c: Horizontal(g0)
    c: Horizontal(g2)
    c: Vertical(g1)
    c: Vertical(g3)
    c: PointOnObject(g0,g-1)
    c: Tangent(g2,g4) = -1.5708
    c: Tangent(g3,g4) = -1.5708
    c: Tangent(g1,g5) = -1.5708
    c: Tangent(g2,g5) = -1.5708
FEATURE [PartDesign::Pad] Pad002001003004001007024
  Direction = (1,1,1)
  Length = 1
  Length2 = 100
  Profile = -> Sketch074
  Type = 0
FEATURE [PartDesign::Body] Body010  label="abajo"
  Group = -> [Sketch074,Pad002001003004001007024]
  Origin = -> Origin010
  Tip = -> Pad002001003004001007024
FEATURE [Sketcher::SketchObject] Sketch075
  FullyConstrained = false
  MapMode = 5
  Support = -> [XY_Plane011]
  sketch-geometry (7):
    g0: LineSegment StartX=-8.06452 StartY=0 StartZ=0 EndX=9.82406 EndY=0 EndZ=0
    g1: LineSegment StartX=9.82406 StartY=0 StartZ=0 EndX=9.82406 EndY=25.2473 EndZ=0
    g2: LineSegment StartX=7.652 StartY=27.4194 StartZ=0 EndX=-5.53469 EndY=27.4194 EndZ=0
    g3: LineSegment StartX=-8.06452 StartY=24.8895 StartZ=0 EndX=-8.06452 EndY=0 EndZ=0
    g4: ArcOfCircle CenterX=-5.53469 CenterY=24.8895 CenterZ=0 NormalX=0 NormalY=0 NormalZ=1 AngleXU=0 Radius=2.52983 StartAngle=1.5708 EndAngle=3.14159
    g5: ArcOfCircle CenterX=7.652 CenterY=25.2473 CenterZ=0 NormalX=0 NormalY=0 NormalZ=1 AngleXU=0 Radius=2.17205 StartAngle=0 EndAngle=1.5708
    g6: Circle CenterX=0.573308 CenterY=20.1084 CenterZ=0 NormalX=0 NormalY=0 NormalZ=1 AngleXU=0 Radius=2.31699
  constraints (11):
    c: Coincident(g0,g1)
    c: Coincident(g3,g0)
    c: Horizontal(g0)
    c: Horizontal(g2)
    c: Vertical(g1)
    c: Vertical(g3)
    c: PointOnObject(g0,g-1)
    c: Tangent(g2,g4) = -1.5708
    c: Tangent(g3,g4) = -1.5708
    c: Tangent(g1,g5) = -1.5708
    c: Tangent(g2,g5) = -1.5708
FEATURE [PartDesign::Pad] Pad002001003004001007025
  Direction = (1,1,1)
  Length = 1
  Length2 = 100
  Profile = -> Sketch075
  Type = 0
FEATURE [PartDesign::Body] Body011  label="arriba"
  Group = -> [Sketch075,Pad002001003004001007025]
  Origin = -> Origin011
  Placement = pos=(0,0,0) rot=(1,0,0;1.5708rad)
  Tip = -> Pad002001003004001007025
FEATURE [App::LinkGroup] LinkGroup011  label="escuadra_final_1"
  ElementList = -> [Body011,Body010]
  LinkMode = 0
  Placement = pos=(-22.1496,25.8437,27.0599) rot=(0.999448,-0.012618,-0.030741;3.17954rad)
FEATURE [Sketcher::SketchObject] Sketch076
  FullyConstrained = false
  MapMode = 5
  Support = -> [XY_Plane012]
  sketch-geometry (7):
    g0: LineSegment StartX=-8.06452 StartY=0 StartZ=0 EndX=9.82406 EndY=0 EndZ=0
    g1: LineSegment StartX=9.82406 StartY=0 StartZ=0 EndX=9.82406 EndY=25.2473 EndZ=0
    g2: LineSegment StartX=7.652 StartY=27.4194 StartZ=0 EndX=-5.53469 EndY=27.4194 EndZ=0
    g3: LineSegment StartX=-8.06452 StartY=24.8895 StartZ=0 EndX=-8.06452 EndY=0 EndZ=0
    g4: ArcOfCircle CenterX=-5.53469 CenterY=24.8895 CenterZ=0 NormalX=0 NormalY=0 NormalZ=1 AngleXU=0 Radius=2.52983 StartAngle=1.5708 EndAngle=3.14159
    g5: ArcOfCircle CenterX=7.652 CenterY=25.2473 CenterZ=0 NormalX=0 NormalY=0 NormalZ=1 AngleXU=0 Radius=2.17205 StartAngle=0 EndAngle=1.5708
    g6: Circle CenterX=0.573308 CenterY=20.1084 CenterZ=0 NormalX=0 NormalY=0 NormalZ=1 AngleXU=0 Radius=2.31699
  constraints (11):
    c: Coincident(g0,g1)
    c: Coincident(g3,g0)
    c: Horizontal(g0)
    c: Horizontal(g2)
    c: Vertical(g1)
    c: Vertical(g3)
    c: PointOnObject(g0,g-1)
    c: Tangent(g2,g4) = -1.5708
    c: Tangent(g3,g4) = -1.5708
    c: Tangent(g1,g5) = -1.5708
    c: Tangent(g2,g5) = -1.5708
FEATURE [PartDesign::Pad] Pad002001003004001007026
  Direction = (1,1,1)
  Length = 1
  Length2 = 100
  Profile = -> Sketch076
  Type = 0
FEATURE [PartDesign::Body] Body012  label="abajo001"
  Group = -> [Sketch076,Pad002001003004001007026]
  Origin = -> Origin012
  Tip = -> Pad002001003004001007026
FEATURE [Sketcher::SketchObject] Sketch077
  FullyConstrained = false
  MapMode = 5
  Support = -> [XY_Plane013]
  sketch-geometry (7):
    g0: LineSegment StartX=-8.06452 StartY=0 StartZ=0 EndX=9.82406 EndY=0 EndZ=0
    g1: LineSegment StartX=9.82406 StartY=0 StartZ=0 EndX=9.82406 EndY=25.2473 EndZ=0
    g2: LineSegment StartX=7.652 StartY=27.4194 StartZ=0 EndX=-5.53469 EndY=27.4194 EndZ=0
    g3: LineSegment StartX=-8.06452 StartY=24.8895 StartZ=0 EndX=-8.06452 EndY=0 EndZ=0
    g4: ArcOfCircle CenterX=-5.53469 CenterY=24.8895 CenterZ=0 NormalX=0 NormalY=0 NormalZ=1 AngleXU=0 Radius=2.52983 StartAngle=1.5708 EndAngle=3.14159
    g5: ArcOfCircle CenterX=7.652 CenterY=25.2473 CenterZ=0 NormalX=0 NormalY=0 NormalZ=1 AngleXU=0 Radius=2.17205 StartAngle=0 EndAngle=1.5708
    g6: Circle CenterX=0.573308 CenterY=20.1084 CenterZ=0 NormalX=0 NormalY=0 NormalZ=1 AngleXU=0 Radius=2.31699
  constraints (11):
    c: Coincident(g0,g1)
    c: Coincident(g3,g0)
    c: Horizontal(g0)
    c: Horizontal(g2)
    c: Vertical(g1)
    c: Vertical(g3)
    c: PointOnObject(g0,g-1)
    c: Tangent(g2,g4) = -1.5708
    c: Tangent(g3,g4) = -1.5708
    c: Tangent(g1,g5) = -1.5708
    c: Tangent(g2,g5) = -1.5708
FEATURE [PartDesign::Pad] Pad002001003004001007027
  Direction = (1,1,1)
  Length = 1
  Length2 = 100
  Profile = -> Sketch077
  Type = 0
FEATURE [PartDesign::Body] Body013  label="arriba001"
  Group = -> [Sketch077,Pad002001003004001007027]
  Origin = -> Origin013
  Placement = pos=(0,0,0) rot=(1,0,0;1.5708rad)
  Tip = -> Pad002001003004001007027
FEATURE [Part::Feature] Feature  label="Caster Ball Wheel001"
  Placement = pos=(-28.9438,-10.7904,28.5332) rot=(0.249523,0.103356,0.962838;3.9177rad)
  shape: bbox 29.7 x 30.78 x 34.21 mm, 46 faces, 2 solids (baked)
FEATURE [App::LinkGroup] LinkGroup001  label=" escuadra_final_2"
  ElementList = -> [Body013,Body012]
  LinkMode = 0
  Placement = pos=(-23.204,29.4444,-13.1959) rot=(0.58402,0.513758,-0.628469;0.04805rad)
FEATURE [App::LinkGroup] LinkGroup012  label="base_rueda_loca"
  ElementList = -> [LinkGroup011,LinkGroup001]
  LinkMode = 0
  Placement = pos=(-11.6611,30.1889,-27.6626) rot=(-0.532107,0.439789,0.723497;3.09707rad)
FEATURE [App::LinkGroup] LinkGroup013  label="union_final"
  ElementList = -> [Feature,LinkGroup012]
  LinkMode = 0
  Placement = pos=(-6.69896,144.196,13.5002) rot=(0.636741,0.770404,-0.032237;1.5244rad)
FEATURE [Sketcher::SketchObject] Sketch078
  FullyConstrained = false
  MapMode = 5
  Support = -> [XY_Plane014]
  sketch-geometry (4):
    g0: LineSegment StartX=-46.7569 StartY=40.5161 StartZ=0 EndX=33.2431 EndY=40.5161 EndZ=0
    g1: LineSegment StartX=33.2431 StartY=40.5161 StartZ=0 EndX=33.2431 EndY=-19.4739 EndZ=0
    g2: LineSegment StartX=33.2431 StartY=-19.4739 StartZ=0 EndX=-46.7569 EndY=-19.4739 EndZ=0
    g3: LineSegment StartX=-46.7569 StartY=-19.4739 StartZ=0 EndX=-46.7569 EndY=40.5161 EndZ=0
  constraints (10):
    c: Coincident(g0,g1)
    c: Coincident(g1,g2)
    c: Coincident(g2,g3)
    c: Coincident(g3,g0)
    c: Horizontal(g0)
    c: Horizontal(g2)
    c: Vertical(g1)
    c: Vertical(g3)
    c: DistanceX(g0,g0) = 80
    c: DistanceY(g1,g1) = 59.99
FEATURE [PartDesign::Pad] Pad002001003004001007028
  Direction = (1,1,1)
  Length = 3
  Length2 = 100
  Profile = -> Sketch078
  Type = 0
FEATURE [PartDesign::Body] Body014  label="proto"
  Group = -> [Sketch078,Pad002001003004001007028]
  Origin = -> Origin014
  Placement = pos=(6,220,75) rot=(0,0,1;0rad)
  Tip = -> Pad002001003004001007028
FEATURE [Sketcher::SketchObject] Sketch079
  FullyConstrained = false
  MapMode = 5
  Support = -> [XY_Plane015]
  sketch-geometry (4):
    g0: LineSegment StartX=-39.7547 StartY=27.4663 StartZ=0 EndX=40.2453 EndY=27.4663 EndZ=0
    g1: LineSegment StartX=40.2453 StartY=27.4663 StartZ=0 EndX=40.2453 EndY=-22.5337 EndZ=0
    g2: LineSegment StartX=40.2453 StartY=-22.5337 StartZ=0 EndX=-39.7547 EndY=-22.5337 EndZ=0
    g3: LineSegment StartX=-39.7547 StartY=-22.5337 StartZ=0 EndX=-39.7547 EndY=27.4663 EndZ=0
  constraints (10):
    c: Coincident(g0,g1)
    c: Coincident(g1,g2)
    c: Coincident(g2,g3)
    c: Coincident(g3,g0)
    c: Horizontal(g0)
    c: Horizontal(g2)
    c: Vertical(g1)
    c: Vertical(g3)
    c: DistanceX(g0,g0) = 80
    c: DistanceY(g1,g1) = 50
FEATURE [PartDesign::Pad] Pad002001003004001007029
  Direction = (1,1,1)
  Length = 2
  Length2 = 100
  Profile = -> Sketch079
  Type = 0
FEATURE [PartDesign::Body] Body015  label="base001"
  Group = -> [Sketch079,Pad002001003004001007029]
  Origin = -> Origin015
  Tip = -> Pad002001003004001007029
FEATURE [Sketcher::SketchObject] Sketch080
  FullyConstrained = false
  MapMode = 5
  Support = -> [XY_Plane016]
  sketch-geometry (4):
    g0: LineSegment StartX=59.5865 StartY=-13.365 StartZ=0 EndX=79.8925 EndY=-13.365 EndZ=0
    g1: LineSegment StartX=79.8925 StartY=-13.365 StartZ=0 EndX=79.8925 EndY=-32.002 EndZ=0
    g2: LineSegment StartX=79.8925 StartY=-32.002 StartZ=0 EndX=59.5865 EndY=-32.002 EndZ=0
    g3: LineSegment StartX=59.5865 StartY=-32.002 StartZ=0 EndX=59.5865 EndY=-13.365 EndZ=0
  constraints (8):
    c: Coincident(g0,g1)
    c: Coincident(g1,g2)
    c: Coincident(g2,g3)
    c: Coincident(g3,g0)
    c: Horizontal(g0)
    c: Horizontal(g2)
    c: Vertical(g1)
    c: Vertical(g3)
FEATURE [PartDesign::Pad] Pad002001003004001007030
  Direction = (1,1,1)
  Length = 1
  Length2 = 100
  Profile = -> Sketch080
  Type = 0
FEATURE [PartDesign::Body] Body016  label="chip"
  Group = -> [Sketch080,Pad002001003004001007030]
  Origin = -> Origin016
  Placement = pos=(-88,26,2) rot=(0,0,1;0rad)
  Tip = -> Pad002001003004001007030
FEATURE [Sketcher::SketchObject] Sketch081
  FullyConstrained = false
  MapMode = 5
  Support = -> [XY_Plane017]
  sketch-geometry (4):
    g0: LineSegment StartX=46.5283 StartY=3.66319 StartZ=0 EndX=58.2184 EndY=3.66319 EndZ=0
    g1: LineSegment StartX=58.2184 StartY=3.66319 StartZ=0 EndX=58.2184 EndY=-4.34671 EndZ=0
    g2: LineSegment StartX=58.2184 StartY=-4.34671 StartZ=0 EndX=46.5283 EndY=-4.34671 EndZ=0
    g3: LineSegment StartX=46.5283 StartY=-4.34671 StartZ=0 EndX=46.5283 EndY=3.66319 EndZ=0
  constraints (8):
    c: Coincident(g0,g1)
    c: Coincident(g1,g2)
    c: Coincident(g2,g3)
    c: Coincident(g3,g0)
    c: Horizontal(g0)
    c: Horizontal(g2)
    c: Vertical(g1)
    c: Vertical(g3)
FEATURE [PartDesign::Pad] Pad002001003004001007031
  Direction = (1,1,1)
  Length = 8
  Length2 = 100
  Profile = -> Sketch081
  Type = 0
FEATURE [PartDesign::Hole] Hole
  BaseFeature = -> Pad002001003004001007031
  Depth = 25
  DepthType = 0
  Diameter = 6
  DrillForDepth = false
  DrillPoint = 1
  DrillPointAngle = 118
  HoleCutCountersinkAngle = 90
  HoleCutCustomValues = false
  HoleCutDepth = 0
  HoleCutDiameter = 6.1
  HoleCutType = 0
  ModelActualThread = false
  Profile = -> Pad002001003004001007031
  Tapered = false
  TaperedAngle = 90
  ThreadAngle = 0
  ThreadClass = 0
  ThreadCutOffInner = 0
  ThreadCutOffOuter = 0
  ThreadDirection = 0
  ThreadFit = 0
  ThreadPitch = 0
  ThreadSize = 0
  ThreadType = 0
  Threaded = false
FEATURE [PartDesign::Body] Body017  label="conect"
  Group = -> [Sketch081,Pad002001003004001007031,Hole]
  Origin = -> Origin017
  Placement = pos=(-11,17,2) rot=(0,0,1;0rad)
  Tip = -> Hole
FEATURE [Sketcher::SketchObject] Sketch082
  FullyConstrained = false
  MapMode = 5
  Support = -> [XY_Plane018]
  sketch-geometry (1):
    g0: Circle CenterX=75.4358 CenterY=0 CenterZ=0 NormalX=0 NormalY=0 NormalZ=1 AngleXU=0 Radius=2.64986
  constraints (1):
    c: PointOnObject(g0,g-1)
FEATURE [PartDesign::Pad] Pad002001003004001007032
  Direction = (1,1,1)
  Length = 13
  Length2 = 100
  Profile = -> Sketch082
  Type = 0
FEATURE [PartDesign::Body] Body018  label="bateria"
  Group = -> [Sketch082,Pad002001003004001007032]
  Origin = -> Origin018
  Placement = pos=(44,70,4) rot=(0.57735,-0.57735,-0.57735;2.0944rad)
  Tip = -> Pad002001003004001007032
FEATURE [App::LinkGroup] LinkGroup014  label="ardu"
  ElementList = -> [Body018,Body017,Body016,Body015]
  LinkMode = 0
  Placement = pos=(1,167,76) rot=(0,0,1;0rad)
FEATURE [TechDraw::DrawSVGTemplate] Template
  EditableTexts = Designed_by_Name=Designed by Name; Drawing_number=Drawing number; FC-Date=Date; FC-SC=Scale; FC-SH=Sheet; FC-Title=Diseño final; Subtitle=Subtitle; Weight=Weight
  Height = 210
  Orientation = 1
  Width = 297
FEATURE [App::LinkGroup] LinkGroup015  label="final"
  ElementList = -> [LinkGroup014,Body014,LinkGroup013,LinkGroup010,LinkGroup008,Body007,LinkGroup007,LinkGroup006,LinkGroup005]
  LinkMode = 0
FEATURE [TechDraw::DrawProjGroupItem] ProjItem002  label="Front001"
  CoarseView = false
  Direction = (0,0,1)
  Focus = 100
  HardHidden = false
  IsoCount = 0
  IsoHidden = false
  IsoVisible = false
  LockPosition = true
  Perspective = false
  Rotation = 0
  RotationVector = (1,0,0)
  Scale = 0.333333
  ScaleType = 2
  SeamHidden = false
  SeamVisible = true
  SmoothHidden = false
  SmoothVisible = true
  Type = 0
  X = 0
  XDirection = (1,0,0)
  XSource = -> [LinkGroup015]
  Y = 0
FEATURE [TechDraw::DrawProjGroupItem] ProjItem  label="Left"
  CoarseView = false
  Direction = (-1,0,1e-16)
  Focus = 100
  HardHidden = false
  IsoCount = 0
  IsoHidden = false
  IsoVisible = false
  LockPosition = false
  Perspective = false
  Rotation = 0
  RotationVector = (1,0,0)
  ScaleType = 2
  SeamHidden = false
  SeamVisible = true
  SmoothHidden = false
  SmoothVisible = true
  Type = 1
  X = 61.8536
  XDirection = (1e-16,0,1)
  XSource = -> [LinkGroup015]
  Y = 0
FEATURE [TechDraw::DrawProjGroupItem] ProjItem003  label="Bottom"
  CoarseView = false
  Direction = (0,-1,0)
  Focus = 100
  HardHidden = false
  IsoCount = 0
  IsoHidden = false
  IsoVisible = false
  LockPosition = false
  Perspective = false
  Rotation = 0
  RotationVector = (1,0,0)
  ScaleType = 2
  SeamHidden = false
  SeamVisible = true
  SmoothHidden = false
  SmoothVisible = true
  Type = 5
  X = 0
  XDirection = (1,0,0)
  XSource = -> [LinkGroup015]
  Y = 64.0801
FEATURE [TechDraw::DrawProjGroup] ProjGroup001
  Anchor = -> ProjItem002
  AutoDistribute = true
  LockPosition = false
  ProjectionType = 0
  Rotation = 0
  Scale = 0.333333
  ScaleType = 2
  Views = -> [ProjItem002,ProjItem,ProjItem003]
  X = 78.2162
  XSource = -> [LinkGroup015]
  Y = 105.815
  spacingX = 15
  spacingY = 15
FEATURE [TechDraw::DrawPage] Page
  KeepUpdated = true
  NextBalloonIndex = 1
  ProjectionType = 0
  Template = -> Template
  Views = -> [ProjGroup001]
